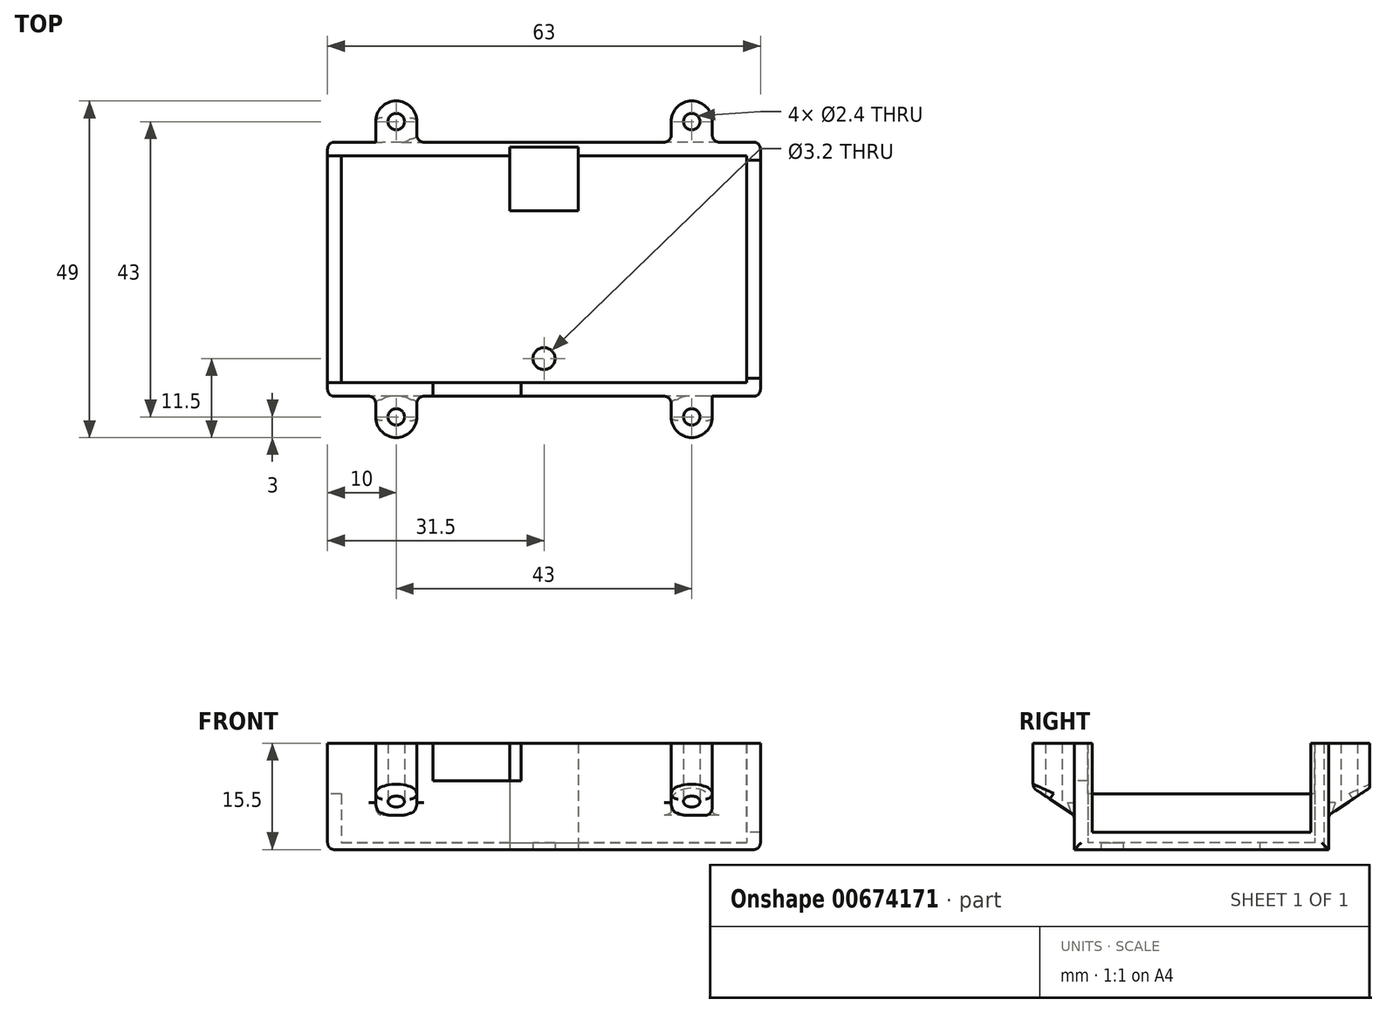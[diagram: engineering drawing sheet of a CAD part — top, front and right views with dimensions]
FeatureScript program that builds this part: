
annotation { "Feature Type Name" : "Feature", "Feature Type Description" : "" }
export const myFeature = defineFeature(function(context is Context, id is Id, definition is map)
    precondition{}
    {
        {
            var Q0;
            Q0=qCreatedBy(makeId("Top.planeOp"),FACE);
            var sketch = newSketch(context, id + "F0", { "sketchPlane" : qUnion([Q0])});
            skCircle(sketch, "E0", {"center": v(-7.34, 20.85) * mm, "radius": 0.75 * mm});
            skCircle(sketch, "E1", {"center": v(1.3, 25.15) * mm, "radius": 0.75 * mm});
            skCircle(sketch, "E2", {"center": v(-5.18, 20.85) * mm, "radius": 0.75 * mm});
            skCircle(sketch, "E3", {"center": v(3.46, 25.15) * mm, "radius": 0.75 * mm});
            skCircle(sketch, "E4", {"center": v(-3.02, 20.85) * mm, "radius": 0.75 * mm});
            skCircle(sketch, "E5", {"center": v(5.62, 25.15) * mm, "radius": 0.75 * mm});
            skCircle(sketch, "E6", {"center": v(-0.86, 20.85) * mm, "radius": 0.75 * mm});
            skCircle(sketch, "E7", {"center": v(1.3, 20.85) * mm, "radius": 0.75 * mm});
            skCircle(sketch, "E8", {"center": v(9.94, 25.15) * mm, "radius": 0.75 * mm});
            skCircle(sketch, "E9", {"center": v(3.46, 20.85) * mm, "radius": 0.75 * mm});
            skCircle(sketch, "E10", {"center": v(12.1, 25.15) * mm, "radius": 0.75 * mm});
            skCircle(sketch, "E11", {"center": v(5.62, 20.85) * mm, "radius": 0.75 * mm});
            skCircle(sketch, "E12", {"center": v(14.26, 25.15) * mm, "radius": 0.75 * mm});
            skCircle(sketch, "E13", {"center": v(7.78, 20.85) * mm, "radius": 0.75 * mm});
            skCircle(sketch, "E14", {"center": v(16.42, 25.15) * mm, "radius": 0.75 * mm});
            skCircle(sketch, "E15", {"center": v(9.94, 20.85) * mm, "radius": 0.75 * mm});
            skCircle(sketch, "E16", {"center": v(16.42, 20.85) * mm, "radius": 0.75 * mm});
            skCircle(sketch, "E17", {"center": v(12.1, 20.85) * mm, "radius": 0.75 * mm});
            skCircle(sketch, "E18", {"center": v(14.26, 20.85) * mm, "radius": 0.75 * mm});
            skCircle(sketch, "E19", {"center": v(7.78, 25.15) * mm, "radius": 0.75 * mm});
            skCircle(sketch, "E20", {"center": v(-7.34, 25.15) * mm, "radius": 0.75 * mm});
            skCircle(sketch, "E21", {"center": v(-5.18, 25.15) * mm, "radius": 0.75 * mm});
            skCircle(sketch, "E22", {"center": v(-3.02, 25.15) * mm, "radius": 0.75 * mm});
            skCircle(sketch, "E23", {"center": v(-0.86, 25.15) * mm, "radius": 0.75 * mm});
            skCircle(sketch, "E24", {"center": v(-18.86, 23) * mm, "radius": 1.6 * mm});
            skCircle(sketch, "E25", {"center": v(27.94, 23) * mm, "radius": 1.6 * mm});
            skLineSegment(sketch, "E26", {"start": v(4.04, 23) * mm, "end": v(5.04, 23) * mm});
            skLineSegment(sketch, "E27", {"start": v(4.54, 22.5) * mm, "end": v(4.54, 23.5) * mm});
            skLineSegment(sketch, "E28", {"start": v(-10.46, 27) * mm, "end": v(19.54, 27) * mm});
            skLineSegment(sketch, "E29", {"start": v(19.54, 27) * mm, "end": v(22.79, 19) * mm});
            skLineSegment(sketch, "E30", {"start": v(22.79, 19) * mm, "end": v(-13.71, 19) * mm});
            skLineSegment(sketch, "E31", {"start": v(-13.71, 19) * mm, "end": v(-10.46, 27) * mm});
            skLineSegment(sketch, "E32", {"start": v(-22.71, 33.4) * mm, "end": v(31.79, 33.4) * mm});
            skLineSegment(sketch, "E33", {"start": v(31.79, 33.4) * mm, "end": v(31.79, 17.1) * mm});
            skLineSegment(sketch, "E34", {"start": v(31.79, 17.1) * mm, "end": v(-22.71, 17.1) * mm});
            skLineSegment(sketch, "E35", {"start": v(-22.71, 17.1) * mm, "end": v(-22.71, 33.4) * mm});
            skCircle(sketch, "E36", {"center": v(29.08, 8.27) * mm, "radius": 0.75 * mm});
            skCircle(sketch, "E37", {"center": v(26.54, 8.27) * mm, "radius": 0.75 * mm});
            skCircle(sketch, "E38", {"center": v(24, 8.27) * mm, "radius": 0.75 * mm});
            skCircle(sketch, "E39", {"center": v(24, 5.73) * mm, "radius": 0.75 * mm});
            skCircle(sketch, "E40", {"center": v(29.08, 5.73) * mm, "radius": 0.75 * mm});
            skCircle(sketch, "E41", {"center": v(26.54, 5.73) * mm, "radius": 0.75 * mm});
            skLineSegment(sketch, "E42", {"start": v(27.04, 7) * mm, "end": v(26.04, 7) * mm});
            skLineSegment(sketch, "E43", {"start": v(26.54, 7.5) * mm, "end": v(26.54, 6.5) * mm});
            skLineSegment(sketch, "E44", {"start": v(31.54, 9.2) * mm, "end": v(31.54, 3.6) * mm});
            skLineSegment(sketch, "E45", {"start": v(31.54, 3.6) * mm, "end": v(21.54, 3.6) * mm});
            skLineSegment(sketch, "E46", {"start": v(21.54, 3.6) * mm, "end": v(21.54, 9.2) * mm});
            skLineSegment(sketch, "E47", {"start": v(21.54, 9.2) * mm, "end": v(31.54, 9.2) * mm});
            skCircle(sketch, "E48", {"center": v(2, -25.73) * mm, "radius": 0.75 * mm});
            skCircle(sketch, "E49", {"center": v(4.54, -25.73) * mm, "radius": 0.75 * mm});
            skCircle(sketch, "E50", {"center": v(7.08, -25.73) * mm, "radius": 0.75 * mm});
            skCircle(sketch, "E51", {"center": v(7.08, -28.27) * mm, "radius": 0.75 * mm});
            skCircle(sketch, "E52", {"center": v(2, -28.27) * mm, "radius": 0.75 * mm});
            skCircle(sketch, "E53", {"center": v(4.54, -28.27) * mm, "radius": 0.75 * mm});
            skLineSegment(sketch, "E54", {"start": v(4.04, -27) * mm, "end": v(5.04, -27) * mm});
            skLineSegment(sketch, "E55", {"start": v(4.54, -26.5) * mm, "end": v(4.54, -27.5) * mm});
            skLineSegment(sketch, "E56", {"start": v(-0.46, -24.8) * mm, "end": v(-0.46, -31.7) * mm});
            skLineSegment(sketch, "E57", {"start": v(-0.46, -31.7) * mm, "end": v(9.54, -31.7) * mm});
            skLineSegment(sketch, "E58", {"start": v(9.54, -31.7) * mm, "end": v(9.54, -24.8) * mm});
            skLineSegment(sketch, "E59", {"start": v(9.54, -24.8) * mm, "end": v(-0.46, -24.8) * mm});
            skLineSegment(sketch, "E60", {"start": v(22.8, 13.74) * mm, "end": v(22.8, 15.26) * mm});
            skLineSegment(sketch, "E61", {"start": v(22.8, 15.26) * mm, "end": v(21.28, 15.26) * mm});
            skLineSegment(sketch, "E62", {"start": v(21.28, 15.26) * mm, "end": v(21.28, 13.74) * mm});
            skLineSegment(sketch, "E63", {"start": v(21.28, 13.74) * mm, "end": v(22.8, 13.74) * mm});
            skCircle(sketch, "E64", {"center": v(24.54, 14.5) * mm, "radius": 0.76 * mm});
            skCircle(sketch, "E65", {"center": v(27.04, 14.5) * mm, "radius": 0.76 * mm});
            skCircle(sketch, "E66", {"center": v(29.54, 14.5) * mm, "radius": 0.76 * mm});
            skLineSegment(sketch, "E67", {"start": v(31.99, 11.12) * mm, "end": v(19.59, 11.12) * mm});
            skLineSegment(sketch, "E68", {"start": v(19.59, 11.12) * mm, "end": v(19.59, 16.02) * mm});
            skLineSegment(sketch, "E69", {"start": v(19.59, 16.02) * mm, "end": v(31.99, 16.02) * mm});
            skLineSegment(sketch, "E70", {"start": v(31.99, 16.02) * mm, "end": v(31.99, 11.12) * mm});
            skLineSegment(sketch, "E71", {"start": v(30.99, 16.02) * mm, "end": v(31.99, 15.02) * mm});
            skLineSegment(sketch, "E72", {"start": v(20.59, 16.02) * mm, "end": v(19.59, 15.02) * mm});
            skLineSegment(sketch, "E73", {"start": v(-2.22, -0.26) * mm, "end": v(-2.22, 1.26) * mm});
            skLineSegment(sketch, "E74", {"start": v(-2.22, 1.26) * mm, "end": v(-0.7, 1.26) * mm});
            skLineSegment(sketch, "E75", {"start": v(-0.7, 1.26) * mm, "end": v(-0.7, -0.26) * mm});
            skLineSegment(sketch, "E76", {"start": v(-0.7, -0.26) * mm, "end": v(-2.22, -0.26) * mm});
            skCircle(sketch, "E77", {"center": v(-3.96, 0.5) * mm, "radius": 0.76 * mm});
            skCircle(sketch, "E78", {"center": v(-6.46, 0.5) * mm, "radius": 0.76 * mm});
            skCircle(sketch, "E79", {"center": v(-8.96, 0.5) * mm, "radius": 0.76 * mm});
            skLineSegment(sketch, "E80", {"start": v(-11.41, -2.88) * mm, "end": v(0.99, -2.88) * mm});
            skLineSegment(sketch, "E81", {"start": v(0.99, -2.88) * mm, "end": v(0.99, 2.02) * mm});
            skLineSegment(sketch, "E82", {"start": v(0.99, 2.02) * mm, "end": v(-11.41, 2.02) * mm});
            skLineSegment(sketch, "E83", {"start": v(-11.41, 2.02) * mm, "end": v(-11.41, -2.88) * mm});
            skLineSegment(sketch, "E84", {"start": v(-10.41, 2.02) * mm, "end": v(-11.41, 1.02) * mm});
            skLineSegment(sketch, "E85", {"start": v(-0.01, 2.02) * mm, "end": v(0.99, 1.02) * mm});
            skLineSegment(sketch, "E86", {"start": v(16.29, 27.5) * mm, "end": v(16.29, 29.5) * mm});
            skLineSegment(sketch, "E87", {"start": v(16.29, 29.5) * mm, "end": v(21.79, 29.5) * mm});
            skLineSegment(sketch, "E88", {"start": v(21.79, 29.5) * mm, "end": v(21.79, 27.5) * mm});
            skLineSegment(sketch, "E89", {"start": v(21.79, 27.5) * mm, "end": v(16.29, 27.5) * mm});
            skLineSegment(sketch, "E90", {"start": v(25.29, 27.5) * mm, "end": v(25.29, 29.5) * mm});
            skLineSegment(sketch, "E91", {"start": v(25.29, 29.5) * mm, "end": v(30.79, 29.5) * mm});
            skLineSegment(sketch, "E92", {"start": v(30.79, 29.5) * mm, "end": v(30.79, 27.5) * mm});
            skLineSegment(sketch, "E93", {"start": v(30.79, 27.5) * mm, "end": v(25.29, 27.5) * mm});
            skLineSegment(sketch, "E94", {"start": v(18.54, 31) * mm, "end": v(28.54, 31) * mm});
            skArc(sketch, "E95", {"start": v(17.29, 29.75) * mm, "mid": v(17.66, 30.63) * mm, "end": v(18.54, 31) * mm});
            skArc(sketch, "E96", {"start": v(29.79, 29.75) * mm, "mid": v(29.42, 30.63) * mm, "end": v(28.54, 31) * mm});
            skLineSegment(sketch, "E97", {"start": v(28.54, 26) * mm, "end": v(18.54, 26) * mm});
            skArc(sketch, "E98", {"start": v(17.29, 27.25) * mm, "mid": v(17.66, 26.37) * mm, "end": v(18.54, 26) * mm});
            skArc(sketch, "E99", {"start": v(29.79, 27.25) * mm, "mid": v(29.42, 26.37) * mm, "end": v(28.54, 26) * mm});
            skLineSegment(sketch, "E100", {"start": v(23.04, 28.5) * mm, "end": v(24.04, 28.5) * mm});
            skLineSegment(sketch, "E101", {"start": v(23.54, 29) * mm, "end": v(23.54, 28) * mm});
            skLineSegment(sketch, "E102", {"start": v(-5.46, -18.25) * mm, "end": v(-7.46, -18.25) * mm});
            skLineSegment(sketch, "E103", {"start": v(-7.46, -18.25) * mm, "end": v(-7.46, -12.75) * mm});
            skLineSegment(sketch, "E104", {"start": v(-7.46, -12.75) * mm, "end": v(-5.46, -12.75) * mm});
            skLineSegment(sketch, "E105", {"start": v(-5.46, -12.75) * mm, "end": v(-5.46, -18.25) * mm});
            skLineSegment(sketch, "E106", {"start": v(-5.46, -9.25) * mm, "end": v(-7.46, -9.25) * mm});
            skLineSegment(sketch, "E107", {"start": v(-7.46, -9.25) * mm, "end": v(-7.46, -3.75) * mm});
            skLineSegment(sketch, "E108", {"start": v(-7.46, -3.75) * mm, "end": v(-5.46, -3.75) * mm});
            skLineSegment(sketch, "E109", {"start": v(-5.46, -3.75) * mm, "end": v(-5.46, -9.25) * mm});
            skLineSegment(sketch, "E110", {"start": v(-8.96, -16) * mm, "end": v(-8.96, -6) * mm});
            skArc(sketch, "E111", {"start": v(-7.71, -17.25) * mm, "mid": v(-8.6, -16.88) * mm, "end": v(-8.96, -16) * mm});
            skArc(sketch, "E112", {"start": v(-7.71, -4.75) * mm, "mid": v(-8.6, -5.12) * mm, "end": v(-8.96, -6) * mm});
            skLineSegment(sketch, "E113", {"start": v(-3.96, -6) * mm, "end": v(-3.96, -16) * mm});
            skArc(sketch, "E114", {"start": v(-5.21, -17.25) * mm, "mid": v(-4.33, -16.88) * mm, "end": v(-3.96, -16) * mm});
            skArc(sketch, "E115", {"start": v(-5.21, -4.75) * mm, "mid": v(-4.33, -5.12) * mm, "end": v(-3.96, -6) * mm});
            skLineSegment(sketch, "E116", {"start": v(-6.46, -11.5) * mm, "end": v(-6.46, -10.5) * mm});
            skLineSegment(sketch, "E117", {"start": v(-6.96, -11) * mm, "end": v(-5.96, -11) * mm});
            skLineSegment(sketch, "E118", {"start": v(14.89, 1.65) * mm, "end": v(17.19, 1.65) * mm});
            skLineSegment(sketch, "E119", {"start": v(17.19, 1.65) * mm, "end": v(17.19, -0.65) * mm});
            skLineSegment(sketch, "E120", {"start": v(17.19, -0.65) * mm, "end": v(14.89, -0.65) * mm});
            skLineSegment(sketch, "E121", {"start": v(14.89, -0.65) * mm, "end": v(14.89, 1.65) * mm});
            skLineSegment(sketch, "E122", {"start": v(14.89, -2.35) * mm, "end": v(17.19, -2.35) * mm});
            skLineSegment(sketch, "E123", {"start": v(17.19, -2.35) * mm, "end": v(17.19, -4.65) * mm});
            skLineSegment(sketch, "E124", {"start": v(17.19, -4.65) * mm, "end": v(14.89, -4.65) * mm});
            skLineSegment(sketch, "E125", {"start": v(14.89, -4.65) * mm, "end": v(14.89, -2.35) * mm});
            skLineSegment(sketch, "E126", {"start": v(16.04, -1.5) * mm, "end": v(15.41, -0.87) * mm});
            skLineSegment(sketch, "E127", {"start": v(15.41, -0.88) * mm, "end": v(16.66, -0.88) * mm});
            skLineSegment(sketch, "E128", {"start": v(16.66, -0.88) * mm, "end": v(16.04, -1.5) * mm});
            skLineSegment(sketch, "E129", {"start": v(17.04, -1.75) * mm, "end": v(16.79, -1.5) * mm});
            skLineSegment(sketch, "E130", {"start": v(16.79, -1.5) * mm, "end": v(15.29, -1.5) * mm});
            skLineSegment(sketch, "E131", {"start": v(15.29, -1.5) * mm, "end": v(15.04, -1.25) * mm});
            skLineSegment(sketch, "E132", {"start": v(18.04, 1.88) * mm, "end": v(18.04, -4.88) * mm});
            skLineSegment(sketch, "E133", {"start": v(18.04, -4.88) * mm, "end": v(14.04, -4.88) * mm});
            skLineSegment(sketch, "E134", {"start": v(14.04, -4.88) * mm, "end": v(14.04, 1.88) * mm});
            skLineSegment(sketch, "E135", {"start": v(14.04, 1.88) * mm, "end": v(18.04, 1.88) * mm});
            skLineSegment(sketch, "E136", {"start": v(16.04, -1.5) * mm, "end": v(16.66, -2.12) * mm});
            skLineSegment(sketch, "E137", {"start": v(16.66, -2.12) * mm, "end": v(15.41, -2.12) * mm});
            skLineSegment(sketch, "E138", {"start": v(15.41, -2.12) * mm, "end": v(16.04, -1.5) * mm});
            skLineSegment(sketch, "E139", {"start": v(19.39, 1.65) * mm, "end": v(21.69, 1.65) * mm});
            skLineSegment(sketch, "E140", {"start": v(21.69, 1.65) * mm, "end": v(21.69, -0.65) * mm});
            skLineSegment(sketch, "E141", {"start": v(21.69, -0.65) * mm, "end": v(19.39, -0.65) * mm});
            skLineSegment(sketch, "E142", {"start": v(19.39, -0.65) * mm, "end": v(19.39, 1.65) * mm});
            skLineSegment(sketch, "E143", {"start": v(19.39, -2.35) * mm, "end": v(21.69, -2.35) * mm});
            skLineSegment(sketch, "E144", {"start": v(21.69, -2.35) * mm, "end": v(21.69, -4.65) * mm});
            skLineSegment(sketch, "E145", {"start": v(21.69, -4.65) * mm, "end": v(19.39, -4.65) * mm});
            skLineSegment(sketch, "E146", {"start": v(19.39, -4.65) * mm, "end": v(19.39, -2.35) * mm});
            skLineSegment(sketch, "E147", {"start": v(20.54, -1.5) * mm, "end": v(19.91, -0.88) * mm});
            skLineSegment(sketch, "E148", {"start": v(19.91, -0.88) * mm, "end": v(21.16, -0.88) * mm});
            skLineSegment(sketch, "E149", {"start": v(21.16, -0.88) * mm, "end": v(20.54, -1.5) * mm});
            skLineSegment(sketch, "E150", {"start": v(21.54, -1.75) * mm, "end": v(21.29, -1.5) * mm});
            skLineSegment(sketch, "E151", {"start": v(21.29, -1.5) * mm, "end": v(19.79, -1.5) * mm});
            skLineSegment(sketch, "E152", {"start": v(19.79, -1.5) * mm, "end": v(19.54, -1.25) * mm});
            skLineSegment(sketch, "E153", {"start": v(22.54, 1.88) * mm, "end": v(22.54, -4.88) * mm});
            skLineSegment(sketch, "E154", {"start": v(22.54, -4.88) * mm, "end": v(18.54, -4.88) * mm});
            skLineSegment(sketch, "E155", {"start": v(18.54, -4.88) * mm, "end": v(18.54, 1.88) * mm});
            skLineSegment(sketch, "E156", {"start": v(18.54, 1.88) * mm, "end": v(22.54, 1.88) * mm});
            skLineSegment(sketch, "E157", {"start": v(20.54, -1.5) * mm, "end": v(21.16, -2.12) * mm});
            skLineSegment(sketch, "E158", {"start": v(21.16, -2.12) * mm, "end": v(19.91, -2.12) * mm});
            skLineSegment(sketch, "E159", {"start": v(19.91, -2.12) * mm, "end": v(20.54, -1.5) * mm});
            skLineSegment(sketch, "E160", {"start": v(-18.96, 17.1) * mm, "end": v(-18.96, 18.9) * mm});
            skLineSegment(sketch, "E161", {"start": v(-18.96, 18.9) * mm, "end": v(-17.96, 18.9) * mm});
            skLineSegment(sketch, "E162", {"start": v(-17.96, 18.9) * mm, "end": v(-17.96, 17.1) * mm});
            skLineSegment(sketch, "E163", {"start": v(-17.96, 17.1) * mm, "end": v(-18.96, 17.1) * mm});
            skLineSegment(sketch, "E164", {"start": v(-15.96, 17.1) * mm, "end": v(-15.96, 18.9) * mm});
            skLineSegment(sketch, "E165", {"start": v(-15.96, 18.9) * mm, "end": v(-14.96, 18.9) * mm});
            skLineSegment(sketch, "E166", {"start": v(-14.96, 18.9) * mm, "end": v(-14.96, 17.1) * mm});
            skLineSegment(sketch, "E167", {"start": v(-14.96, 17.1) * mm, "end": v(-15.96, 17.1) * mm});
            skLineSegment(sketch, "E168", {"start": v(-17.34, 19.12) * mm, "end": v(-19.21, 19.12) * mm});
            skLineSegment(sketch, "E169", {"start": v(-19.21, 19.12) * mm, "end": v(-19.21, 16.88) * mm});
            skLineSegment(sketch, "E170", {"start": v(-19.21, 16.88) * mm, "end": v(-17.34, 16.88) * mm});
            skArc(sketch, "E171", {"start": v(-16.76, 18) * mm, "mid": v(-16.96, 18.2) * mm, "end": v(-17.16, 18) * mm});
            skArc(sketch, "E172", {"start": v(-17.16, 18) * mm, "mid": v(-16.96, 17.8) * mm, "end": v(-16.76, 18) * mm});
            skLineSegment(sketch, "E173", {"start": v(-16.59, 16.88) * mm, "end": v(-14.71, 16.88) * mm});
            skLineSegment(sketch, "E174", {"start": v(-14.71, 16.88) * mm, "end": v(-14.71, 19.12) * mm});
            skLineSegment(sketch, "E175", {"start": v(-14.71, 19.12) * mm, "end": v(-16.59, 19.12) * mm});
            skArc(sketch, "E176", {"start": v(-16.59, 19.12) * mm, "mid": v(-16.96, 18.75) * mm, "end": v(-17.34, 19.12) * mm});
            skArc(sketch, "E177", {"start": v(-17.34, 16.88) * mm, "mid": v(-16.96, 17.25) * mm, "end": v(-16.59, 16.88) * mm});
            skLineSegment(sketch, "E178", {"start": v(-9.81, -9.5) * mm, "end": v(-11.61, -9.5) * mm});
            skLineSegment(sketch, "E179", {"start": v(-11.61, -9.5) * mm, "end": v(-11.61, -8.5) * mm});
            skLineSegment(sketch, "E180", {"start": v(-11.61, -8.5) * mm, "end": v(-9.81, -8.5) * mm});
            skLineSegment(sketch, "E181", {"start": v(-9.81, -8.5) * mm, "end": v(-9.81, -9.5) * mm});
            skLineSegment(sketch, "E182", {"start": v(-9.81, -6.5) * mm, "end": v(-11.61, -6.5) * mm});
            skLineSegment(sketch, "E183", {"start": v(-11.61, -6.5) * mm, "end": v(-11.61, -5.5) * mm});
            skLineSegment(sketch, "E184", {"start": v(-11.61, -5.5) * mm, "end": v(-9.81, -5.5) * mm});
            skLineSegment(sketch, "E185", {"start": v(-9.81, -5.5) * mm, "end": v(-9.81, -6.5) * mm});
            skLineSegment(sketch, "E186", {"start": v(-11.84, -7.88) * mm, "end": v(-11.84, -9.75) * mm});
            skLineSegment(sketch, "E187", {"start": v(-11.84, -9.75) * mm, "end": v(-9.59, -9.75) * mm});
            skLineSegment(sketch, "E188", {"start": v(-9.59, -9.75) * mm, "end": v(-9.59, -7.88) * mm});
            skArc(sketch, "E189", {"start": v(-10.51, -7.5) * mm, "mid": v(-10.71, -7.3) * mm, "end": v(-10.91, -7.5) * mm});
            skArc(sketch, "E190", {"start": v(-10.91, -7.5) * mm, "mid": v(-10.71, -7.7) * mm, "end": v(-10.51, -7.5) * mm});
            skLineSegment(sketch, "E191", {"start": v(-9.59, -7.12) * mm, "end": v(-9.59, -5.25) * mm});
            skLineSegment(sketch, "E192", {"start": v(-9.59, -5.25) * mm, "end": v(-11.84, -5.25) * mm});
            skLineSegment(sketch, "E193", {"start": v(-11.84, -5.25) * mm, "end": v(-11.84, -7.12) * mm});
            skArc(sketch, "E194", {"start": v(-11.84, -7.12) * mm, "mid": v(-11.46, -7.5) * mm, "end": v(-11.84, -7.88) * mm});
            skArc(sketch, "E195", {"start": v(-9.59, -7.88) * mm, "mid": v(-9.96, -7.5) * mm, "end": v(-9.59, -7.12) * mm});
            skLineSegment(sketch, "E196", {"start": v(8.64, 6.85) * mm, "end": v(8.64, 4.15) * mm});
            skLineSegment(sketch, "E197", {"start": v(8.64, 4.15) * mm, "end": v(7.44, 4.15) * mm});
            skLineSegment(sketch, "E198", {"start": v(7.44, 4.15) * mm, "end": v(7.44, 6.85) * mm});
            skLineSegment(sketch, "E199", {"start": v(7.44, 6.85) * mm, "end": v(8.64, 6.85) * mm});
            skLineSegment(sketch, "E200", {"start": v(5.64, 6.85) * mm, "end": v(5.64, 4.15) * mm});
            skLineSegment(sketch, "E201", {"start": v(5.64, 4.15) * mm, "end": v(4.44, 4.15) * mm});
            skLineSegment(sketch, "E202", {"start": v(4.44, 4.15) * mm, "end": v(4.44, 6.85) * mm});
            skLineSegment(sketch, "E203", {"start": v(4.44, 6.85) * mm, "end": v(5.64, 6.85) * mm});
            skArc(sketch, "E204", {"start": v(8.54, 7.1) * mm, "mid": v(8.79, 7) * mm, "end": v(8.89, 6.75) * mm});
            skLineSegment(sketch, "E205", {"start": v(8.89, 4.25) * mm, "end": v(8.89, 6.75) * mm});
            skArc(sketch, "E206", {"start": v(8.89, 4.25) * mm, "mid": v(8.79, 4) * mm, "end": v(8.54, 3.9) * mm});
            skLineSegment(sketch, "E207", {"start": v(4.54, 7.1) * mm, "end": v(8.54, 7.1) * mm});
            skLineSegment(sketch, "E208", {"start": v(8.54, 3.9) * mm, "end": v(4.54, 3.9) * mm});
            skArc(sketch, "E209", {"start": v(6.74, 5.5) * mm, "mid": v(6.54, 5.7) * mm, "end": v(6.34, 5.5) * mm});
            skArc(sketch, "E210", {"start": v(6.34, 5.5) * mm, "mid": v(6.54, 5.3) * mm, "end": v(6.74, 5.5) * mm});
            skArc(sketch, "E211", {"start": v(4.19, 6.75) * mm, "mid": v(4.29, 7) * mm, "end": v(4.54, 7.1) * mm});
            skArc(sketch, "E212", {"start": v(4.54, 3.9) * mm, "mid": v(4.29, 4) * mm, "end": v(4.19, 4.25) * mm});
            skLineSegment(sketch, "E213", {"start": v(4.19, 6.75) * mm, "end": v(4.19, 4.25) * mm});
            skLineSegment(sketch, "E214", {"start": v(4.44, -21.35) * mm, "end": v(4.44, -18.65) * mm});
            skLineSegment(sketch, "E215", {"start": v(4.44, -18.65) * mm, "end": v(5.64, -18.65) * mm});
            skLineSegment(sketch, "E216", {"start": v(5.64, -18.65) * mm, "end": v(5.64, -21.35) * mm});
            skLineSegment(sketch, "E217", {"start": v(5.64, -21.35) * mm, "end": v(4.44, -21.35) * mm});
            skLineSegment(sketch, "E218", {"start": v(7.44, -21.35) * mm, "end": v(7.44, -18.65) * mm});
            skLineSegment(sketch, "E219", {"start": v(7.44, -18.65) * mm, "end": v(8.64, -18.65) * mm});
            skLineSegment(sketch, "E220", {"start": v(8.64, -18.65) * mm, "end": v(8.64, -21.35) * mm});
            skLineSegment(sketch, "E221", {"start": v(8.64, -21.35) * mm, "end": v(7.44, -21.35) * mm});
            skArc(sketch, "E222", {"start": v(4.54, -21.6) * mm, "mid": v(4.29, -21.5) * mm, "end": v(4.19, -21.25) * mm});
            skLineSegment(sketch, "E223", {"start": v(4.19, -18.75) * mm, "end": v(4.19, -21.25) * mm});
            skArc(sketch, "E224", {"start": v(4.19, -18.75) * mm, "mid": v(4.29, -18.5) * mm, "end": v(4.54, -18.4) * mm});
            skLineSegment(sketch, "E225", {"start": v(8.54, -21.6) * mm, "end": v(4.54, -21.6) * mm});
            skLineSegment(sketch, "E226", {"start": v(4.54, -18.4) * mm, "end": v(8.54, -18.4) * mm});
            skArc(sketch, "E227", {"start": v(6.74, -20) * mm, "mid": v(6.54, -19.8) * mm, "end": v(6.34, -20) * mm});
            skArc(sketch, "E228", {"start": v(6.34, -20) * mm, "mid": v(6.54, -20.2) * mm, "end": v(6.74, -20) * mm});
            skArc(sketch, "E229", {"start": v(8.89, -21.25) * mm, "mid": v(8.79, -21.5) * mm, "end": v(8.54, -21.6) * mm});
            skArc(sketch, "E230", {"start": v(8.54, -18.4) * mm, "mid": v(8.79, -18.5) * mm, "end": v(8.89, -18.75) * mm});
            skLineSegment(sketch, "E231", {"start": v(8.89, -21.25) * mm, "end": v(8.89, -18.75) * mm});
            skLineSegment(sketch, "E232", {"start": v(-10.11, 4.85) * mm, "end": v(-10.11, 7.15) * mm});
            skLineSegment(sketch, "E233", {"start": v(-10.11, 7.15) * mm, "end": v(-7.81, 7.15) * mm});
            skLineSegment(sketch, "E234", {"start": v(-7.81, 7.15) * mm, "end": v(-7.81, 4.85) * mm});
            skLineSegment(sketch, "E235", {"start": v(-7.81, 4.85) * mm, "end": v(-10.11, 4.85) * mm});
            skLineSegment(sketch, "E236", {"start": v(-6.11, 4.85) * mm, "end": v(-6.11, 7.15) * mm});
            skLineSegment(sketch, "E237", {"start": v(-6.11, 7.15) * mm, "end": v(-3.81, 7.15) * mm});
            skLineSegment(sketch, "E238", {"start": v(-3.81, 7.15) * mm, "end": v(-3.81, 4.85) * mm});
            skLineSegment(sketch, "E239", {"start": v(-3.81, 4.85) * mm, "end": v(-6.11, 4.85) * mm});
            skLineSegment(sketch, "E240", {"start": v(-7.46, 6) * mm, "end": v(-6.46, 6) * mm});
            skLineSegment(sketch, "E241", {"start": v(-6.96, 6.5) * mm, "end": v(-6.96, 5.5) * mm});
            skLineSegment(sketch, "E242", {"start": v(-10.71, 8) * mm, "end": v(-3.46, 8) * mm});
            skLineSegment(sketch, "E243", {"start": v(-3.46, 8) * mm, "end": v(-3.46, 4) * mm});
            skLineSegment(sketch, "E244", {"start": v(-3.46, 4) * mm, "end": v(-10.71, 4) * mm});
            skLineSegment(sketch, "E245", {"start": v(-10.71, 4) * mm, "end": v(-10.71, 8) * mm});
            skLineSegment(sketch, "E246", {"start": v(-10.71, 7.75) * mm, "end": v(-10.71, 4.25) * mm});
            skLineSegment(sketch, "E247", {"start": v(-10.71, 4.25) * mm, "end": v(-10.71, 4) * mm});
            skLineSegment(sketch, "E248", {"start": v(-10.71, 4) * mm, "end": v(-10.21, 4) * mm});
            skLineSegment(sketch, "E249", {"start": v(-10.21, 4) * mm, "end": v(-10.21, 4.25) * mm});
            skLineSegment(sketch, "E250", {"start": v(-10.21, 4.25) * mm, "end": v(-10.21, 4.75) * mm});
            skLineSegment(sketch, "E251", {"start": v(-10.21, 4.75) * mm, "end": v(-10.21, 7.25) * mm});
            skLineSegment(sketch, "E252", {"start": v(-10.21, 7.25) * mm, "end": v(-10.21, 7.75) * mm});
            skLineSegment(sketch, "E253", {"start": v(-10.21, 7.75) * mm, "end": v(-10.21, 8) * mm});
            skLineSegment(sketch, "E254", {"start": v(-10.21, 8) * mm, "end": v(-10.46, 8) * mm});
            skLineSegment(sketch, "E255", {"start": v(-10.46, 8) * mm, "end": v(-10.71, 8) * mm});
            skLineSegment(sketch, "E256", {"start": v(-10.71, 8) * mm, "end": v(-10.71, 7.75) * mm});
            skLineSegment(sketch, "E257", {"start": v(-15.11, 1.65) * mm, "end": v(-12.81, 1.65) * mm});
            skLineSegment(sketch, "E258", {"start": v(-12.81, 1.65) * mm, "end": v(-12.81, -0.65) * mm});
            skLineSegment(sketch, "E259", {"start": v(-12.81, -0.65) * mm, "end": v(-15.11, -0.65) * mm});
            skLineSegment(sketch, "E260", {"start": v(-15.11, -0.65) * mm, "end": v(-15.11, 1.65) * mm});
            skLineSegment(sketch, "E261", {"start": v(-15.11, -2.35) * mm, "end": v(-12.81, -2.35) * mm});
            skLineSegment(sketch, "E262", {"start": v(-12.81, -2.35) * mm, "end": v(-12.81, -4.65) * mm});
            skLineSegment(sketch, "E263", {"start": v(-12.81, -4.65) * mm, "end": v(-15.11, -4.65) * mm});
            skLineSegment(sketch, "E264", {"start": v(-15.11, -4.65) * mm, "end": v(-15.11, -2.35) * mm});
            skLineSegment(sketch, "E265", {"start": v(-13.96, -1) * mm, "end": v(-13.96, -2) * mm});
            skLineSegment(sketch, "E266", {"start": v(-13.46, -1.5) * mm, "end": v(-14.46, -1.5) * mm});
            skLineSegment(sketch, "E267", {"start": v(-11.96, 2.25) * mm, "end": v(-11.96, -5) * mm});
            skLineSegment(sketch, "E268", {"start": v(-11.96, -5) * mm, "end": v(-15.96, -5) * mm});
            skLineSegment(sketch, "E269", {"start": v(-15.96, -5) * mm, "end": v(-15.96, 2.25) * mm});
            skLineSegment(sketch, "E270", {"start": v(-15.96, 2.25) * mm, "end": v(-11.96, 2.25) * mm});
            skLineSegment(sketch, "E271", {"start": v(-12.21, 2.25) * mm, "end": v(-15.71, 2.25) * mm});
            skLineSegment(sketch, "E272", {"start": v(-15.71, 2.25) * mm, "end": v(-15.96, 2.25) * mm});
            skLineSegment(sketch, "E273", {"start": v(-15.96, 2.25) * mm, "end": v(-15.96, 1.75) * mm});
            skLineSegment(sketch, "E274", {"start": v(-15.96, 1.75) * mm, "end": v(-15.71, 1.75) * mm});
            skLineSegment(sketch, "E275", {"start": v(-15.71, 1.75) * mm, "end": v(-15.21, 1.75) * mm});
            skLineSegment(sketch, "E276", {"start": v(-15.21, 1.75) * mm, "end": v(-12.71, 1.75) * mm});
            skLineSegment(sketch, "E277", {"start": v(-12.71, 1.75) * mm, "end": v(-12.21, 1.75) * mm});
            skLineSegment(sketch, "E278", {"start": v(-12.21, 1.75) * mm, "end": v(-11.96, 1.75) * mm});
            skLineSegment(sketch, "E279", {"start": v(-11.96, 1.75) * mm, "end": v(-11.96, 2) * mm});
            skLineSegment(sketch, "E280", {"start": v(-11.96, 2) * mm, "end": v(-11.96, 2.25) * mm});
            skLineSegment(sketch, "E281", {"start": v(-11.96, 2.25) * mm, "end": v(-12.21, 2.25) * mm});
            skLineSegment(sketch, "E282", {"start": v(3.79, 28) * mm, "end": v(3.79, 27) * mm});
            skLineSegment(sketch, "E283", {"start": v(3.79, 27) * mm, "end": v(2.79, 27) * mm});
            skLineSegment(sketch, "E284", {"start": v(2.79, 27) * mm, "end": v(2.79, 28) * mm});
            skLineSegment(sketch, "E285", {"start": v(2.79, 28) * mm, "end": v(3.79, 28) * mm});
            skLineSegment(sketch, "E286", {"start": v(2.29, 28) * mm, "end": v(2.29, 27) * mm});
            skLineSegment(sketch, "E287", {"start": v(2.29, 27) * mm, "end": v(1.29, 27) * mm});
            skLineSegment(sketch, "E288", {"start": v(1.29, 27) * mm, "end": v(1.29, 28) * mm});
            skLineSegment(sketch, "E289", {"start": v(1.29, 28) * mm, "end": v(2.29, 28) * mm});
            skArc(sketch, "E290", {"start": v(4.04, 27.9) * mm, "mid": v(3.95, 28.11) * mm, "end": v(3.74, 28.2) * mm});
            skLineSegment(sketch, "E291", {"start": v(4.04, 27.1) * mm, "end": v(4.04, 27.9) * mm});
            skArc(sketch, "E292", {"start": v(4.04, 27.1) * mm, "mid": v(3.95, 26.89) * mm, "end": v(3.74, 26.8) * mm});
            skLineSegment(sketch, "E293", {"start": v(1.34, 28.2) * mm, "end": v(3.74, 28.2) * mm});
            skLineSegment(sketch, "E294", {"start": v(3.74, 26.8) * mm, "end": v(1.34, 26.8) * mm});
            skArc(sketch, "E295", {"start": v(2.64, 27.5) * mm, "mid": v(2.54, 27.6) * mm, "end": v(2.44, 27.5) * mm});
            skArc(sketch, "E296", {"start": v(2.44, 27.5) * mm, "mid": v(2.54, 27.4) * mm, "end": v(2.64, 27.5) * mm});
            skArc(sketch, "E297", {"start": v(1.34, 28.2) * mm, "mid": v(1.13, 28.11) * mm, "end": v(1.04, 27.9) * mm});
            skArc(sketch, "E298", {"start": v(1.04, 27.1) * mm, "mid": v(1.13, 26.89) * mm, "end": v(1.34, 26.8) * mm});
            skLineSegment(sketch, "E299", {"start": v(1.04, 27.9) * mm, "end": v(1.04, 27.1) * mm});
            skLineSegment(sketch, "E300", {"start": v(4.79, 16.5) * mm, "end": v(4.79, 17.5) * mm});
            skLineSegment(sketch, "E301", {"start": v(4.79, 17.5) * mm, "end": v(5.79, 17.5) * mm});
            skLineSegment(sketch, "E302", {"start": v(5.79, 17.5) * mm, "end": v(5.79, 16.5) * mm});
            skLineSegment(sketch, "E303", {"start": v(5.79, 16.5) * mm, "end": v(4.79, 16.5) * mm});
            skLineSegment(sketch, "E304", {"start": v(6.29, 16.5) * mm, "end": v(6.29, 17.5) * mm});
            skLineSegment(sketch, "E305", {"start": v(6.29, 17.5) * mm, "end": v(7.29, 17.5) * mm});
            skLineSegment(sketch, "E306", {"start": v(7.29, 17.5) * mm, "end": v(7.29, 16.5) * mm});
            skLineSegment(sketch, "E307", {"start": v(7.29, 16.5) * mm, "end": v(6.29, 16.5) * mm});
            skArc(sketch, "E308", {"start": v(4.54, 16.6) * mm, "mid": v(4.63, 16.39) * mm, "end": v(4.84, 16.3) * mm});
            skLineSegment(sketch, "E309", {"start": v(4.54, 17.4) * mm, "end": v(4.54, 16.6) * mm});
            skArc(sketch, "E310", {"start": v(4.54, 17.4) * mm, "mid": v(4.63, 17.61) * mm, "end": v(4.84, 17.7) * mm});
            skLineSegment(sketch, "E311", {"start": v(7.24, 16.3) * mm, "end": v(4.84, 16.3) * mm});
            skLineSegment(sketch, "E312", {"start": v(4.84, 17.7) * mm, "end": v(7.24, 17.7) * mm});
            skArc(sketch, "E313", {"start": v(6.14, 17) * mm, "mid": v(6.04, 17.1) * mm, "end": v(5.94, 17) * mm});
            skArc(sketch, "E314", {"start": v(5.94, 17) * mm, "mid": v(6.04, 16.9) * mm, "end": v(6.14, 17) * mm});
            skArc(sketch, "E315", {"start": v(7.24, 16.3) * mm, "mid": v(7.45, 16.39) * mm, "end": v(7.54, 16.6) * mm});
            skArc(sketch, "E316", {"start": v(7.54, 17.4) * mm, "mid": v(7.45, 17.61) * mm, "end": v(7.24, 17.7) * mm});
            skLineSegment(sketch, "E317", {"start": v(7.54, 16.6) * mm, "end": v(7.54, 17.4) * mm});
            skLineSegment(sketch, "E318", {"start": v(21.04, 17.75) * mm, "end": v(21.04, 18.75) * mm});
            skLineSegment(sketch, "E319", {"start": v(21.04, 18.75) * mm, "end": v(22.04, 18.75) * mm});
            skLineSegment(sketch, "E320", {"start": v(22.04, 18.75) * mm, "end": v(22.04, 17.75) * mm});
            skLineSegment(sketch, "E321", {"start": v(22.04, 17.75) * mm, "end": v(21.04, 17.75) * mm});
            skLineSegment(sketch, "E322", {"start": v(22.54, 17.75) * mm, "end": v(22.54, 18.75) * mm});
            skLineSegment(sketch, "E323", {"start": v(22.54, 18.75) * mm, "end": v(23.54, 18.75) * mm});
            skLineSegment(sketch, "E324", {"start": v(23.54, 18.75) * mm, "end": v(23.54, 17.75) * mm});
            skLineSegment(sketch, "E325", {"start": v(23.54, 17.75) * mm, "end": v(22.54, 17.75) * mm});
            skArc(sketch, "E326", {"start": v(20.79, 17.85) * mm, "mid": v(20.88, 17.64) * mm, "end": v(21.09, 17.55) * mm});
            skLineSegment(sketch, "E327", {"start": v(20.79, 18.65) * mm, "end": v(20.79, 17.85) * mm});
            skArc(sketch, "E328", {"start": v(20.79, 18.65) * mm, "mid": v(20.88, 18.86) * mm, "end": v(21.09, 18.95) * mm});
            skLineSegment(sketch, "E329", {"start": v(23.49, 17.55) * mm, "end": v(21.09, 17.55) * mm});
            skLineSegment(sketch, "E330", {"start": v(21.09, 18.95) * mm, "end": v(23.49, 18.95) * mm});
            skArc(sketch, "E331", {"start": v(22.39, 18.25) * mm, "mid": v(22.29, 18.35) * mm, "end": v(22.19, 18.25) * mm});
            skArc(sketch, "E332", {"start": v(22.19, 18.25) * mm, "mid": v(22.29, 18.15) * mm, "end": v(22.39, 18.25) * mm});
            skArc(sketch, "E333", {"start": v(23.49, 17.55) * mm, "mid": v(23.7, 17.64) * mm, "end": v(23.79, 17.85) * mm});
            skArc(sketch, "E334", {"start": v(23.79, 18.65) * mm, "mid": v(23.7, 18.86) * mm, "end": v(23.49, 18.95) * mm});
            skLineSegment(sketch, "E335", {"start": v(23.79, 17.85) * mm, "end": v(23.79, 18.65) * mm});
            skLineSegment(sketch, "E336", {"start": v(18.29, 25.25) * mm, "end": v(19.29, 25.25) * mm});
            skLineSegment(sketch, "E337", {"start": v(19.29, 25.25) * mm, "end": v(19.29, 24.25) * mm});
            skLineSegment(sketch, "E338", {"start": v(19.29, 24.25) * mm, "end": v(18.29, 24.25) * mm});
            skLineSegment(sketch, "E339", {"start": v(18.29, 24.25) * mm, "end": v(18.29, 25.25) * mm});
            skLineSegment(sketch, "E340", {"start": v(18.29, 23.75) * mm, "end": v(19.29, 23.75) * mm});
            skLineSegment(sketch, "E341", {"start": v(19.29, 23.75) * mm, "end": v(19.29, 22.75) * mm});
            skLineSegment(sketch, "E342", {"start": v(19.29, 22.75) * mm, "end": v(18.29, 22.75) * mm});
            skLineSegment(sketch, "E343", {"start": v(18.29, 22.75) * mm, "end": v(18.29, 23.75) * mm});
            skArc(sketch, "E344", {"start": v(18.39, 25.5) * mm, "mid": v(18.18, 25.41) * mm, "end": v(18.09, 25.2) * mm});
            skLineSegment(sketch, "E345", {"start": v(19.19, 25.5) * mm, "end": v(18.39, 25.5) * mm});
            skArc(sketch, "E346", {"start": v(19.19, 25.5) * mm, "mid": v(19.4, 25.41) * mm, "end": v(19.49, 25.2) * mm});
            skLineSegment(sketch, "E347", {"start": v(18.09, 22.8) * mm, "end": v(18.09, 25.2) * mm});
            skLineSegment(sketch, "E348", {"start": v(19.49, 25.2) * mm, "end": v(19.49, 22.8) * mm});
            skArc(sketch, "E349", {"start": v(18.89, 24) * mm, "mid": v(18.79, 24.1) * mm, "end": v(18.69, 24) * mm});
            skArc(sketch, "E350", {"start": v(18.69, 24) * mm, "mid": v(18.79, 23.9) * mm, "end": v(18.89, 24) * mm});
            skArc(sketch, "E351", {"start": v(18.09, 22.8) * mm, "mid": v(18.18, 22.59) * mm, "end": v(18.39, 22.5) * mm});
            skArc(sketch, "E352", {"start": v(19.19, 22.5) * mm, "mid": v(19.4, 22.59) * mm, "end": v(19.49, 22.8) * mm});
            skLineSegment(sketch, "E353", {"start": v(18.39, 22.5) * mm, "end": v(19.19, 22.5) * mm});
            skLineSegment(sketch, "E354", {"start": v(11.04, 4.25) * mm, "end": v(10.04, 4.25) * mm});
            skLineSegment(sketch, "E355", {"start": v(10.04, 4.25) * mm, "end": v(10.04, 5.25) * mm});
            skLineSegment(sketch, "E356", {"start": v(10.04, 5.25) * mm, "end": v(11.04, 5.25) * mm});
            skLineSegment(sketch, "E357", {"start": v(11.04, 5.25) * mm, "end": v(11.04, 4.25) * mm});
            skLineSegment(sketch, "E358", {"start": v(11.04, 5.75) * mm, "end": v(10.04, 5.75) * mm});
            skLineSegment(sketch, "E359", {"start": v(10.04, 5.75) * mm, "end": v(10.04, 6.75) * mm});
            skLineSegment(sketch, "E360", {"start": v(10.04, 6.75) * mm, "end": v(11.04, 6.75) * mm});
            skLineSegment(sketch, "E361", {"start": v(11.04, 6.75) * mm, "end": v(11.04, 5.75) * mm});
            skArc(sketch, "E362", {"start": v(10.94, 4) * mm, "mid": v(11.15, 4.09) * mm, "end": v(11.24, 4.3) * mm});
            skLineSegment(sketch, "E363", {"start": v(10.14, 4) * mm, "end": v(10.94, 4) * mm});
            skArc(sketch, "E364", {"start": v(10.14, 4) * mm, "mid": v(9.93, 4.09) * mm, "end": v(9.84, 4.3) * mm});
            skLineSegment(sketch, "E365", {"start": v(11.24, 6.7) * mm, "end": v(11.24, 4.3) * mm});
            skLineSegment(sketch, "E366", {"start": v(9.84, 4.3) * mm, "end": v(9.84, 6.7) * mm});
            skArc(sketch, "E367", {"start": v(10.64, 5.5) * mm, "mid": v(10.54, 5.6) * mm, "end": v(10.44, 5.5) * mm});
            skArc(sketch, "E368", {"start": v(10.44, 5.5) * mm, "mid": v(10.54, 5.4) * mm, "end": v(10.64, 5.5) * mm});
            skArc(sketch, "E369", {"start": v(11.24, 6.7) * mm, "mid": v(11.15, 6.91) * mm, "end": v(10.94, 7) * mm});
            skArc(sketch, "E370", {"start": v(10.14, 7) * mm, "mid": v(9.93, 6.91) * mm, "end": v(9.84, 6.7) * mm});
            skLineSegment(sketch, "E371", {"start": v(10.94, 7) * mm, "end": v(10.14, 7) * mm});
            skLineSegment(sketch, "E372", {"start": v(23.29, 22.75) * mm, "end": v(22.29, 22.75) * mm});
            skLineSegment(sketch, "E373", {"start": v(22.29, 22.75) * mm, "end": v(22.29, 23.75) * mm});
            skLineSegment(sketch, "E374", {"start": v(22.29, 23.75) * mm, "end": v(23.29, 23.75) * mm});
            skLineSegment(sketch, "E375", {"start": v(23.29, 23.75) * mm, "end": v(23.29, 22.75) * mm});
            skLineSegment(sketch, "E376", {"start": v(23.29, 24.25) * mm, "end": v(22.29, 24.25) * mm});
            skLineSegment(sketch, "E377", {"start": v(22.29, 24.25) * mm, "end": v(22.29, 25.25) * mm});
            skLineSegment(sketch, "E378", {"start": v(22.29, 25.25) * mm, "end": v(23.29, 25.25) * mm});
            skLineSegment(sketch, "E379", {"start": v(23.29, 25.25) * mm, "end": v(23.29, 24.25) * mm});
            skArc(sketch, "E380", {"start": v(23.19, 22.5) * mm, "mid": v(23.4, 22.59) * mm, "end": v(23.49, 22.8) * mm});
            skLineSegment(sketch, "E381", {"start": v(22.39, 22.5) * mm, "end": v(23.19, 22.5) * mm});
            skArc(sketch, "E382", {"start": v(22.39, 22.5) * mm, "mid": v(22.18, 22.59) * mm, "end": v(22.09, 22.8) * mm});
            skLineSegment(sketch, "E383", {"start": v(23.49, 25.2) * mm, "end": v(23.49, 22.8) * mm});
            skLineSegment(sketch, "E384", {"start": v(22.09, 22.8) * mm, "end": v(22.09, 25.2) * mm});
            skArc(sketch, "E385", {"start": v(22.89, 24) * mm, "mid": v(22.79, 24.1) * mm, "end": v(22.69, 24) * mm});
            skArc(sketch, "E386", {"start": v(22.69, 24) * mm, "mid": v(22.79, 23.9) * mm, "end": v(22.89, 24) * mm});
            skArc(sketch, "E387", {"start": v(23.49, 25.2) * mm, "mid": v(23.4, 25.41) * mm, "end": v(23.19, 25.5) * mm});
            skArc(sketch, "E388", {"start": v(22.39, 25.5) * mm, "mid": v(22.18, 25.41) * mm, "end": v(22.09, 25.2) * mm});
            skLineSegment(sketch, "E389", {"start": v(23.19, 25.5) * mm, "end": v(22.39, 25.5) * mm});
            skLineSegment(sketch, "E390", {"start": v(-12.46, 29.25) * mm, "end": v(-13.46, 29.25) * mm});
            skLineSegment(sketch, "E391", {"start": v(-13.46, 29.25) * mm, "end": v(-13.46, 30.25) * mm});
            skLineSegment(sketch, "E392", {"start": v(-13.46, 30.25) * mm, "end": v(-12.46, 30.25) * mm});
            skLineSegment(sketch, "E393", {"start": v(-12.46, 30.25) * mm, "end": v(-12.46, 29.25) * mm});
            skLineSegment(sketch, "E394", {"start": v(-12.46, 30.75) * mm, "end": v(-13.46, 30.75) * mm});
            skLineSegment(sketch, "E395", {"start": v(-13.46, 30.75) * mm, "end": v(-13.46, 31.75) * mm});
            skLineSegment(sketch, "E396", {"start": v(-13.46, 31.75) * mm, "end": v(-12.46, 31.75) * mm});
            skLineSegment(sketch, "E397", {"start": v(-12.46, 31.75) * mm, "end": v(-12.46, 30.75) * mm});
            skArc(sketch, "E398", {"start": v(-12.56, 29) * mm, "mid": v(-12.35, 29.09) * mm, "end": v(-12.26, 29.3) * mm});
            skLineSegment(sketch, "E399", {"start": v(-13.36, 29) * mm, "end": v(-12.56, 29) * mm});
            skArc(sketch, "E400", {"start": v(-13.36, 29) * mm, "mid": v(-13.57, 29.09) * mm, "end": v(-13.66, 29.3) * mm});
            skLineSegment(sketch, "E401", {"start": v(-12.26, 31.7) * mm, "end": v(-12.26, 29.3) * mm});
            skLineSegment(sketch, "E402", {"start": v(-13.66, 29.3) * mm, "end": v(-13.66, 31.7) * mm});
            skArc(sketch, "E403", {"start": v(-12.86, 30.5) * mm, "mid": v(-12.96, 30.6) * mm, "end": v(-13.06, 30.5) * mm});
            skArc(sketch, "E404", {"start": v(-13.06, 30.5) * mm, "mid": v(-12.96, 30.4) * mm, "end": v(-12.86, 30.5) * mm});
            skArc(sketch, "E405", {"start": v(-12.26, 31.7) * mm, "mid": v(-12.35, 31.91) * mm, "end": v(-12.56, 32) * mm});
            skArc(sketch, "E406", {"start": v(-13.36, 32) * mm, "mid": v(-13.57, 31.91) * mm, "end": v(-13.66, 31.7) * mm});
            skLineSegment(sketch, "E407", {"start": v(-12.56, 32) * mm, "end": v(-13.36, 32) * mm});
            skLineSegment(sketch, "E408", {"start": v(3.79, 30.5) * mm, "end": v(3.79, 29.5) * mm});
            skLineSegment(sketch, "E409", {"start": v(3.79, 29.5) * mm, "end": v(2.79, 29.5) * mm});
            skLineSegment(sketch, "E410", {"start": v(2.79, 29.5) * mm, "end": v(2.79, 30.5) * mm});
            skLineSegment(sketch, "E411", {"start": v(2.79, 30.5) * mm, "end": v(3.79, 30.5) * mm});
            skLineSegment(sketch, "E412", {"start": v(2.29, 30.5) * mm, "end": v(2.29, 29.5) * mm});
            skLineSegment(sketch, "E413", {"start": v(2.29, 29.5) * mm, "end": v(1.29, 29.5) * mm});
            skLineSegment(sketch, "E414", {"start": v(1.29, 29.5) * mm, "end": v(1.29, 30.5) * mm});
            skLineSegment(sketch, "E415", {"start": v(1.29, 30.5) * mm, "end": v(2.29, 30.5) * mm});
            skArc(sketch, "E416", {"start": v(4.04, 30.4) * mm, "mid": v(3.95, 30.61) * mm, "end": v(3.74, 30.7) * mm});
            skLineSegment(sketch, "E417", {"start": v(4.04, 29.6) * mm, "end": v(4.04, 30.4) * mm});
            skArc(sketch, "E418", {"start": v(4.04, 29.6) * mm, "mid": v(3.95, 29.39) * mm, "end": v(3.74, 29.3) * mm});
            skLineSegment(sketch, "E419", {"start": v(1.34, 30.7) * mm, "end": v(3.74, 30.7) * mm});
            skLineSegment(sketch, "E420", {"start": v(3.74, 29.3) * mm, "end": v(1.34, 29.3) * mm});
            skArc(sketch, "E421", {"start": v(2.64, 30) * mm, "mid": v(2.54, 30.1) * mm, "end": v(2.44, 30) * mm});
            skArc(sketch, "E422", {"start": v(2.44, 30) * mm, "mid": v(2.54, 29.9) * mm, "end": v(2.64, 30) * mm});
            skArc(sketch, "E423", {"start": v(1.34, 30.7) * mm, "mid": v(1.13, 30.61) * mm, "end": v(1.04, 30.4) * mm});
            skArc(sketch, "E424", {"start": v(1.04, 29.6) * mm, "mid": v(1.13, 29.39) * mm, "end": v(1.34, 29.3) * mm});
            skLineSegment(sketch, "E425", {"start": v(1.04, 30.4) * mm, "end": v(1.04, 29.6) * mm});
            skLineSegment(sketch, "E426", {"start": v(21.04, 19.25) * mm, "end": v(21.04, 20.25) * mm});
            skLineSegment(sketch, "E427", {"start": v(21.04, 20.25) * mm, "end": v(22.04, 20.25) * mm});
            skLineSegment(sketch, "E428", {"start": v(22.04, 20.25) * mm, "end": v(22.04, 19.25) * mm});
            skLineSegment(sketch, "E429", {"start": v(22.04, 19.25) * mm, "end": v(21.04, 19.25) * mm});
            skLineSegment(sketch, "E430", {"start": v(22.54, 19.25) * mm, "end": v(22.54, 20.25) * mm});
            skLineSegment(sketch, "E431", {"start": v(22.54, 20.25) * mm, "end": v(23.54, 20.25) * mm});
            skLineSegment(sketch, "E432", {"start": v(23.54, 20.25) * mm, "end": v(23.54, 19.25) * mm});
            skLineSegment(sketch, "E433", {"start": v(23.54, 19.25) * mm, "end": v(22.54, 19.25) * mm});
            skArc(sketch, "E434", {"start": v(20.79, 19.35) * mm, "mid": v(20.88, 19.14) * mm, "end": v(21.09, 19.05) * mm});
            skLineSegment(sketch, "E435", {"start": v(20.79, 20.15) * mm, "end": v(20.79, 19.35) * mm});
            skArc(sketch, "E436", {"start": v(20.79, 20.15) * mm, "mid": v(20.88, 20.36) * mm, "end": v(21.09, 20.45) * mm});
            skLineSegment(sketch, "E437", {"start": v(23.49, 19.05) * mm, "end": v(21.09, 19.05) * mm});
            skLineSegment(sketch, "E438", {"start": v(21.09, 20.45) * mm, "end": v(23.49, 20.45) * mm});
            skArc(sketch, "E439", {"start": v(22.39, 19.75) * mm, "mid": v(22.29, 19.85) * mm, "end": v(22.19, 19.75) * mm});
            skArc(sketch, "E440", {"start": v(22.19, 19.75) * mm, "mid": v(22.29, 19.65) * mm, "end": v(22.39, 19.75) * mm});
            skArc(sketch, "E441", {"start": v(23.49, 19.05) * mm, "mid": v(23.7, 19.14) * mm, "end": v(23.79, 19.35) * mm});
            skArc(sketch, "E442", {"start": v(23.79, 20.15) * mm, "mid": v(23.7, 20.36) * mm, "end": v(23.49, 20.45) * mm});
            skLineSegment(sketch, "E443", {"start": v(23.79, 19.35) * mm, "end": v(23.79, 20.15) * mm});
            skLineSegment(sketch, "E444", {"start": v(20.79, 25.25) * mm, "end": v(21.79, 25.25) * mm});
            skLineSegment(sketch, "E445", {"start": v(21.79, 25.25) * mm, "end": v(21.79, 24.25) * mm});
            skLineSegment(sketch, "E446", {"start": v(21.79, 24.25) * mm, "end": v(20.79, 24.25) * mm});
            skLineSegment(sketch, "E447", {"start": v(20.79, 24.25) * mm, "end": v(20.79, 25.25) * mm});
            skLineSegment(sketch, "E448", {"start": v(20.79, 23.75) * mm, "end": v(21.79, 23.75) * mm});
            skLineSegment(sketch, "E449", {"start": v(21.79, 23.75) * mm, "end": v(21.79, 22.75) * mm});
            skLineSegment(sketch, "E450", {"start": v(21.79, 22.75) * mm, "end": v(20.79, 22.75) * mm});
            skLineSegment(sketch, "E451", {"start": v(20.79, 22.75) * mm, "end": v(20.79, 23.75) * mm});
            skArc(sketch, "E452", {"start": v(20.89, 25.5) * mm, "mid": v(20.68, 25.41) * mm, "end": v(20.59, 25.2) * mm});
            skLineSegment(sketch, "E453", {"start": v(21.69, 25.5) * mm, "end": v(20.89, 25.5) * mm});
            skArc(sketch, "E454", {"start": v(21.69, 25.5) * mm, "mid": v(21.9, 25.41) * mm, "end": v(21.99, 25.2) * mm});
            skLineSegment(sketch, "E455", {"start": v(20.59, 22.8) * mm, "end": v(20.59, 25.2) * mm});
            skLineSegment(sketch, "E456", {"start": v(21.99, 25.2) * mm, "end": v(21.99, 22.8) * mm});
            skArc(sketch, "E457", {"start": v(21.39, 24) * mm, "mid": v(21.29, 24.1) * mm, "end": v(21.19, 24) * mm});
            skArc(sketch, "E458", {"start": v(21.19, 24) * mm, "mid": v(21.29, 23.9) * mm, "end": v(21.39, 24) * mm});
            skArc(sketch, "E459", {"start": v(20.59, 22.8) * mm, "mid": v(20.68, 22.59) * mm, "end": v(20.89, 22.5) * mm});
            skArc(sketch, "E460", {"start": v(21.69, 22.5) * mm, "mid": v(21.9, 22.59) * mm, "end": v(21.99, 22.8) * mm});
            skLineSegment(sketch, "E461", {"start": v(20.89, 22.5) * mm, "end": v(21.69, 22.5) * mm});
            skLineSegment(sketch, "E462", {"start": v(21.04, 16.25) * mm, "end": v(21.04, 17.25) * mm});
            skLineSegment(sketch, "E463", {"start": v(21.04, 17.25) * mm, "end": v(22.04, 17.25) * mm});
            skLineSegment(sketch, "E464", {"start": v(22.04, 17.25) * mm, "end": v(22.04, 16.25) * mm});
            skLineSegment(sketch, "E465", {"start": v(22.04, 16.25) * mm, "end": v(21.04, 16.25) * mm});
            skLineSegment(sketch, "E466", {"start": v(22.54, 16.25) * mm, "end": v(22.54, 17.25) * mm});
            skLineSegment(sketch, "E467", {"start": v(22.54, 17.25) * mm, "end": v(23.54, 17.25) * mm});
            skLineSegment(sketch, "E468", {"start": v(23.54, 17.25) * mm, "end": v(23.54, 16.25) * mm});
            skLineSegment(sketch, "E469", {"start": v(23.54, 16.25) * mm, "end": v(22.54, 16.25) * mm});
            skArc(sketch, "E470", {"start": v(20.79, 16.35) * mm, "mid": v(20.88, 16.14) * mm, "end": v(21.09, 16.05) * mm});
            skLineSegment(sketch, "E471", {"start": v(20.79, 17.15) * mm, "end": v(20.79, 16.35) * mm});
            skArc(sketch, "E472", {"start": v(20.79, 17.15) * mm, "mid": v(20.88, 17.36) * mm, "end": v(21.09, 17.45) * mm});
            skLineSegment(sketch, "E473", {"start": v(23.49, 16.05) * mm, "end": v(21.09, 16.05) * mm});
            skLineSegment(sketch, "E474", {"start": v(21.09, 17.45) * mm, "end": v(23.49, 17.45) * mm});
            skArc(sketch, "E475", {"start": v(22.39, 16.75) * mm, "mid": v(22.29, 16.85) * mm, "end": v(22.19, 16.75) * mm});
            skArc(sketch, "E476", {"start": v(22.19, 16.75) * mm, "mid": v(22.29, 16.65) * mm, "end": v(22.39, 16.75) * mm});
            skArc(sketch, "E477", {"start": v(23.49, 16.05) * mm, "mid": v(23.7, 16.14) * mm, "end": v(23.79, 16.35) * mm});
            skArc(sketch, "E478", {"start": v(23.79, 17.15) * mm, "mid": v(23.7, 17.36) * mm, "end": v(23.49, 17.45) * mm});
            skLineSegment(sketch, "E479", {"start": v(23.79, 16.35) * mm, "end": v(23.79, 17.15) * mm});
            skLineSegment(sketch, "E480", {"start": v(-1.96, -14.25) * mm, "end": v(-2.96, -14.25) * mm});
            skLineSegment(sketch, "E481", {"start": v(-2.96, -14.25) * mm, "end": v(-2.96, -13.25) * mm});
            skLineSegment(sketch, "E482", {"start": v(-2.96, -13.25) * mm, "end": v(-1.96, -13.25) * mm});
            skLineSegment(sketch, "E483", {"start": v(-1.96, -13.25) * mm, "end": v(-1.96, -14.25) * mm});
            skLineSegment(sketch, "E484", {"start": v(-1.96, -12.75) * mm, "end": v(-2.96, -12.75) * mm});
            skLineSegment(sketch, "E485", {"start": v(-2.96, -12.75) * mm, "end": v(-2.96, -11.75) * mm});
            skLineSegment(sketch, "E486", {"start": v(-2.96, -11.75) * mm, "end": v(-1.96, -11.75) * mm});
            skLineSegment(sketch, "E487", {"start": v(-1.96, -11.75) * mm, "end": v(-1.96, -12.75) * mm});
            skArc(sketch, "E488", {"start": v(-2.06, -14.5) * mm, "mid": v(-1.85, -14.41) * mm, "end": v(-1.76, -14.2) * mm});
            skLineSegment(sketch, "E489", {"start": v(-2.86, -14.5) * mm, "end": v(-2.06, -14.5) * mm});
            skArc(sketch, "E490", {"start": v(-2.86, -14.5) * mm, "mid": v(-3.07, -14.41) * mm, "end": v(-3.16, -14.2) * mm});
            skLineSegment(sketch, "E491", {"start": v(-1.76, -11.8) * mm, "end": v(-1.76, -14.2) * mm});
            skLineSegment(sketch, "E492", {"start": v(-3.16, -14.2) * mm, "end": v(-3.16, -11.8) * mm});
            skArc(sketch, "E493", {"start": v(-2.36, -13) * mm, "mid": v(-2.46, -12.9) * mm, "end": v(-2.56, -13) * mm});
            skArc(sketch, "E494", {"start": v(-2.56, -13) * mm, "mid": v(-2.46, -13.1) * mm, "end": v(-2.36, -13) * mm});
            skArc(sketch, "E495", {"start": v(-1.76, -11.8) * mm, "mid": v(-1.85, -11.59) * mm, "end": v(-2.06, -11.5) * mm});
            skArc(sketch, "E496", {"start": v(-2.86, -11.5) * mm, "mid": v(-3.07, -11.59) * mm, "end": v(-3.16, -11.8) * mm});
            skLineSegment(sketch, "E497", {"start": v(-2.06, -11.5) * mm, "end": v(-2.86, -11.5) * mm});
            skLineSegment(sketch, "E498", {"start": v(12.54, -9.25) * mm, "end": v(13.54, -9.25) * mm});
            skLineSegment(sketch, "E499", {"start": v(13.54, -9.25) * mm, "end": v(13.54, -10.25) * mm});
            skLineSegment(sketch, "E500", {"start": v(13.54, -10.25) * mm, "end": v(12.54, -10.25) * mm});
            skLineSegment(sketch, "E501", {"start": v(12.54, -10.25) * mm, "end": v(12.54, -9.25) * mm});
            skLineSegment(sketch, "E502", {"start": v(12.54, -10.75) * mm, "end": v(13.54, -10.75) * mm});
            skLineSegment(sketch, "E503", {"start": v(13.54, -10.75) * mm, "end": v(13.54, -11.75) * mm});
            skLineSegment(sketch, "E504", {"start": v(13.54, -11.75) * mm, "end": v(12.54, -11.75) * mm});
            skLineSegment(sketch, "E505", {"start": v(12.54, -11.75) * mm, "end": v(12.54, -10.75) * mm});
            skArc(sketch, "E506", {"start": v(12.64, -9) * mm, "mid": v(12.43, -9.09) * mm, "end": v(12.34, -9.3) * mm});
            skLineSegment(sketch, "E507", {"start": v(13.44, -9) * mm, "end": v(12.64, -9) * mm});
            skArc(sketch, "E508", {"start": v(13.44, -9) * mm, "mid": v(13.65, -9.09) * mm, "end": v(13.74, -9.3) * mm});
            skLineSegment(sketch, "E509", {"start": v(12.34, -11.7) * mm, "end": v(12.34, -9.3) * mm});
            skLineSegment(sketch, "E510", {"start": v(13.74, -9.3) * mm, "end": v(13.74, -11.7) * mm});
            skArc(sketch, "E511", {"start": v(13.14, -10.5) * mm, "mid": v(13.04, -10.4) * mm, "end": v(12.94, -10.5) * mm});
            skArc(sketch, "E512", {"start": v(12.94, -10.5) * mm, "mid": v(13.04, -10.6) * mm, "end": v(13.14, -10.5) * mm});
            skArc(sketch, "E513", {"start": v(12.34, -11.7) * mm, "mid": v(12.43, -11.91) * mm, "end": v(12.64, -12) * mm});
            skArc(sketch, "E514", {"start": v(13.44, -12) * mm, "mid": v(13.65, -11.91) * mm, "end": v(13.74, -11.7) * mm});
            skLineSegment(sketch, "E515", {"start": v(12.64, -12) * mm, "end": v(13.44, -12) * mm});
            skLineSegment(sketch, "E516", {"start": v(12.54, -16.25) * mm, "end": v(13.54, -16.25) * mm});
            skLineSegment(sketch, "E517", {"start": v(13.54, -16.25) * mm, "end": v(13.54, -17.25) * mm});
            skLineSegment(sketch, "E518", {"start": v(13.54, -17.25) * mm, "end": v(12.54, -17.25) * mm});
            skLineSegment(sketch, "E519", {"start": v(12.54, -17.25) * mm, "end": v(12.54, -16.25) * mm});
            skLineSegment(sketch, "E520", {"start": v(12.54, -17.75) * mm, "end": v(13.54, -17.75) * mm});
            skLineSegment(sketch, "E521", {"start": v(13.54, -17.75) * mm, "end": v(13.54, -18.75) * mm});
            skLineSegment(sketch, "E522", {"start": v(13.54, -18.75) * mm, "end": v(12.54, -18.75) * mm});
            skLineSegment(sketch, "E523", {"start": v(12.54, -18.75) * mm, "end": v(12.54, -17.75) * mm});
            skArc(sketch, "E524", {"start": v(12.64, -16) * mm, "mid": v(12.43, -16.09) * mm, "end": v(12.34, -16.3) * mm});
            skLineSegment(sketch, "E525", {"start": v(13.44, -16) * mm, "end": v(12.64, -16) * mm});
            skArc(sketch, "E526", {"start": v(13.44, -16) * mm, "mid": v(13.65, -16.09) * mm, "end": v(13.74, -16.3) * mm});
            skLineSegment(sketch, "E527", {"start": v(12.34, -18.7) * mm, "end": v(12.34, -16.3) * mm});
            skLineSegment(sketch, "E528", {"start": v(13.74, -16.3) * mm, "end": v(13.74, -18.7) * mm});
            skArc(sketch, "E529", {"start": v(13.14, -17.5) * mm, "mid": v(13.04, -17.4) * mm, "end": v(12.94, -17.5) * mm});
            skArc(sketch, "E530", {"start": v(12.94, -17.5) * mm, "mid": v(13.04, -17.6) * mm, "end": v(13.14, -17.5) * mm});
            skArc(sketch, "E531", {"start": v(12.34, -18.7) * mm, "mid": v(12.43, -18.91) * mm, "end": v(12.64, -19) * mm});
            skArc(sketch, "E532", {"start": v(13.44, -19) * mm, "mid": v(13.65, -18.91) * mm, "end": v(13.74, -18.7) * mm});
            skLineSegment(sketch, "E533", {"start": v(12.64, -19) * mm, "end": v(13.44, -19) * mm});
            skLineSegment(sketch, "E534", {"start": v(12.54, -12.75) * mm, "end": v(13.54, -12.75) * mm});
            skLineSegment(sketch, "E535", {"start": v(13.54, -12.75) * mm, "end": v(13.54, -13.75) * mm});
            skLineSegment(sketch, "E536", {"start": v(13.54, -13.75) * mm, "end": v(12.54, -13.75) * mm});
            skLineSegment(sketch, "E537", {"start": v(12.54, -13.75) * mm, "end": v(12.54, -12.75) * mm});
            skLineSegment(sketch, "E538", {"start": v(12.54, -14.25) * mm, "end": v(13.54, -14.25) * mm});
            skLineSegment(sketch, "E539", {"start": v(13.54, -14.25) * mm, "end": v(13.54, -15.25) * mm});
            skLineSegment(sketch, "E540", {"start": v(13.54, -15.25) * mm, "end": v(12.54, -15.25) * mm});
            skLineSegment(sketch, "E541", {"start": v(12.54, -15.25) * mm, "end": v(12.54, -14.25) * mm});
            skArc(sketch, "E542", {"start": v(12.64, -12.5) * mm, "mid": v(12.43, -12.59) * mm, "end": v(12.34, -12.8) * mm});
            skLineSegment(sketch, "E543", {"start": v(13.44, -12.5) * mm, "end": v(12.64, -12.5) * mm});
            skArc(sketch, "E544", {"start": v(13.44, -12.5) * mm, "mid": v(13.65, -12.59) * mm, "end": v(13.74, -12.8) * mm});
            skLineSegment(sketch, "E545", {"start": v(12.34, -15.2) * mm, "end": v(12.34, -12.8) * mm});
            skLineSegment(sketch, "E546", {"start": v(13.74, -12.8) * mm, "end": v(13.74, -15.2) * mm});
            skArc(sketch, "E547", {"start": v(13.14, -14) * mm, "mid": v(13.04, -13.9) * mm, "end": v(12.94, -14) * mm});
            skArc(sketch, "E548", {"start": v(12.94, -14) * mm, "mid": v(13.04, -14.1) * mm, "end": v(13.14, -14) * mm});
            skArc(sketch, "E549", {"start": v(12.34, -15.2) * mm, "mid": v(12.43, -15.41) * mm, "end": v(12.64, -15.5) * mm});
            skArc(sketch, "E550", {"start": v(13.44, -15.5) * mm, "mid": v(13.65, -15.41) * mm, "end": v(13.74, -15.2) * mm});
            skLineSegment(sketch, "E551", {"start": v(12.64, -15.5) * mm, "end": v(13.44, -15.5) * mm});
            skLineSegment(sketch, "E552", {"start": v(-2.96, -4.75) * mm, "end": v(-1.96, -4.75) * mm});
            skLineSegment(sketch, "E553", {"start": v(-1.96, -4.75) * mm, "end": v(-1.96, -5.75) * mm});
            skLineSegment(sketch, "E554", {"start": v(-1.96, -5.75) * mm, "end": v(-2.96, -5.75) * mm});
            skLineSegment(sketch, "E555", {"start": v(-2.96, -5.75) * mm, "end": v(-2.96, -4.75) * mm});
            skLineSegment(sketch, "E556", {"start": v(-2.96, -6.25) * mm, "end": v(-1.96, -6.25) * mm});
            skLineSegment(sketch, "E557", {"start": v(-1.96, -6.25) * mm, "end": v(-1.96, -7.25) * mm});
            skLineSegment(sketch, "E558", {"start": v(-1.96, -7.25) * mm, "end": v(-2.96, -7.25) * mm});
            skLineSegment(sketch, "E559", {"start": v(-2.96, -7.25) * mm, "end": v(-2.96, -6.25) * mm});
            skArc(sketch, "E560", {"start": v(-2.86, -4.5) * mm, "mid": v(-3.07, -4.59) * mm, "end": v(-3.16, -4.8) * mm});
            skLineSegment(sketch, "E561", {"start": v(-2.06, -4.5) * mm, "end": v(-2.86, -4.5) * mm});
            skArc(sketch, "E562", {"start": v(-2.06, -4.5) * mm, "mid": v(-1.85, -4.59) * mm, "end": v(-1.76, -4.8) * mm});
            skLineSegment(sketch, "E563", {"start": v(-3.16, -7.2) * mm, "end": v(-3.16, -4.8) * mm});
            skLineSegment(sketch, "E564", {"start": v(-1.76, -4.8) * mm, "end": v(-1.76, -7.2) * mm});
            skArc(sketch, "E565", {"start": v(-2.36, -6) * mm, "mid": v(-2.46, -5.9) * mm, "end": v(-2.56, -6) * mm});
            skArc(sketch, "E566", {"start": v(-2.56, -6) * mm, "mid": v(-2.46, -6.1) * mm, "end": v(-2.36, -6) * mm});
            skArc(sketch, "E567", {"start": v(-3.16, -7.2) * mm, "mid": v(-3.07, -7.41) * mm, "end": v(-2.86, -7.5) * mm});
            skArc(sketch, "E568", {"start": v(-2.06, -7.5) * mm, "mid": v(-1.85, -7.41) * mm, "end": v(-1.76, -7.2) * mm});
            skLineSegment(sketch, "E569", {"start": v(-2.86, -7.5) * mm, "end": v(-2.06, -7.5) * mm});
            skLineSegment(sketch, "E570", {"start": v(-12.21, -25) * mm, "end": v(-12.21, -26) * mm});
            skLineSegment(sketch, "E571", {"start": v(-12.21, -26) * mm, "end": v(-13.21, -26) * mm});
            skLineSegment(sketch, "E572", {"start": v(-13.21, -26) * mm, "end": v(-13.21, -25) * mm});
            skLineSegment(sketch, "E573", {"start": v(-13.21, -25) * mm, "end": v(-12.21, -25) * mm});
            skLineSegment(sketch, "E574", {"start": v(-13.71, -25) * mm, "end": v(-13.71, -26) * mm});
            skLineSegment(sketch, "E575", {"start": v(-13.71, -26) * mm, "end": v(-14.71, -26) * mm});
            skLineSegment(sketch, "E576", {"start": v(-14.71, -26) * mm, "end": v(-14.71, -25) * mm});
            skLineSegment(sketch, "E577", {"start": v(-14.71, -25) * mm, "end": v(-13.71, -25) * mm});
            skArc(sketch, "E578", {"start": v(-11.96, -25.1) * mm, "mid": v(-12.05, -24.89) * mm, "end": v(-12.26, -24.8) * mm});
            skLineSegment(sketch, "E579", {"start": v(-11.96, -25.9) * mm, "end": v(-11.96, -25.1) * mm});
            skArc(sketch, "E580", {"start": v(-11.96, -25.9) * mm, "mid": v(-12.05, -26.11) * mm, "end": v(-12.26, -26.2) * mm});
            skLineSegment(sketch, "E581", {"start": v(-14.66, -24.8) * mm, "end": v(-12.26, -24.8) * mm});
            skLineSegment(sketch, "E582", {"start": v(-12.26, -26.2) * mm, "end": v(-14.66, -26.2) * mm});
            skArc(sketch, "E583", {"start": v(-13.36, -25.5) * mm, "mid": v(-13.46, -25.4) * mm, "end": v(-13.56, -25.5) * mm});
            skArc(sketch, "E584", {"start": v(-13.56, -25.5) * mm, "mid": v(-13.46, -25.6) * mm, "end": v(-13.36, -25.5) * mm});
            skArc(sketch, "E585", {"start": v(-14.66, -24.8) * mm, "mid": v(-14.87, -24.89) * mm, "end": v(-14.96, -25.1) * mm});
            skArc(sketch, "E586", {"start": v(-14.96, -25.9) * mm, "mid": v(-14.87, -26.11) * mm, "end": v(-14.66, -26.2) * mm});
            skLineSegment(sketch, "E587", {"start": v(-14.96, -25.1) * mm, "end": v(-14.96, -25.9) * mm});
            skLineSegment(sketch, "E588", {"start": v(-0.46, -7.25) * mm, "end": v(-1.46, -7.25) * mm});
            skLineSegment(sketch, "E589", {"start": v(-1.46, -7.25) * mm, "end": v(-1.46, -6.25) * mm});
            skLineSegment(sketch, "E590", {"start": v(-1.46, -6.25) * mm, "end": v(-0.46, -6.25) * mm});
            skLineSegment(sketch, "E591", {"start": v(-0.46, -6.25) * mm, "end": v(-0.46, -7.25) * mm});
            skLineSegment(sketch, "E592", {"start": v(-0.46, -5.75) * mm, "end": v(-1.46, -5.75) * mm});
            skLineSegment(sketch, "E593", {"start": v(-1.46, -5.75) * mm, "end": v(-1.46, -4.75) * mm});
            skLineSegment(sketch, "E594", {"start": v(-1.46, -4.75) * mm, "end": v(-0.46, -4.75) * mm});
            skLineSegment(sketch, "E595", {"start": v(-0.46, -4.75) * mm, "end": v(-0.46, -5.75) * mm});
            skArc(sketch, "E596", {"start": v(-0.56, -7.5) * mm, "mid": v(-0.35, -7.41) * mm, "end": v(-0.26, -7.2) * mm});
            skLineSegment(sketch, "E597", {"start": v(-1.36, -7.5) * mm, "end": v(-0.56, -7.5) * mm});
            skArc(sketch, "E598", {"start": v(-1.36, -7.5) * mm, "mid": v(-1.57, -7.41) * mm, "end": v(-1.66, -7.2) * mm});
            skLineSegment(sketch, "E599", {"start": v(-0.26, -4.8) * mm, "end": v(-0.26, -7.2) * mm});
            skLineSegment(sketch, "E600", {"start": v(-1.66, -7.2) * mm, "end": v(-1.66, -4.8) * mm});
            skArc(sketch, "E601", {"start": v(-0.86, -6) * mm, "mid": v(-0.96, -5.9) * mm, "end": v(-1.06, -6) * mm});
            skArc(sketch, "E602", {"start": v(-1.06, -6) * mm, "mid": v(-0.96, -6.1) * mm, "end": v(-0.86, -6) * mm});
            skArc(sketch, "E603", {"start": v(-0.26, -4.8) * mm, "mid": v(-0.35, -4.59) * mm, "end": v(-0.56, -4.5) * mm});
            skArc(sketch, "E604", {"start": v(-1.36, -4.5) * mm, "mid": v(-1.57, -4.59) * mm, "end": v(-1.66, -4.8) * mm});
            skLineSegment(sketch, "E605", {"start": v(-0.56, -4.5) * mm, "end": v(-1.36, -4.5) * mm});
            skLineSegment(sketch, "E606", {"start": v(-2.96, -15.25) * mm, "end": v(-1.96, -15.25) * mm});
            skLineSegment(sketch, "E607", {"start": v(-1.96, -15.25) * mm, "end": v(-1.96, -16.25) * mm});
            skLineSegment(sketch, "E608", {"start": v(-1.96, -16.25) * mm, "end": v(-2.96, -16.25) * mm});
            skLineSegment(sketch, "E609", {"start": v(-2.96, -16.25) * mm, "end": v(-2.96, -15.25) * mm});
            skLineSegment(sketch, "E610", {"start": v(-2.96, -16.75) * mm, "end": v(-1.96, -16.75) * mm});
            skLineSegment(sketch, "E611", {"start": v(-1.96, -16.75) * mm, "end": v(-1.96, -17.75) * mm});
            skLineSegment(sketch, "E612", {"start": v(-1.96, -17.75) * mm, "end": v(-2.96, -17.75) * mm});
            skLineSegment(sketch, "E613", {"start": v(-2.96, -17.75) * mm, "end": v(-2.96, -16.75) * mm});
            skArc(sketch, "E614", {"start": v(-2.86, -15) * mm, "mid": v(-3.07, -15.09) * mm, "end": v(-3.16, -15.3) * mm});
            skLineSegment(sketch, "E615", {"start": v(-2.06, -15) * mm, "end": v(-2.86, -15) * mm});
            skArc(sketch, "E616", {"start": v(-2.06, -15) * mm, "mid": v(-1.85, -15.09) * mm, "end": v(-1.76, -15.3) * mm});
            skLineSegment(sketch, "E617", {"start": v(-3.16, -17.7) * mm, "end": v(-3.16, -15.3) * mm});
            skLineSegment(sketch, "E618", {"start": v(-1.76, -15.3) * mm, "end": v(-1.76, -17.7) * mm});
            skArc(sketch, "E619", {"start": v(-2.36, -16.5) * mm, "mid": v(-2.46, -16.4) * mm, "end": v(-2.56, -16.5) * mm});
            skArc(sketch, "E620", {"start": v(-2.56, -16.5) * mm, "mid": v(-2.46, -16.6) * mm, "end": v(-2.36, -16.5) * mm});
            skArc(sketch, "E621", {"start": v(-3.16, -17.7) * mm, "mid": v(-3.07, -17.91) * mm, "end": v(-2.86, -18) * mm});
            skArc(sketch, "E622", {"start": v(-2.06, -18) * mm, "mid": v(-1.85, -17.91) * mm, "end": v(-1.76, -17.7) * mm});
            skLineSegment(sketch, "E623", {"start": v(-2.86, -18) * mm, "end": v(-2.06, -18) * mm});
            skLineSegment(sketch, "E624", {"start": v(-11.21, -20) * mm, "end": v(-11.21, -21) * mm});
            skLineSegment(sketch, "E625", {"start": v(-11.21, -21) * mm, "end": v(-12.21, -21) * mm});
            skLineSegment(sketch, "E626", {"start": v(-12.21, -21) * mm, "end": v(-12.21, -20) * mm});
            skLineSegment(sketch, "E627", {"start": v(-12.21, -20) * mm, "end": v(-11.21, -20) * mm});
            skLineSegment(sketch, "E628", {"start": v(-12.71, -20) * mm, "end": v(-12.71, -21) * mm});
            skLineSegment(sketch, "E629", {"start": v(-12.71, -21) * mm, "end": v(-13.71, -21) * mm});
            skLineSegment(sketch, "E630", {"start": v(-13.71, -21) * mm, "end": v(-13.71, -20) * mm});
            skLineSegment(sketch, "E631", {"start": v(-13.71, -20) * mm, "end": v(-12.71, -20) * mm});
            skArc(sketch, "E632", {"start": v(-10.96, -20.1) * mm, "mid": v(-11.05, -19.89) * mm, "end": v(-11.26, -19.8) * mm});
            skLineSegment(sketch, "E633", {"start": v(-10.96, -20.9) * mm, "end": v(-10.96, -20.1) * mm});
            skArc(sketch, "E634", {"start": v(-10.96, -20.9) * mm, "mid": v(-11.05, -21.11) * mm, "end": v(-11.26, -21.2) * mm});
            skLineSegment(sketch, "E635", {"start": v(-13.66, -19.8) * mm, "end": v(-11.26, -19.8) * mm});
            skLineSegment(sketch, "E636", {"start": v(-11.26, -21.2) * mm, "end": v(-13.66, -21.2) * mm});
            skArc(sketch, "E637", {"start": v(-12.36, -20.5) * mm, "mid": v(-12.46, -20.4) * mm, "end": v(-12.56, -20.5) * mm});
            skArc(sketch, "E638", {"start": v(-12.56, -20.5) * mm, "mid": v(-12.46, -20.6) * mm, "end": v(-12.36, -20.5) * mm});
            skArc(sketch, "E639", {"start": v(-13.66, -19.8) * mm, "mid": v(-13.87, -19.89) * mm, "end": v(-13.96, -20.1) * mm});
            skArc(sketch, "E640", {"start": v(-13.96, -20.9) * mm, "mid": v(-13.87, -21.11) * mm, "end": v(-13.66, -21.2) * mm});
            skLineSegment(sketch, "E641", {"start": v(-13.96, -20.1) * mm, "end": v(-13.96, -20.9) * mm});
            skLineSegment(sketch, "E642", {"start": v(15.29, -7.5) * mm, "end": v(15.29, -6.5) * mm});
            skLineSegment(sketch, "E643", {"start": v(15.29, -6.5) * mm, "end": v(16.29, -6.5) * mm});
            skLineSegment(sketch, "E644", {"start": v(16.29, -6.5) * mm, "end": v(16.29, -7.5) * mm});
            skLineSegment(sketch, "E645", {"start": v(16.29, -7.5) * mm, "end": v(15.29, -7.5) * mm});
            skLineSegment(sketch, "E646", {"start": v(16.79, -7.5) * mm, "end": v(16.79, -6.5) * mm});
            skLineSegment(sketch, "E647", {"start": v(16.79, -6.5) * mm, "end": v(17.79, -6.5) * mm});
            skLineSegment(sketch, "E648", {"start": v(17.79, -6.5) * mm, "end": v(17.79, -7.5) * mm});
            skLineSegment(sketch, "E649", {"start": v(17.79, -7.5) * mm, "end": v(16.79, -7.5) * mm});
            skArc(sketch, "E650", {"start": v(15.04, -7.4) * mm, "mid": v(15.13, -7.61) * mm, "end": v(15.34, -7.7) * mm});
            skLineSegment(sketch, "E651", {"start": v(15.04, -6.6) * mm, "end": v(15.04, -7.4) * mm});
            skArc(sketch, "E652", {"start": v(15.04, -6.6) * mm, "mid": v(15.13, -6.39) * mm, "end": v(15.34, -6.3) * mm});
            skLineSegment(sketch, "E653", {"start": v(17.74, -7.7) * mm, "end": v(15.34, -7.7) * mm});
            skLineSegment(sketch, "E654", {"start": v(15.34, -6.3) * mm, "end": v(17.74, -6.3) * mm});
            skArc(sketch, "E655", {"start": v(16.64, -7) * mm, "mid": v(16.54, -6.9) * mm, "end": v(16.44, -7) * mm});
            skArc(sketch, "E656", {"start": v(16.44, -7) * mm, "mid": v(16.54, -7.1) * mm, "end": v(16.64, -7) * mm});
            skArc(sketch, "E657", {"start": v(17.74, -7.7) * mm, "mid": v(17.95, -7.61) * mm, "end": v(18.04, -7.4) * mm});
            skArc(sketch, "E658", {"start": v(18.04, -6.6) * mm, "mid": v(17.95, -6.39) * mm, "end": v(17.74, -6.3) * mm});
            skLineSegment(sketch, "E659", {"start": v(18.04, -7.4) * mm, "end": v(18.04, -6.6) * mm});
            skLineSegment(sketch, "E660", {"start": v(2.54, -21.25) * mm, "end": v(1.54, -21.25) * mm});
            skLineSegment(sketch, "E661", {"start": v(1.54, -21.25) * mm, "end": v(1.54, -20.25) * mm});
            skLineSegment(sketch, "E662", {"start": v(1.54, -20.25) * mm, "end": v(2.54, -20.25) * mm});
            skLineSegment(sketch, "E663", {"start": v(2.54, -20.25) * mm, "end": v(2.54, -21.25) * mm});
            skLineSegment(sketch, "E664", {"start": v(2.54, -19.75) * mm, "end": v(1.54, -19.75) * mm});
            skLineSegment(sketch, "E665", {"start": v(1.54, -19.75) * mm, "end": v(1.54, -18.75) * mm});
            skLineSegment(sketch, "E666", {"start": v(1.54, -18.75) * mm, "end": v(2.54, -18.75) * mm});
            skLineSegment(sketch, "E667", {"start": v(2.54, -18.75) * mm, "end": v(2.54, -19.75) * mm});
            skArc(sketch, "E668", {"start": v(2.44, -21.5) * mm, "mid": v(2.65, -21.41) * mm, "end": v(2.74, -21.2) * mm});
            skLineSegment(sketch, "E669", {"start": v(1.64, -21.5) * mm, "end": v(2.44, -21.5) * mm});
            skArc(sketch, "E670", {"start": v(1.64, -21.5) * mm, "mid": v(1.43, -21.41) * mm, "end": v(1.34, -21.2) * mm});
            skLineSegment(sketch, "E671", {"start": v(2.74, -18.8) * mm, "end": v(2.74, -21.2) * mm});
            skLineSegment(sketch, "E672", {"start": v(1.34, -21.2) * mm, "end": v(1.34, -18.8) * mm});
            skArc(sketch, "E673", {"start": v(2.14, -20) * mm, "mid": v(2.04, -19.9) * mm, "end": v(1.94, -20) * mm});
            skArc(sketch, "E674", {"start": v(1.94, -20) * mm, "mid": v(2.04, -20.1) * mm, "end": v(2.14, -20) * mm});
            skArc(sketch, "E675", {"start": v(2.74, -18.8) * mm, "mid": v(2.65, -18.59) * mm, "end": v(2.44, -18.5) * mm});
            skArc(sketch, "E676", {"start": v(1.64, -18.5) * mm, "mid": v(1.43, -18.59) * mm, "end": v(1.34, -18.8) * mm});
            skLineSegment(sketch, "E677", {"start": v(2.44, -18.5) * mm, "end": v(1.64, -18.5) * mm});
            skLineSegment(sketch, "E678", {"start": v(-1.46, -18.75) * mm, "end": v(-0.46, -18.75) * mm});
            skLineSegment(sketch, "E679", {"start": v(-0.46, -18.75) * mm, "end": v(-0.46, -19.75) * mm});
            skLineSegment(sketch, "E680", {"start": v(-0.46, -19.75) * mm, "end": v(-1.46, -19.75) * mm});
            skLineSegment(sketch, "E681", {"start": v(-1.46, -19.75) * mm, "end": v(-1.46, -18.75) * mm});
            skLineSegment(sketch, "E682", {"start": v(-1.46, -20.25) * mm, "end": v(-0.46, -20.25) * mm});
            skLineSegment(sketch, "E683", {"start": v(-0.46, -20.25) * mm, "end": v(-0.46, -21.25) * mm});
            skLineSegment(sketch, "E684", {"start": v(-0.46, -21.25) * mm, "end": v(-1.46, -21.25) * mm});
            skLineSegment(sketch, "E685", {"start": v(-1.46, -21.25) * mm, "end": v(-1.46, -20.25) * mm});
            skArc(sketch, "E686", {"start": v(-1.36, -18.5) * mm, "mid": v(-1.57, -18.59) * mm, "end": v(-1.66, -18.8) * mm});
            skLineSegment(sketch, "E687", {"start": v(-0.56, -18.5) * mm, "end": v(-1.36, -18.5) * mm});
            skArc(sketch, "E688", {"start": v(-0.56, -18.5) * mm, "mid": v(-0.35, -18.59) * mm, "end": v(-0.26, -18.8) * mm});
            skLineSegment(sketch, "E689", {"start": v(-1.66, -21.2) * mm, "end": v(-1.66, -18.8) * mm});
            skLineSegment(sketch, "E690", {"start": v(-0.26, -18.8) * mm, "end": v(-0.26, -21.2) * mm});
            skArc(sketch, "E691", {"start": v(-0.86, -20) * mm, "mid": v(-0.96, -19.9) * mm, "end": v(-1.06, -20) * mm});
            skArc(sketch, "E692", {"start": v(-1.06, -20) * mm, "mid": v(-0.96, -20.1) * mm, "end": v(-0.86, -20) * mm});
            skArc(sketch, "E693", {"start": v(-1.66, -21.2) * mm, "mid": v(-1.57, -21.41) * mm, "end": v(-1.36, -21.5) * mm});
            skArc(sketch, "E694", {"start": v(-0.56, -21.5) * mm, "mid": v(-0.35, -21.41) * mm, "end": v(-0.26, -21.2) * mm});
            skLineSegment(sketch, "E695", {"start": v(-1.36, -21.5) * mm, "end": v(-0.56, -21.5) * mm});
            skLineSegment(sketch, "E696", {"start": v(-12.21, -28) * mm, "end": v(-12.21, -29) * mm});
            skLineSegment(sketch, "E697", {"start": v(-12.21, -29) * mm, "end": v(-13.21, -29) * mm});
            skLineSegment(sketch, "E698", {"start": v(-13.21, -29) * mm, "end": v(-13.21, -28) * mm});
            skLineSegment(sketch, "E699", {"start": v(-13.21, -28) * mm, "end": v(-12.21, -28) * mm});
            skLineSegment(sketch, "E700", {"start": v(-13.71, -28) * mm, "end": v(-13.71, -29) * mm});
            skLineSegment(sketch, "E701", {"start": v(-13.71, -29) * mm, "end": v(-14.71, -29) * mm});
            skLineSegment(sketch, "E702", {"start": v(-14.71, -29) * mm, "end": v(-14.71, -28) * mm});
            skLineSegment(sketch, "E703", {"start": v(-14.71, -28) * mm, "end": v(-13.71, -28) * mm});
            skArc(sketch, "E704", {"start": v(-11.96, -28.1) * mm, "mid": v(-12.05, -27.89) * mm, "end": v(-12.26, -27.8) * mm});
            skLineSegment(sketch, "E705", {"start": v(-11.96, -28.9) * mm, "end": v(-11.96, -28.1) * mm});
            skArc(sketch, "E706", {"start": v(-11.96, -28.9) * mm, "mid": v(-12.05, -29.11) * mm, "end": v(-12.26, -29.2) * mm});
            skLineSegment(sketch, "E707", {"start": v(-14.66, -27.8) * mm, "end": v(-12.26, -27.8) * mm});
            skLineSegment(sketch, "E708", {"start": v(-12.26, -29.2) * mm, "end": v(-14.66, -29.2) * mm});
            skArc(sketch, "E709", {"start": v(-13.36, -28.5) * mm, "mid": v(-13.46, -28.4) * mm, "end": v(-13.56, -28.5) * mm});
            skArc(sketch, "E710", {"start": v(-13.56, -28.5) * mm, "mid": v(-13.46, -28.6) * mm, "end": v(-13.36, -28.5) * mm});
            skArc(sketch, "E711", {"start": v(-14.66, -27.8) * mm, "mid": v(-14.87, -27.89) * mm, "end": v(-14.96, -28.1) * mm});
            skArc(sketch, "E712", {"start": v(-14.96, -28.9) * mm, "mid": v(-14.87, -29.11) * mm, "end": v(-14.66, -29.2) * mm});
            skLineSegment(sketch, "E713", {"start": v(-14.96, -28.1) * mm, "end": v(-14.96, -28.9) * mm});
            skLineSegment(sketch, "E714", {"start": v(13.54, -8.25) * mm, "end": v(12.54, -8.25) * mm});
            skLineSegment(sketch, "E715", {"start": v(12.54, -8.25) * mm, "end": v(12.54, -7.25) * mm});
            skLineSegment(sketch, "E716", {"start": v(12.54, -7.25) * mm, "end": v(13.54, -7.25) * mm});
            skLineSegment(sketch, "E717", {"start": v(13.54, -7.25) * mm, "end": v(13.54, -8.25) * mm});
            skLineSegment(sketch, "E718", {"start": v(13.54, -6.75) * mm, "end": v(12.54, -6.75) * mm});
            skLineSegment(sketch, "E719", {"start": v(12.54, -6.75) * mm, "end": v(12.54, -5.75) * mm});
            skLineSegment(sketch, "E720", {"start": v(12.54, -5.75) * mm, "end": v(13.54, -5.75) * mm});
            skLineSegment(sketch, "E721", {"start": v(13.54, -5.75) * mm, "end": v(13.54, -6.75) * mm});
            skArc(sketch, "E722", {"start": v(13.44, -8.5) * mm, "mid": v(13.65, -8.41) * mm, "end": v(13.74, -8.2) * mm});
            skLineSegment(sketch, "E723", {"start": v(12.64, -8.5) * mm, "end": v(13.44, -8.5) * mm});
            skArc(sketch, "E724", {"start": v(12.64, -8.5) * mm, "mid": v(12.43, -8.41) * mm, "end": v(12.34, -8.2) * mm});
            skLineSegment(sketch, "E725", {"start": v(13.74, -5.8) * mm, "end": v(13.74, -8.2) * mm});
            skLineSegment(sketch, "E726", {"start": v(12.34, -8.2) * mm, "end": v(12.34, -5.8) * mm});
            skArc(sketch, "E727", {"start": v(13.14, -7) * mm, "mid": v(13.04, -6.9) * mm, "end": v(12.94, -7) * mm});
            skArc(sketch, "E728", {"start": v(12.94, -7) * mm, "mid": v(13.04, -7.1) * mm, "end": v(13.14, -7) * mm});
            skArc(sketch, "E729", {"start": v(13.74, -5.8) * mm, "mid": v(13.65, -5.59) * mm, "end": v(13.44, -5.5) * mm});
            skArc(sketch, "E730", {"start": v(12.64, -5.5) * mm, "mid": v(12.43, -5.59) * mm, "end": v(12.34, -5.8) * mm});
            skLineSegment(sketch, "E731", {"start": v(13.44, -5.5) * mm, "end": v(12.64, -5.5) * mm});
            skLineSegment(sketch, "E732", {"start": v(-2.96, -18.75) * mm, "end": v(-1.96, -18.75) * mm});
            skLineSegment(sketch, "E733", {"start": v(-1.96, -18.75) * mm, "end": v(-1.96, -19.75) * mm});
            skLineSegment(sketch, "E734", {"start": v(-1.96, -19.75) * mm, "end": v(-2.96, -19.75) * mm});
            skLineSegment(sketch, "E735", {"start": v(-2.96, -19.75) * mm, "end": v(-2.96, -18.75) * mm});
            skLineSegment(sketch, "E736", {"start": v(-2.96, -20.25) * mm, "end": v(-1.96, -20.25) * mm});
            skLineSegment(sketch, "E737", {"start": v(-1.96, -20.25) * mm, "end": v(-1.96, -21.25) * mm});
            skLineSegment(sketch, "E738", {"start": v(-1.96, -21.25) * mm, "end": v(-2.96, -21.25) * mm});
            skLineSegment(sketch, "E739", {"start": v(-2.96, -21.25) * mm, "end": v(-2.96, -20.25) * mm});
            skArc(sketch, "E740", {"start": v(-2.86, -18.5) * mm, "mid": v(-3.07, -18.59) * mm, "end": v(-3.16, -18.8) * mm});
            skLineSegment(sketch, "E741", {"start": v(-2.06, -18.5) * mm, "end": v(-2.86, -18.5) * mm});
            skArc(sketch, "E742", {"start": v(-2.06, -18.5) * mm, "mid": v(-1.85, -18.59) * mm, "end": v(-1.76, -18.8) * mm});
            skLineSegment(sketch, "E743", {"start": v(-3.16, -21.2) * mm, "end": v(-3.16, -18.8) * mm});
            skLineSegment(sketch, "E744", {"start": v(-1.76, -18.8) * mm, "end": v(-1.76, -21.2) * mm});
            skArc(sketch, "E745", {"start": v(-2.36, -20) * mm, "mid": v(-2.46, -19.9) * mm, "end": v(-2.56, -20) * mm});
            skArc(sketch, "E746", {"start": v(-2.56, -20) * mm, "mid": v(-2.46, -20.1) * mm, "end": v(-2.36, -20) * mm});
            skArc(sketch, "E747", {"start": v(-3.16, -21.2) * mm, "mid": v(-3.07, -21.41) * mm, "end": v(-2.86, -21.5) * mm});
            skArc(sketch, "E748", {"start": v(-2.06, -21.5) * mm, "mid": v(-1.85, -21.41) * mm, "end": v(-1.76, -21.2) * mm});
            skLineSegment(sketch, "E749", {"start": v(-2.86, -21.5) * mm, "end": v(-2.06, -21.5) * mm});
            skLineSegment(sketch, "E750", {"start": v(19.29, -7.5) * mm, "end": v(19.29, -6.5) * mm});
            skLineSegment(sketch, "E751", {"start": v(19.29, -6.5) * mm, "end": v(20.29, -6.5) * mm});
            skLineSegment(sketch, "E752", {"start": v(20.29, -6.5) * mm, "end": v(20.29, -7.5) * mm});
            skLineSegment(sketch, "E753", {"start": v(20.29, -7.5) * mm, "end": v(19.29, -7.5) * mm});
            skLineSegment(sketch, "E754", {"start": v(20.79, -7.5) * mm, "end": v(20.79, -6.5) * mm});
            skLineSegment(sketch, "E755", {"start": v(20.79, -6.5) * mm, "end": v(21.79, -6.5) * mm});
            skLineSegment(sketch, "E756", {"start": v(21.79, -6.5) * mm, "end": v(21.79, -7.5) * mm});
            skLineSegment(sketch, "E757", {"start": v(21.79, -7.5) * mm, "end": v(20.79, -7.5) * mm});
            skArc(sketch, "E758", {"start": v(19.04, -7.4) * mm, "mid": v(19.13, -7.61) * mm, "end": v(19.34, -7.7) * mm});
            skLineSegment(sketch, "E759", {"start": v(19.04, -6.6) * mm, "end": v(19.04, -7.4) * mm});
            skArc(sketch, "E760", {"start": v(19.04, -6.6) * mm, "mid": v(19.13, -6.39) * mm, "end": v(19.34, -6.3) * mm});
            skLineSegment(sketch, "E761", {"start": v(21.74, -7.7) * mm, "end": v(19.34, -7.7) * mm});
            skLineSegment(sketch, "E762", {"start": v(19.34, -6.3) * mm, "end": v(21.74, -6.3) * mm});
            skArc(sketch, "E763", {"start": v(20.64, -7) * mm, "mid": v(20.54, -6.9) * mm, "end": v(20.44, -7) * mm});
            skArc(sketch, "E764", {"start": v(20.44, -7) * mm, "mid": v(20.54, -7.1) * mm, "end": v(20.64, -7) * mm});
            skArc(sketch, "E765", {"start": v(21.74, -7.7) * mm, "mid": v(21.95, -7.61) * mm, "end": v(22.04, -7.4) * mm});
            skArc(sketch, "E766", {"start": v(22.04, -6.6) * mm, "mid": v(21.95, -6.39) * mm, "end": v(21.74, -6.3) * mm});
            skLineSegment(sketch, "E767", {"start": v(22.04, -7.4) * mm, "end": v(22.04, -6.6) * mm});
            skLineSegment(sketch, "E768", {"start": v(14.94, 6.3) * mm, "end": v(14.94, 5.7) * mm});
            skArc(sketch, "E769", {"start": v(14.94, 5.7) * mm, "mid": v(15.54, 5.1) * mm, "end": v(16.14, 5.7) * mm});
            skLineSegment(sketch, "E770", {"start": v(16.14, 5.7) * mm, "end": v(16.14, 6.3) * mm});
            skArc(sketch, "E771", {"start": v(16.14, 6.3) * mm, "mid": v(15.54, 6.9) * mm, "end": v(14.94, 6.3) * mm});
            skLineSegment(sketch, "E772", {"start": v(17.48, 6.3) * mm, "end": v(17.48, 5.7) * mm});
            skArc(sketch, "E773", {"start": v(17.48, 5.7) * mm, "mid": v(18.08, 5.1) * mm, "end": v(18.68, 5.7) * mm});
            skLineSegment(sketch, "E774", {"start": v(18.68, 5.7) * mm, "end": v(18.68, 6.3) * mm});
            skArc(sketch, "E775", {"start": v(18.68, 6.3) * mm, "mid": v(18.08, 6.9) * mm, "end": v(17.48, 6.3) * mm});
            skLineSegment(sketch, "E776", {"start": v(12.4, 6.3) * mm, "end": v(12.4, 5.7) * mm});
            skArc(sketch, "E777", {"start": v(12.4, 5.7) * mm, "mid": v(13, 5.1) * mm, "end": v(13.6, 5.7) * mm});
            skLineSegment(sketch, "E778", {"start": v(13.6, 5.7) * mm, "end": v(13.6, 6.3) * mm});
            skArc(sketch, "E779", {"start": v(13.6, 6.3) * mm, "mid": v(13, 6.9) * mm, "end": v(12.4, 6.3) * mm});
            skLineSegment(sketch, "E780", {"start": v(16.54, 8.5) * mm, "end": v(14.54, 8.5) * mm});
            skLineSegment(sketch, "E781", {"start": v(16.54, 3.5) * mm, "end": v(14.54, 3.5) * mm});
            skArc(sketch, "E782", {"start": v(12.79, 7) * mm, "mid": v(13.5, 7.95) * mm, "end": v(14.54, 8.5) * mm});
            skArc(sketch, "E783", {"start": v(12.79, 5) * mm, "mid": v(13.47, 4.02) * mm, "end": v(14.54, 3.5) * mm});
            skArc(sketch, "E784", {"start": v(18.29, 7) * mm, "mid": v(17.61, 7.98) * mm, "end": v(16.54, 8.5) * mm});
            skArc(sketch, "E785", {"start": v(18.29, 5) * mm, "mid": v(17.58, 4.05) * mm, "end": v(16.54, 3.5) * mm});
            skLineSegment(sketch, "E786", {"start": v(15.04, 8.25) * mm, "end": v(15.04, 7.25) * mm});
            skLineSegment(sketch, "E787", {"start": v(15.04, 7.25) * mm, "end": v(14.29, 7.75) * mm});
            skLineSegment(sketch, "E788", {"start": v(14.29, 7.75) * mm, "end": v(15.04, 8.25) * mm});
            skLineSegment(sketch, "E789", {"start": v(14.29, 8.25) * mm, "end": v(14.29, 7.25) * mm});
            skLineSegment(sketch, "E790", {"start": v(14.29, 7.75) * mm, "end": v(14.04, 7.75) * mm});
            skLineSegment(sketch, "E791", {"start": v(14.04, 7.75) * mm, "end": v(13.29, 7) * mm});
            skLineSegment(sketch, "E792", {"start": v(16.04, 8.25) * mm, "end": v(16.04, 7.25) * mm});
            skLineSegment(sketch, "E793", {"start": v(16.04, 7.25) * mm, "end": v(16.79, 7.75) * mm});
            skLineSegment(sketch, "E794", {"start": v(16.79, 7.75) * mm, "end": v(16.04, 8.25) * mm});
            skLineSegment(sketch, "E795", {"start": v(16.79, 8.25) * mm, "end": v(16.79, 7.25) * mm});
            skLineSegment(sketch, "E796", {"start": v(16.79, 7.75) * mm, "end": v(17.04, 7.75) * mm});
            skLineSegment(sketch, "E797", {"start": v(17.04, 7.75) * mm, "end": v(17.79, 7) * mm});
            skLineSegment(sketch, "E798", {"start": v(16.04, 7.75) * mm, "end": v(15.04, 7.75) * mm});
            skLineSegment(sketch, "E799", {"start": v(15.54, 7.75) * mm, "end": v(15.54, 7) * mm});
            skLineSegment(sketch, "E800", {"start": v(5.14, -0.2) * mm, "end": v(5.14, -0.8) * mm});
            skArc(sketch, "E801", {"start": v(5.14, -0.8) * mm, "mid": v(4.54, -1.4) * mm, "end": v(3.94, -0.8) * mm});
            skLineSegment(sketch, "E802", {"start": v(3.94, -0.8) * mm, "end": v(3.94, -0.2) * mm});
            skArc(sketch, "E803", {"start": v(3.94, -0.2) * mm, "mid": v(4.54, 0.4) * mm, "end": v(5.14, -0.2) * mm});
            skLineSegment(sketch, "E804", {"start": v(2.6, -0.2) * mm, "end": v(2.6, -0.8) * mm});
            skArc(sketch, "E805", {"start": v(2.6, -0.8) * mm, "mid": v(2, -1.4) * mm, "end": v(1.4, -0.8) * mm});
            skLineSegment(sketch, "E806", {"start": v(1.4, -0.8) * mm, "end": v(1.4, -0.2) * mm});
            skArc(sketch, "E807", {"start": v(1.4, -0.2) * mm, "mid": v(2, 0.4) * mm, "end": v(2.6, -0.2) * mm});
            skLineSegment(sketch, "E808", {"start": v(7.68, -0.2) * mm, "end": v(7.68, -0.8) * mm});
            skArc(sketch, "E809", {"start": v(7.68, -0.8) * mm, "mid": v(7.08, -1.4) * mm, "end": v(6.48, -0.8) * mm});
            skLineSegment(sketch, "E810", {"start": v(6.48, -0.8) * mm, "end": v(6.48, -0.2) * mm});
            skArc(sketch, "E811", {"start": v(6.48, -0.2) * mm, "mid": v(7.08, 0.4) * mm, "end": v(7.68, -0.2) * mm});
            skLineSegment(sketch, "E812", {"start": v(3.54, 2) * mm, "end": v(5.54, 2) * mm});
            skLineSegment(sketch, "E813", {"start": v(3.54, -3) * mm, "end": v(5.54, -3) * mm});
            skArc(sketch, "E814", {"start": v(7.29, 0.5) * mm, "mid": v(6.58, 1.45) * mm, "end": v(5.54, 2) * mm});
            skArc(sketch, "E815", {"start": v(7.29, -1.5) * mm, "mid": v(6.61, -2.48) * mm, "end": v(5.54, -3) * mm});
            skArc(sketch, "E816", {"start": v(1.79, 0.5) * mm, "mid": v(2.47, 1.48) * mm, "end": v(3.54, 2) * mm});
            skArc(sketch, "E817", {"start": v(1.79, -1.5) * mm, "mid": v(2.5, -2.45) * mm, "end": v(3.54, -3) * mm});
            skLineSegment(sketch, "E818", {"start": v(5.04, 1.75) * mm, "end": v(5.04, 0.75) * mm});
            skLineSegment(sketch, "E819", {"start": v(5.04, 0.75) * mm, "end": v(5.79, 1.25) * mm});
            skLineSegment(sketch, "E820", {"start": v(5.79, 1.25) * mm, "end": v(5.04, 1.75) * mm});
            skLineSegment(sketch, "E821", {"start": v(5.79, 1.75) * mm, "end": v(5.79, 0.75) * mm});
            skLineSegment(sketch, "E822", {"start": v(5.79, 1.25) * mm, "end": v(6.04, 1.25) * mm});
            skLineSegment(sketch, "E823", {"start": v(6.04, 1.25) * mm, "end": v(6.79, 0.5) * mm});
            skLineSegment(sketch, "E824", {"start": v(4.04, 1.75) * mm, "end": v(4.04, 0.75) * mm});
            skLineSegment(sketch, "E825", {"start": v(4.04, 0.75) * mm, "end": v(3.29, 1.25) * mm});
            skLineSegment(sketch, "E826", {"start": v(3.29, 1.25) * mm, "end": v(4.04, 1.75) * mm});
            skLineSegment(sketch, "E827", {"start": v(3.29, 1.75) * mm, "end": v(3.29, 0.75) * mm});
            skLineSegment(sketch, "E828", {"start": v(3.29, 1.25) * mm, "end": v(3.04, 1.25) * mm});
            skLineSegment(sketch, "E829", {"start": v(3.04, 1.25) * mm, "end": v(2.29, 0.5) * mm});
            skLineSegment(sketch, "E830", {"start": v(4.04, 1.25) * mm, "end": v(5.04, 1.25) * mm});
            skLineSegment(sketch, "E831", {"start": v(4.54, 1.25) * mm, "end": v(4.54, 0.5) * mm});
            skLineSegment(sketch, "E832", {"start": v(-17.53, 15.78) * mm, "end": v(-17.53, 14.5) * mm});
            skLineSegment(sketch, "E833", {"start": v(-17.53, 14.5) * mm, "end": v(-18.3, 14.5) * mm});
            skLineSegment(sketch, "E834", {"start": v(-18.3, 14.5) * mm, "end": v(-18.3, 15.78) * mm});
            skLineSegment(sketch, "E835", {"start": v(-18.3, 15.78) * mm, "end": v(-17.53, 15.78) * mm});
            skLineSegment(sketch, "E836", {"start": v(-15.63, 15.78) * mm, "end": v(-15.63, 14.5) * mm});
            skLineSegment(sketch, "E837", {"start": v(-15.63, 14.5) * mm, "end": v(-16.39, 14.5) * mm});
            skLineSegment(sketch, "E838", {"start": v(-16.39, 14.5) * mm, "end": v(-16.39, 15.78) * mm});
            skLineSegment(sketch, "E839", {"start": v(-16.39, 15.78) * mm, "end": v(-15.63, 15.78) * mm});
            skLineSegment(sketch, "E840", {"start": v(-16.58, 13.5) * mm, "end": v(-16.58, 12.22) * mm});
            skLineSegment(sketch, "E841", {"start": v(-16.58, 12.22) * mm, "end": v(-17.34, 12.22) * mm});
            skLineSegment(sketch, "E842", {"start": v(-17.34, 12.22) * mm, "end": v(-17.34, 13.5) * mm});
            skLineSegment(sketch, "E843", {"start": v(-17.34, 13.5) * mm, "end": v(-16.58, 13.5) * mm});
            skArc(sketch, "E844", {"start": v(-16.71, 14) * mm, "mid": v(-16.96, 14.25) * mm, "end": v(-17.21, 14) * mm});
            skArc(sketch, "E845", {"start": v(-17.21, 14) * mm, "mid": v(-16.96, 13.75) * mm, "end": v(-16.71, 14) * mm});
            skLineSegment(sketch, "E846", {"start": v(-15.34, 12) * mm, "end": v(-18.59, 12) * mm});
            skLineSegment(sketch, "E847", {"start": v(-18.59, 12) * mm, "end": v(-18.59, 16) * mm});
            skLineSegment(sketch, "E848", {"start": v(-18.59, 16) * mm, "end": v(-15.59, 16) * mm});
            skLineSegment(sketch, "E849", {"start": v(-15.59, 16) * mm, "end": v(-15.34, 15.75) * mm});
            skLineSegment(sketch, "E850", {"start": v(-15.34, 15.75) * mm, "end": v(-15.34, 12) * mm});
            skLineSegment(sketch, "E851", {"start": v(24.76, 17.68) * mm, "end": v(26.03, 17.68) * mm});
            skLineSegment(sketch, "E852", {"start": v(26.03, 17.68) * mm, "end": v(26.03, 16.92) * mm});
            skLineSegment(sketch, "E853", {"start": v(26.03, 16.92) * mm, "end": v(24.76, 16.92) * mm});
            skLineSegment(sketch, "E854", {"start": v(24.76, 16.92) * mm, "end": v(24.76, 17.68) * mm});
            skLineSegment(sketch, "E855", {"start": v(24.76, 19.58) * mm, "end": v(26.03, 19.58) * mm});
            skLineSegment(sketch, "E856", {"start": v(26.03, 19.58) * mm, "end": v(26.03, 18.82) * mm});
            skLineSegment(sketch, "E857", {"start": v(26.03, 18.82) * mm, "end": v(24.76, 18.82) * mm});
            skLineSegment(sketch, "E858", {"start": v(24.76, 18.82) * mm, "end": v(24.76, 19.58) * mm});
            skLineSegment(sketch, "E859", {"start": v(27.05, 18.63) * mm, "end": v(28.32, 18.63) * mm});
            skLineSegment(sketch, "E860", {"start": v(28.32, 18.63) * mm, "end": v(28.32, 17.87) * mm});
            skLineSegment(sketch, "E861", {"start": v(28.32, 17.87) * mm, "end": v(27.05, 17.87) * mm});
            skLineSegment(sketch, "E862", {"start": v(27.05, 17.87) * mm, "end": v(27.05, 18.63) * mm});
            skArc(sketch, "E863", {"start": v(26.79, 18.25) * mm, "mid": v(26.54, 18.5) * mm, "end": v(26.29, 18.25) * mm});
            skArc(sketch, "E864", {"start": v(26.29, 18.25) * mm, "mid": v(26.54, 18) * mm, "end": v(26.79, 18.25) * mm});
            skLineSegment(sketch, "E865", {"start": v(28.54, 19.88) * mm, "end": v(28.54, 16.62) * mm});
            skLineSegment(sketch, "E866", {"start": v(28.54, 16.62) * mm, "end": v(24.54, 16.62) * mm});
            skLineSegment(sketch, "E867", {"start": v(24.54, 16.62) * mm, "end": v(24.54, 19.62) * mm});
            skLineSegment(sketch, "E868", {"start": v(24.54, 19.62) * mm, "end": v(24.79, 19.88) * mm});
            skLineSegment(sketch, "E869", {"start": v(24.79, 19.88) * mm, "end": v(28.54, 19.88) * mm});
            skLineSegment(sketch, "E870", {"start": v(-12.03, 17.78) * mm, "end": v(-12.03, 16.5) * mm});
            skLineSegment(sketch, "E871", {"start": v(-12.03, 16.5) * mm, "end": v(-12.8, 16.5) * mm});
            skLineSegment(sketch, "E872", {"start": v(-12.8, 16.5) * mm, "end": v(-12.8, 17.78) * mm});
            skLineSegment(sketch, "E873", {"start": v(-12.8, 17.78) * mm, "end": v(-12.03, 17.78) * mm});
            skLineSegment(sketch, "E874", {"start": v(-10.13, 17.78) * mm, "end": v(-10.13, 16.5) * mm});
            skLineSegment(sketch, "E875", {"start": v(-10.13, 16.5) * mm, "end": v(-10.89, 16.5) * mm});
            skLineSegment(sketch, "E876", {"start": v(-10.89, 16.5) * mm, "end": v(-10.89, 17.78) * mm});
            skLineSegment(sketch, "E877", {"start": v(-10.89, 17.78) * mm, "end": v(-10.13, 17.78) * mm});
            skLineSegment(sketch, "E878", {"start": v(-11.08, 15.5) * mm, "end": v(-11.08, 14.22) * mm});
            skLineSegment(sketch, "E879", {"start": v(-11.08, 14.22) * mm, "end": v(-11.84, 14.22) * mm});
            skLineSegment(sketch, "E880", {"start": v(-11.84, 14.22) * mm, "end": v(-11.84, 15.5) * mm});
            skLineSegment(sketch, "E881", {"start": v(-11.84, 15.5) * mm, "end": v(-11.08, 15.5) * mm});
            skArc(sketch, "E882", {"start": v(-11.21, 16) * mm, "mid": v(-11.46, 16.25) * mm, "end": v(-11.71, 16) * mm});
            skArc(sketch, "E883", {"start": v(-11.71, 16) * mm, "mid": v(-11.46, 15.75) * mm, "end": v(-11.21, 16) * mm});
            skLineSegment(sketch, "E884", {"start": v(-9.84, 14) * mm, "end": v(-13.09, 14) * mm});
            skLineSegment(sketch, "E885", {"start": v(-13.09, 14) * mm, "end": v(-13.09, 18) * mm});
            skLineSegment(sketch, "E886", {"start": v(-13.09, 18) * mm, "end": v(-10.09, 18) * mm});
            skLineSegment(sketch, "E887", {"start": v(-10.09, 18) * mm, "end": v(-9.84, 17.75) * mm});
            skLineSegment(sketch, "E888", {"start": v(-9.84, 17.75) * mm, "end": v(-9.84, 14) * mm});
            skLineSegment(sketch, "E889", {"start": v(-8.53, 17.78) * mm, "end": v(-8.53, 16.5) * mm});
            skLineSegment(sketch, "E890", {"start": v(-8.53, 16.5) * mm, "end": v(-9.3, 16.5) * mm});
            skLineSegment(sketch, "E891", {"start": v(-9.3, 16.5) * mm, "end": v(-9.3, 17.78) * mm});
            skLineSegment(sketch, "E892", {"start": v(-9.3, 17.78) * mm, "end": v(-8.53, 17.78) * mm});
            skLineSegment(sketch, "E893", {"start": v(-6.63, 17.78) * mm, "end": v(-6.63, 16.5) * mm});
            skLineSegment(sketch, "E894", {"start": v(-6.63, 16.5) * mm, "end": v(-7.39, 16.5) * mm});
            skLineSegment(sketch, "E895", {"start": v(-7.39, 16.5) * mm, "end": v(-7.39, 17.78) * mm});
            skLineSegment(sketch, "E896", {"start": v(-7.39, 17.78) * mm, "end": v(-6.63, 17.78) * mm});
            skLineSegment(sketch, "E897", {"start": v(-7.58, 15.5) * mm, "end": v(-7.58, 14.22) * mm});
            skLineSegment(sketch, "E898", {"start": v(-7.58, 14.22) * mm, "end": v(-8.34, 14.22) * mm});
            skLineSegment(sketch, "E899", {"start": v(-8.34, 14.22) * mm, "end": v(-8.34, 15.5) * mm});
            skLineSegment(sketch, "E900", {"start": v(-8.34, 15.5) * mm, "end": v(-7.58, 15.5) * mm});
            skArc(sketch, "E901", {"start": v(-7.71, 16) * mm, "mid": v(-7.96, 16.25) * mm, "end": v(-8.21, 16) * mm});
            skArc(sketch, "E902", {"start": v(-8.21, 16) * mm, "mid": v(-7.96, 15.75) * mm, "end": v(-7.71, 16) * mm});
            skLineSegment(sketch, "E903", {"start": v(-6.34, 14) * mm, "end": v(-9.59, 14) * mm});
            skLineSegment(sketch, "E904", {"start": v(-9.59, 14) * mm, "end": v(-9.59, 18) * mm});
            skLineSegment(sketch, "E905", {"start": v(-9.59, 18) * mm, "end": v(-6.59, 18) * mm});
            skLineSegment(sketch, "E906", {"start": v(-6.59, 18) * mm, "end": v(-6.34, 17.75) * mm});
            skLineSegment(sketch, "E907", {"start": v(-6.34, 17.75) * mm, "end": v(-6.34, 14) * mm});
            skLineSegment(sketch, "E908", {"start": v(-8.03, 30.78) * mm, "end": v(-8.03, 29.5) * mm});
            skLineSegment(sketch, "E909", {"start": v(-8.03, 29.5) * mm, "end": v(-8.8, 29.5) * mm});
            skLineSegment(sketch, "E910", {"start": v(-8.8, 29.5) * mm, "end": v(-8.8, 30.78) * mm});
            skLineSegment(sketch, "E911", {"start": v(-8.8, 30.78) * mm, "end": v(-8.03, 30.78) * mm});
            skLineSegment(sketch, "E912", {"start": v(-6.13, 30.78) * mm, "end": v(-6.13, 29.5) * mm});
            skLineSegment(sketch, "E913", {"start": v(-6.13, 29.5) * mm, "end": v(-6.89, 29.5) * mm});
            skLineSegment(sketch, "E914", {"start": v(-6.89, 29.5) * mm, "end": v(-6.89, 30.78) * mm});
            skLineSegment(sketch, "E915", {"start": v(-6.89, 30.78) * mm, "end": v(-6.13, 30.78) * mm});
            skLineSegment(sketch, "E916", {"start": v(-7.08, 28.5) * mm, "end": v(-7.08, 27.22) * mm});
            skLineSegment(sketch, "E917", {"start": v(-7.08, 27.22) * mm, "end": v(-7.84, 27.22) * mm});
            skLineSegment(sketch, "E918", {"start": v(-7.84, 27.22) * mm, "end": v(-7.84, 28.5) * mm});
            skLineSegment(sketch, "E919", {"start": v(-7.84, 28.5) * mm, "end": v(-7.08, 28.5) * mm});
            skArc(sketch, "E920", {"start": v(-7.21, 29) * mm, "mid": v(-7.46, 29.25) * mm, "end": v(-7.71, 29) * mm});
            skArc(sketch, "E921", {"start": v(-7.71, 29) * mm, "mid": v(-7.46, 28.75) * mm, "end": v(-7.21, 29) * mm});
            skLineSegment(sketch, "E922", {"start": v(-5.84, 27) * mm, "end": v(-9.09, 27) * mm});
            skLineSegment(sketch, "E923", {"start": v(-9.09, 27) * mm, "end": v(-9.09, 31) * mm});
            skLineSegment(sketch, "E924", {"start": v(-9.09, 31) * mm, "end": v(-6.09, 31) * mm});
            skLineSegment(sketch, "E925", {"start": v(-6.09, 31) * mm, "end": v(-5.84, 30.75) * mm});
            skLineSegment(sketch, "E926", {"start": v(-5.84, 30.75) * mm, "end": v(-5.84, 27) * mm});
            skLineSegment(sketch, "E927", {"start": v(1.97, 17.78) * mm, "end": v(1.97, 16.5) * mm});
            skLineSegment(sketch, "E928", {"start": v(1.97, 16.5) * mm, "end": v(1.2, 16.5) * mm});
            skLineSegment(sketch, "E929", {"start": v(1.2, 16.5) * mm, "end": v(1.2, 17.78) * mm});
            skLineSegment(sketch, "E930", {"start": v(1.2, 17.78) * mm, "end": v(1.97, 17.78) * mm});
            skLineSegment(sketch, "E931", {"start": v(3.87, 17.78) * mm, "end": v(3.87, 16.5) * mm});
            skLineSegment(sketch, "E932", {"start": v(3.87, 16.5) * mm, "end": v(3.11, 16.5) * mm});
            skLineSegment(sketch, "E933", {"start": v(3.11, 16.5) * mm, "end": v(3.11, 17.78) * mm});
            skLineSegment(sketch, "E934", {"start": v(3.11, 17.78) * mm, "end": v(3.87, 17.78) * mm});
            skLineSegment(sketch, "E935", {"start": v(2.92, 15.5) * mm, "end": v(2.92, 14.22) * mm});
            skLineSegment(sketch, "E936", {"start": v(2.92, 14.22) * mm, "end": v(2.16, 14.22) * mm});
            skLineSegment(sketch, "E937", {"start": v(2.16, 14.22) * mm, "end": v(2.16, 15.5) * mm});
            skLineSegment(sketch, "E938", {"start": v(2.16, 15.5) * mm, "end": v(2.92, 15.5) * mm});
            skArc(sketch, "E939", {"start": v(2.79, 16) * mm, "mid": v(2.54, 16.25) * mm, "end": v(2.29, 16) * mm});
            skArc(sketch, "E940", {"start": v(2.29, 16) * mm, "mid": v(2.54, 15.75) * mm, "end": v(2.79, 16) * mm});
            skLineSegment(sketch, "E941", {"start": v(4.16, 14) * mm, "end": v(0.91, 14) * mm});
            skLineSegment(sketch, "E942", {"start": v(0.91, 14) * mm, "end": v(0.91, 18) * mm});
            skLineSegment(sketch, "E943", {"start": v(0.91, 18) * mm, "end": v(3.91, 18) * mm});
            skLineSegment(sketch, "E944", {"start": v(3.91, 18) * mm, "end": v(4.16, 17.75) * mm});
            skLineSegment(sketch, "E945", {"start": v(4.16, 17.75) * mm, "end": v(4.16, 14) * mm});
            skLineSegment(sketch, "E946", {"start": v(-4.53, 30.78) * mm, "end": v(-4.53, 29.5) * mm});
            skLineSegment(sketch, "E947", {"start": v(-4.53, 29.5) * mm, "end": v(-5.3, 29.5) * mm});
            skLineSegment(sketch, "E948", {"start": v(-5.3, 29.5) * mm, "end": v(-5.3, 30.78) * mm});
            skLineSegment(sketch, "E949", {"start": v(-5.3, 30.78) * mm, "end": v(-4.53, 30.78) * mm});
            skLineSegment(sketch, "E950", {"start": v(-2.63, 30.78) * mm, "end": v(-2.63, 29.5) * mm});
            skLineSegment(sketch, "E951", {"start": v(-2.63, 29.5) * mm, "end": v(-3.39, 29.5) * mm});
            skLineSegment(sketch, "E952", {"start": v(-3.39, 29.5) * mm, "end": v(-3.39, 30.78) * mm});
            skLineSegment(sketch, "E953", {"start": v(-3.39, 30.78) * mm, "end": v(-2.63, 30.78) * mm});
            skLineSegment(sketch, "E954", {"start": v(-3.58, 28.5) * mm, "end": v(-3.58, 27.22) * mm});
            skLineSegment(sketch, "E955", {"start": v(-3.58, 27.22) * mm, "end": v(-4.34, 27.22) * mm});
            skLineSegment(sketch, "E956", {"start": v(-4.34, 27.22) * mm, "end": v(-4.34, 28.5) * mm});
            skLineSegment(sketch, "E957", {"start": v(-4.34, 28.5) * mm, "end": v(-3.58, 28.5) * mm});
            skArc(sketch, "E958", {"start": v(-3.71, 29) * mm, "mid": v(-3.96, 29.25) * mm, "end": v(-4.21, 29) * mm});
            skArc(sketch, "E959", {"start": v(-4.21, 29) * mm, "mid": v(-3.96, 28.75) * mm, "end": v(-3.71, 29) * mm});
            skLineSegment(sketch, "E960", {"start": v(-2.34, 27) * mm, "end": v(-5.59, 27) * mm});
            skLineSegment(sketch, "E961", {"start": v(-5.59, 27) * mm, "end": v(-5.59, 31) * mm});
            skLineSegment(sketch, "E962", {"start": v(-5.59, 31) * mm, "end": v(-2.59, 31) * mm});
            skLineSegment(sketch, "E963", {"start": v(-2.59, 31) * mm, "end": v(-2.34, 30.75) * mm});
            skLineSegment(sketch, "E964", {"start": v(-2.34, 30.75) * mm, "end": v(-2.34, 27) * mm});
            skLineSegment(sketch, "E965", {"start": v(-1.53, 17.78) * mm, "end": v(-1.53, 16.5) * mm});
            skLineSegment(sketch, "E966", {"start": v(-1.53, 16.5) * mm, "end": v(-2.3, 16.5) * mm});
            skLineSegment(sketch, "E967", {"start": v(-2.3, 16.5) * mm, "end": v(-2.3, 17.78) * mm});
            skLineSegment(sketch, "E968", {"start": v(-2.3, 17.78) * mm, "end": v(-1.53, 17.78) * mm});
            skLineSegment(sketch, "E969", {"start": v(0.37, 17.78) * mm, "end": v(0.37, 16.5) * mm});
            skLineSegment(sketch, "E970", {"start": v(0.37, 16.5) * mm, "end": v(-0.39, 16.5) * mm});
            skLineSegment(sketch, "E971", {"start": v(-0.39, 16.5) * mm, "end": v(-0.39, 17.78) * mm});
            skLineSegment(sketch, "E972", {"start": v(-0.39, 17.78) * mm, "end": v(0.37, 17.78) * mm});
            skLineSegment(sketch, "E973", {"start": v(-0.58, 15.5) * mm, "end": v(-0.58, 14.22) * mm});
            skLineSegment(sketch, "E974", {"start": v(-0.58, 14.22) * mm, "end": v(-1.34, 14.22) * mm});
            skLineSegment(sketch, "E975", {"start": v(-1.34, 14.22) * mm, "end": v(-1.34, 15.5) * mm});
            skLineSegment(sketch, "E976", {"start": v(-1.34, 15.5) * mm, "end": v(-0.58, 15.5) * mm});
            skArc(sketch, "E977", {"start": v(-0.71, 16) * mm, "mid": v(-0.96, 16.25) * mm, "end": v(-1.21, 16) * mm});
            skArc(sketch, "E978", {"start": v(-1.21, 16) * mm, "mid": v(-0.96, 15.75) * mm, "end": v(-0.71, 16) * mm});
            skLineSegment(sketch, "E979", {"start": v(0.66, 14) * mm, "end": v(-2.59, 14) * mm});
            skLineSegment(sketch, "E980", {"start": v(-2.59, 14) * mm, "end": v(-2.59, 18) * mm});
            skLineSegment(sketch, "E981", {"start": v(-2.59, 18) * mm, "end": v(0.41, 18) * mm});
            skLineSegment(sketch, "E982", {"start": v(0.41, 18) * mm, "end": v(0.66, 17.75) * mm});
            skLineSegment(sketch, "E983", {"start": v(0.66, 17.75) * mm, "end": v(0.66, 14) * mm});
            skLineSegment(sketch, "E984", {"start": v(-5.03, 17.78) * mm, "end": v(-5.03, 16.5) * mm});
            skLineSegment(sketch, "E985", {"start": v(-5.03, 16.5) * mm, "end": v(-5.8, 16.5) * mm});
            skLineSegment(sketch, "E986", {"start": v(-5.8, 16.5) * mm, "end": v(-5.8, 17.78) * mm});
            skLineSegment(sketch, "E987", {"start": v(-5.8, 17.78) * mm, "end": v(-5.03, 17.78) * mm});
            skLineSegment(sketch, "E988", {"start": v(-3.13, 17.78) * mm, "end": v(-3.13, 16.5) * mm});
            skLineSegment(sketch, "E989", {"start": v(-3.13, 16.5) * mm, "end": v(-3.89, 16.5) * mm});
            skLineSegment(sketch, "E990", {"start": v(-3.89, 16.5) * mm, "end": v(-3.89, 17.78) * mm});
            skLineSegment(sketch, "E991", {"start": v(-3.89, 17.78) * mm, "end": v(-3.13, 17.78) * mm});
            skLineSegment(sketch, "E992", {"start": v(-4.08, 15.5) * mm, "end": v(-4.08, 14.22) * mm});
            skLineSegment(sketch, "E993", {"start": v(-4.08, 14.22) * mm, "end": v(-4.84, 14.22) * mm});
            skLineSegment(sketch, "E994", {"start": v(-4.84, 14.22) * mm, "end": v(-4.84, 15.5) * mm});
            skLineSegment(sketch, "E995", {"start": v(-4.84, 15.5) * mm, "end": v(-4.08, 15.5) * mm});
            skArc(sketch, "E996", {"start": v(-4.21, 16) * mm, "mid": v(-4.46, 16.25) * mm, "end": v(-4.71, 16) * mm});
            skArc(sketch, "E997", {"start": v(-4.71, 16) * mm, "mid": v(-4.46, 15.75) * mm, "end": v(-4.21, 16) * mm});
            skLineSegment(sketch, "E998", {"start": v(-2.84, 14) * mm, "end": v(-6.09, 14) * mm});
            skLineSegment(sketch, "E999", {"start": v(-6.09, 14) * mm, "end": v(-6.09, 18) * mm});
            skLineSegment(sketch, "E1000", {"start": v(-6.09, 18) * mm, "end": v(-3.09, 18) * mm});
            skLineSegment(sketch, "E1001", {"start": v(-3.09, 18) * mm, "end": v(-2.84, 17.75) * mm});
            skLineSegment(sketch, "E1002", {"start": v(-2.84, 17.75) * mm, "end": v(-2.84, 14) * mm});
            skLineSegment(sketch, "E1003", {"start": v(-16.24, -7.57) * mm, "end": v(-14.97, -7.57) * mm});
            skLineSegment(sketch, "E1004", {"start": v(-14.97, -7.57) * mm, "end": v(-14.97, -8.33) * mm});
            skLineSegment(sketch, "E1005", {"start": v(-14.97, -8.33) * mm, "end": v(-16.24, -8.33) * mm});
            skLineSegment(sketch, "E1006", {"start": v(-16.24, -8.33) * mm, "end": v(-16.24, -7.57) * mm});
            skLineSegment(sketch, "E1007", {"start": v(-16.24, -5.67) * mm, "end": v(-14.97, -5.67) * mm});
            skLineSegment(sketch, "E1008", {"start": v(-14.97, -5.67) * mm, "end": v(-14.97, -6.43) * mm});
            skLineSegment(sketch, "E1009", {"start": v(-14.97, -6.43) * mm, "end": v(-16.24, -6.43) * mm});
            skLineSegment(sketch, "E1010", {"start": v(-16.24, -6.43) * mm, "end": v(-16.24, -5.67) * mm});
            skLineSegment(sketch, "E1011", {"start": v(-13.95, -6.62) * mm, "end": v(-12.68, -6.62) * mm});
            skLineSegment(sketch, "E1012", {"start": v(-12.68, -6.62) * mm, "end": v(-12.68, -7.38) * mm});
            skLineSegment(sketch, "E1013", {"start": v(-12.68, -7.38) * mm, "end": v(-13.95, -7.38) * mm});
            skLineSegment(sketch, "E1014", {"start": v(-13.95, -7.38) * mm, "end": v(-13.95, -6.62) * mm});
            skArc(sketch, "E1015", {"start": v(-14.21, -7) * mm, "mid": v(-14.46, -6.75) * mm, "end": v(-14.71, -7) * mm});
            skArc(sketch, "E1016", {"start": v(-14.71, -7) * mm, "mid": v(-14.46, -7.25) * mm, "end": v(-14.21, -7) * mm});
            skLineSegment(sketch, "E1017", {"start": v(-12.46, -5.38) * mm, "end": v(-12.46, -8.62) * mm});
            skLineSegment(sketch, "E1018", {"start": v(-12.46, -8.62) * mm, "end": v(-16.46, -8.62) * mm});
            skLineSegment(sketch, "E1019", {"start": v(-16.46, -8.62) * mm, "end": v(-16.46, -5.62) * mm});
            skLineSegment(sketch, "E1020", {"start": v(-16.46, -5.62) * mm, "end": v(-16.21, -5.38) * mm});
            skLineSegment(sketch, "E1021", {"start": v(-16.21, -5.38) * mm, "end": v(-12.46, -5.38) * mm});
            skLineSegment(sketch, "E1022", {"start": v(-10.8, 26.03) * mm, "end": v(-10.8, 27.56) * mm});
            skArc(sketch, "E1023", {"start": v(-10.8, 27.56) * mm, "mid": v(-10.56, 27.8) * mm, "end": v(-10.3, 27.56) * mm});
            skLineSegment(sketch, "E1024", {"start": v(-10.3, 27.56) * mm, "end": v(-10.3, 26.03) * mm});
            skArc(sketch, "E1025", {"start": v(-10.3, 26.03) * mm, "mid": v(-10.56, 25.78) * mm, "end": v(-10.8, 26.03) * mm});
            skLineSegment(sketch, "E1026", {"start": v(-12.08, 26.03) * mm, "end": v(-12.08, 27.56) * mm});
            skArc(sketch, "E1027", {"start": v(-12.08, 27.56) * mm, "mid": v(-11.83, 27.8) * mm, "end": v(-11.57, 27.56) * mm});
            skLineSegment(sketch, "E1028", {"start": v(-11.57, 27.56) * mm, "end": v(-11.57, 26.03) * mm});
            skArc(sketch, "E1029", {"start": v(-11.57, 26.03) * mm, "mid": v(-11.83, 25.78) * mm, "end": v(-12.08, 26.03) * mm});
            skLineSegment(sketch, "E1030", {"start": v(-13.35, 26.03) * mm, "end": v(-13.35, 27.56) * mm});
            skArc(sketch, "E1031", {"start": v(-13.35, 27.56) * mm, "mid": v(-13.1, 27.8) * mm, "end": v(-12.84, 27.56) * mm});
            skLineSegment(sketch, "E1032", {"start": v(-12.84, 27.56) * mm, "end": v(-12.84, 26.03) * mm});
            skArc(sketch, "E1033", {"start": v(-12.84, 26.03) * mm, "mid": v(-13.1, 25.78) * mm, "end": v(-13.35, 26.03) * mm});
            skLineSegment(sketch, "E1034", {"start": v(-14.62, 26.03) * mm, "end": v(-14.62, 27.56) * mm});
            skArc(sketch, "E1035", {"start": v(-14.62, 27.56) * mm, "mid": v(-14.37, 27.8) * mm, "end": v(-14.11, 27.56) * mm});
            skLineSegment(sketch, "E1036", {"start": v(-14.11, 27.56) * mm, "end": v(-14.11, 26.03) * mm});
            skArc(sketch, "E1037", {"start": v(-14.11, 26.03) * mm, "mid": v(-14.37, 25.78) * mm, "end": v(-14.62, 26.03) * mm});
            skLineSegment(sketch, "E1038", {"start": v(-14.62, 20.44) * mm, "end": v(-14.62, 21.97) * mm});
            skArc(sketch, "E1039", {"start": v(-14.62, 21.97) * mm, "mid": v(-14.37, 22.22) * mm, "end": v(-14.11, 21.97) * mm});
            skLineSegment(sketch, "E1040", {"start": v(-14.11, 21.97) * mm, "end": v(-14.11, 20.44) * mm});
            skArc(sketch, "E1041", {"start": v(-14.11, 20.44) * mm, "mid": v(-14.37, 20.2) * mm, "end": v(-14.62, 20.44) * mm});
            skLineSegment(sketch, "E1042", {"start": v(-13.35, 20.44) * mm, "end": v(-13.35, 21.97) * mm});
            skArc(sketch, "E1043", {"start": v(-13.35, 21.97) * mm, "mid": v(-13.1, 22.22) * mm, "end": v(-12.84, 21.97) * mm});
            skLineSegment(sketch, "E1044", {"start": v(-12.84, 21.97) * mm, "end": v(-12.84, 20.44) * mm});
            skArc(sketch, "E1045", {"start": v(-12.84, 20.44) * mm, "mid": v(-13.1, 20.2) * mm, "end": v(-13.35, 20.44) * mm});
            skLineSegment(sketch, "E1046", {"start": v(-12.08, 20.44) * mm, "end": v(-12.08, 21.97) * mm});
            skArc(sketch, "E1047", {"start": v(-12.08, 21.97) * mm, "mid": v(-11.83, 22.22) * mm, "end": v(-11.57, 21.97) * mm});
            skLineSegment(sketch, "E1048", {"start": v(-11.57, 21.97) * mm, "end": v(-11.57, 20.44) * mm});
            skArc(sketch, "E1049", {"start": v(-11.57, 20.44) * mm, "mid": v(-11.83, 20.2) * mm, "end": v(-12.08, 20.44) * mm});
            skLineSegment(sketch, "E1050", {"start": v(-10.8, 20.44) * mm, "end": v(-10.8, 21.97) * mm});
            skArc(sketch, "E1051", {"start": v(-10.8, 21.97) * mm, "mid": v(-10.56, 22.22) * mm, "end": v(-10.3, 21.97) * mm});
            skLineSegment(sketch, "E1052", {"start": v(-10.3, 21.97) * mm, "end": v(-10.3, 20.44) * mm});
            skArc(sketch, "E1053", {"start": v(-10.3, 20.44) * mm, "mid": v(-10.56, 20.2) * mm, "end": v(-10.8, 20.44) * mm});
            skLineSegment(sketch, "E1054", {"start": v(-14.37, 19.55) * mm, "end": v(-14.37, 20.06) * mm});
            skLineSegment(sketch, "E1055", {"start": v(-9.92, 23.37) * mm, "end": v(-10.56, 24) * mm});
            skLineSegment(sketch, "E1056", {"start": v(-10.56, 24) * mm, "end": v(-9.92, 24.63) * mm});
            skLineSegment(sketch, "E1057", {"start": v(-11.83, 24) * mm, "end": v(-13.1, 24) * mm});
            skLineSegment(sketch, "E1058", {"start": v(-12.46, 23.37) * mm, "end": v(-12.46, 24.63) * mm});
            skArc(sketch, "E1059", {"start": v(-10.3, 28.2) * mm, "mid": v(-10.56, 28.45) * mm, "end": v(-10.8, 28.2) * mm});
            skArc(sketch, "E1060", {"start": v(-10.8, 28.2) * mm, "mid": v(-10.56, 27.94) * mm, "end": v(-10.3, 28.2) * mm});
            skLineSegment(sketch, "E1061", {"start": v(-9.92, 25.4) * mm, "end": v(-9.92, 22.6) * mm});
            skLineSegment(sketch, "E1062", {"start": v(-9.92, 22.6) * mm, "end": v(-15, 22.6) * mm});
            skLineSegment(sketch, "E1063", {"start": v(-15, 22.6) * mm, "end": v(-15, 25.4) * mm});
            skLineSegment(sketch, "E1064", {"start": v(-15, 25.4) * mm, "end": v(-9.92, 25.4) * mm});
            skLineSegment(sketch, "E1065", {"start": v(-14.11, -17.03) * mm, "end": v(-14.11, -18.56) * mm});
            skArc(sketch, "E1066", {"start": v(-14.11, -18.56) * mm, "mid": v(-14.37, -18.8) * mm, "end": v(-14.62, -18.56) * mm});
            skLineSegment(sketch, "E1067", {"start": v(-14.62, -18.56) * mm, "end": v(-14.62, -17.03) * mm});
            skArc(sketch, "E1068", {"start": v(-14.62, -17.03) * mm, "mid": v(-14.37, -16.78) * mm, "end": v(-14.11, -17.03) * mm});
            skLineSegment(sketch, "E1069", {"start": v(-12.84, -17.03) * mm, "end": v(-12.84, -18.56) * mm});
            skArc(sketch, "E1070", {"start": v(-12.84, -18.56) * mm, "mid": v(-13.1, -18.8) * mm, "end": v(-13.35, -18.56) * mm});
            skLineSegment(sketch, "E1071", {"start": v(-13.35, -18.56) * mm, "end": v(-13.35, -17.03) * mm});
            skArc(sketch, "E1072", {"start": v(-13.35, -17.03) * mm, "mid": v(-13.1, -16.78) * mm, "end": v(-12.84, -17.03) * mm});
            skLineSegment(sketch, "E1073", {"start": v(-11.57, -17.03) * mm, "end": v(-11.57, -18.56) * mm});
            skArc(sketch, "E1074", {"start": v(-11.57, -18.56) * mm, "mid": v(-11.83, -18.8) * mm, "end": v(-12.08, -18.56) * mm});
            skLineSegment(sketch, "E1075", {"start": v(-12.08, -18.56) * mm, "end": v(-12.08, -17.03) * mm});
            skArc(sketch, "E1076", {"start": v(-12.08, -17.03) * mm, "mid": v(-11.83, -16.78) * mm, "end": v(-11.57, -17.03) * mm});
            skLineSegment(sketch, "E1077", {"start": v(-10.3, -17.03) * mm, "end": v(-10.3, -18.56) * mm});
            skArc(sketch, "E1078", {"start": v(-10.3, -18.56) * mm, "mid": v(-10.56, -18.8) * mm, "end": v(-10.8, -18.56) * mm});
            skLineSegment(sketch, "E1079", {"start": v(-10.8, -18.56) * mm, "end": v(-10.8, -17.03) * mm});
            skArc(sketch, "E1080", {"start": v(-10.8, -17.03) * mm, "mid": v(-10.56, -16.78) * mm, "end": v(-10.3, -17.03) * mm});
            skLineSegment(sketch, "E1081", {"start": v(-10.3, -11.44) * mm, "end": v(-10.3, -12.97) * mm});
            skArc(sketch, "E1082", {"start": v(-10.3, -12.97) * mm, "mid": v(-10.56, -13.22) * mm, "end": v(-10.8, -12.97) * mm});
            skLineSegment(sketch, "E1083", {"start": v(-10.8, -12.97) * mm, "end": v(-10.8, -11.44) * mm});
            skArc(sketch, "E1084", {"start": v(-10.8, -11.44) * mm, "mid": v(-10.56, -11.19) * mm, "end": v(-10.3, -11.44) * mm});
            skLineSegment(sketch, "E1085", {"start": v(-11.57, -11.44) * mm, "end": v(-11.57, -12.97) * mm});
            skArc(sketch, "E1086", {"start": v(-11.57, -12.97) * mm, "mid": v(-11.83, -13.22) * mm, "end": v(-12.08, -12.97) * mm});
            skLineSegment(sketch, "E1087", {"start": v(-12.08, -12.97) * mm, "end": v(-12.08, -11.44) * mm});
            skArc(sketch, "E1088", {"start": v(-12.08, -11.44) * mm, "mid": v(-11.83, -11.19) * mm, "end": v(-11.57, -11.44) * mm});
            skLineSegment(sketch, "E1089", {"start": v(-12.84, -11.44) * mm, "end": v(-12.84, -12.97) * mm});
            skArc(sketch, "E1090", {"start": v(-12.84, -12.97) * mm, "mid": v(-13.1, -13.22) * mm, "end": v(-13.35, -12.97) * mm});
            skLineSegment(sketch, "E1091", {"start": v(-13.35, -12.97) * mm, "end": v(-13.35, -11.44) * mm});
            skArc(sketch, "E1092", {"start": v(-13.35, -11.44) * mm, "mid": v(-13.1, -11.19) * mm, "end": v(-12.84, -11.44) * mm});
            skLineSegment(sketch, "E1093", {"start": v(-14.11, -11.44) * mm, "end": v(-14.11, -12.97) * mm});
            skArc(sketch, "E1094", {"start": v(-14.11, -12.97) * mm, "mid": v(-14.37, -13.22) * mm, "end": v(-14.62, -12.97) * mm});
            skLineSegment(sketch, "E1095", {"start": v(-14.62, -12.97) * mm, "end": v(-14.62, -11.44) * mm});
            skArc(sketch, "E1096", {"start": v(-14.62, -11.44) * mm, "mid": v(-14.37, -11.19) * mm, "end": v(-14.11, -11.44) * mm});
            skLineSegment(sketch, "E1097", {"start": v(-10.56, -10.55) * mm, "end": v(-10.56, -11.06) * mm});
            skLineSegment(sketch, "E1098", {"start": v(-15, -14.36) * mm, "end": v(-14.37, -15) * mm});
            skLineSegment(sketch, "E1099", {"start": v(-14.37, -15) * mm, "end": v(-15, -15.63) * mm});
            skLineSegment(sketch, "E1100", {"start": v(-13.1, -15) * mm, "end": v(-11.83, -15) * mm});
            skLineSegment(sketch, "E1101", {"start": v(-12.46, -14.36) * mm, "end": v(-12.46, -15.63) * mm});
            skArc(sketch, "E1102", {"start": v(-14.11, -19.2) * mm, "mid": v(-14.37, -18.94) * mm, "end": v(-14.62, -19.2) * mm});
            skArc(sketch, "E1103", {"start": v(-14.62, -19.2) * mm, "mid": v(-14.37, -19.45) * mm, "end": v(-14.11, -19.2) * mm});
            skLineSegment(sketch, "E1104", {"start": v(-15, -16.4) * mm, "end": v(-15, -13.6) * mm});
            skLineSegment(sketch, "E1105", {"start": v(-15, -13.6) * mm, "end": v(-9.92, -13.6) * mm});
            skLineSegment(sketch, "E1106", {"start": v(-9.92, -13.6) * mm, "end": v(-9.92, -16.4) * mm});
            skLineSegment(sketch, "E1107", {"start": v(-9.92, -16.4) * mm, "end": v(-15, -16.4) * mm});
            skLineSegment(sketch, "E1108", {"start": v(16.5, -9.3) * mm, "end": v(14.98, -9.3) * mm});
            skArc(sketch, "E1109", {"start": v(14.98, -9.3) * mm, "mid": v(14.73, -9.05) * mm, "end": v(14.98, -8.8) * mm});
            skLineSegment(sketch, "E1110", {"start": v(14.98, -8.8) * mm, "end": v(16.5, -8.8) * mm});
            skArc(sketch, "E1111", {"start": v(16.5, -8.8) * mm, "mid": v(16.76, -9.05) * mm, "end": v(16.5, -9.3) * mm});
            skLineSegment(sketch, "E1112", {"start": v(16.5, -10.58) * mm, "end": v(14.98, -10.58) * mm});
            skArc(sketch, "E1113", {"start": v(14.98, -10.58) * mm, "mid": v(14.73, -10.32) * mm, "end": v(14.98, -10.07) * mm});
            skLineSegment(sketch, "E1114", {"start": v(14.98, -10.07) * mm, "end": v(16.5, -10.07) * mm});
            skArc(sketch, "E1115", {"start": v(16.5, -10.07) * mm, "mid": v(16.76, -10.32) * mm, "end": v(16.5, -10.58) * mm});
            skLineSegment(sketch, "E1116", {"start": v(16.5, -11.85) * mm, "end": v(14.98, -11.85) * mm});
            skArc(sketch, "E1117", {"start": v(14.98, -11.85) * mm, "mid": v(14.73, -11.6) * mm, "end": v(14.98, -11.34) * mm});
            skLineSegment(sketch, "E1118", {"start": v(14.98, -11.34) * mm, "end": v(16.5, -11.34) * mm});
            skArc(sketch, "E1119", {"start": v(16.5, -11.34) * mm, "mid": v(16.76, -11.6) * mm, "end": v(16.5, -11.85) * mm});
            skLineSegment(sketch, "E1120", {"start": v(16.5, -13.12) * mm, "end": v(14.98, -13.12) * mm});
            skArc(sketch, "E1121", {"start": v(14.98, -13.12) * mm, "mid": v(14.73, -12.86) * mm, "end": v(14.98, -12.61) * mm});
            skLineSegment(sketch, "E1122", {"start": v(14.98, -12.61) * mm, "end": v(16.5, -12.61) * mm});
            skArc(sketch, "E1123", {"start": v(16.5, -12.61) * mm, "mid": v(16.76, -12.86) * mm, "end": v(16.5, -13.12) * mm});
            skLineSegment(sketch, "E1124", {"start": v(16.5, -14.39) * mm, "end": v(14.98, -14.39) * mm});
            skArc(sketch, "E1125", {"start": v(14.98, -14.39) * mm, "mid": v(14.73, -14.14) * mm, "end": v(14.98, -13.88) * mm});
            skLineSegment(sketch, "E1126", {"start": v(14.98, -13.88) * mm, "end": v(16.5, -13.88) * mm});
            skArc(sketch, "E1127", {"start": v(16.5, -13.88) * mm, "mid": v(16.76, -14.14) * mm, "end": v(16.5, -14.39) * mm});
            skLineSegment(sketch, "E1128", {"start": v(16.5, -15.66) * mm, "end": v(14.98, -15.66) * mm});
            skArc(sketch, "E1129", {"start": v(14.98, -15.66) * mm, "mid": v(14.73, -15.4) * mm, "end": v(14.98, -15.15) * mm});
            skLineSegment(sketch, "E1130", {"start": v(14.98, -15.15) * mm, "end": v(16.5, -15.15) * mm});
            skArc(sketch, "E1131", {"start": v(16.5, -15.15) * mm, "mid": v(16.76, -15.4) * mm, "end": v(16.5, -15.66) * mm});
            skLineSegment(sketch, "E1132", {"start": v(16.5, -16.93) * mm, "end": v(14.98, -16.93) * mm});
            skArc(sketch, "E1133", {"start": v(14.98, -16.93) * mm, "mid": v(14.73, -16.68) * mm, "end": v(14.98, -16.42) * mm});
            skLineSegment(sketch, "E1134", {"start": v(14.98, -16.42) * mm, "end": v(16.5, -16.42) * mm});
            skArc(sketch, "E1135", {"start": v(16.5, -16.42) * mm, "mid": v(16.76, -16.68) * mm, "end": v(16.5, -16.93) * mm});
            skLineSegment(sketch, "E1136", {"start": v(16.5, -18.2) * mm, "end": v(14.98, -18.2) * mm});
            skArc(sketch, "E1137", {"start": v(14.98, -18.2) * mm, "mid": v(14.73, -17.95) * mm, "end": v(14.98, -17.7) * mm});
            skLineSegment(sketch, "E1138", {"start": v(14.98, -17.7) * mm, "end": v(16.5, -17.7) * mm});
            skArc(sketch, "E1139", {"start": v(16.5, -17.7) * mm, "mid": v(16.76, -17.95) * mm, "end": v(16.5, -18.2) * mm});
            skLineSegment(sketch, "E1140", {"start": v(22.1, -18.2) * mm, "end": v(20.57, -18.2) * mm});
            skArc(sketch, "E1141", {"start": v(20.57, -18.2) * mm, "mid": v(20.32, -17.95) * mm, "end": v(20.57, -17.7) * mm});
            skLineSegment(sketch, "E1142", {"start": v(20.57, -17.7) * mm, "end": v(22.1, -17.7) * mm});
            skArc(sketch, "E1143", {"start": v(22.1, -17.7) * mm, "mid": v(22.35, -17.95) * mm, "end": v(22.1, -18.2) * mm});
            skLineSegment(sketch, "E1144", {"start": v(22.1, -16.93) * mm, "end": v(20.57, -16.93) * mm});
            skArc(sketch, "E1145", {"start": v(20.57, -16.93) * mm, "mid": v(20.32, -16.68) * mm, "end": v(20.57, -16.42) * mm});
            skLineSegment(sketch, "E1146", {"start": v(20.57, -16.42) * mm, "end": v(22.1, -16.42) * mm});
            skArc(sketch, "E1147", {"start": v(22.1, -16.42) * mm, "mid": v(22.35, -16.68) * mm, "end": v(22.1, -16.93) * mm});
            skLineSegment(sketch, "E1148", {"start": v(22.1, -15.66) * mm, "end": v(20.57, -15.66) * mm});
            skArc(sketch, "E1149", {"start": v(20.57, -15.66) * mm, "mid": v(20.32, -15.4) * mm, "end": v(20.57, -15.15) * mm});
            skLineSegment(sketch, "E1150", {"start": v(20.57, -15.15) * mm, "end": v(22.1, -15.15) * mm});
            skArc(sketch, "E1151", {"start": v(22.1, -15.15) * mm, "mid": v(22.35, -15.4) * mm, "end": v(22.1, -15.66) * mm});
            skLineSegment(sketch, "E1152", {"start": v(22.1, -14.39) * mm, "end": v(20.57, -14.39) * mm});
            skArc(sketch, "E1153", {"start": v(20.57, -14.39) * mm, "mid": v(20.32, -14.14) * mm, "end": v(20.57, -13.88) * mm});
            skLineSegment(sketch, "E1154", {"start": v(20.57, -13.88) * mm, "end": v(22.1, -13.88) * mm});
            skArc(sketch, "E1155", {"start": v(22.1, -13.88) * mm, "mid": v(22.35, -14.14) * mm, "end": v(22.1, -14.39) * mm});
            skLineSegment(sketch, "E1156", {"start": v(22.1, -13.12) * mm, "end": v(20.57, -13.12) * mm});
            skArc(sketch, "E1157", {"start": v(20.57, -13.12) * mm, "mid": v(20.32, -12.86) * mm, "end": v(20.57, -12.61) * mm});
            skLineSegment(sketch, "E1158", {"start": v(20.57, -12.61) * mm, "end": v(22.1, -12.61) * mm});
            skArc(sketch, "E1159", {"start": v(22.1, -12.61) * mm, "mid": v(22.35, -12.86) * mm, "end": v(22.1, -13.12) * mm});
            skLineSegment(sketch, "E1160", {"start": v(22.1, -11.85) * mm, "end": v(20.57, -11.85) * mm});
            skArc(sketch, "E1161", {"start": v(20.57, -11.85) * mm, "mid": v(20.32, -11.6) * mm, "end": v(20.57, -11.34) * mm});
            skLineSegment(sketch, "E1162", {"start": v(20.57, -11.34) * mm, "end": v(22.1, -11.34) * mm});
            skArc(sketch, "E1163", {"start": v(22.1, -11.34) * mm, "mid": v(22.35, -11.6) * mm, "end": v(22.1, -11.85) * mm});
            skLineSegment(sketch, "E1164", {"start": v(22.1, -10.58) * mm, "end": v(20.57, -10.58) * mm});
            skArc(sketch, "E1165", {"start": v(20.57, -10.58) * mm, "mid": v(20.32, -10.32) * mm, "end": v(20.57, -10.07) * mm});
            skLineSegment(sketch, "E1166", {"start": v(20.57, -10.07) * mm, "end": v(22.1, -10.07) * mm});
            skArc(sketch, "E1167", {"start": v(22.1, -10.07) * mm, "mid": v(22.35, -10.32) * mm, "end": v(22.1, -10.58) * mm});
            skLineSegment(sketch, "E1168", {"start": v(22.1, -9.3) * mm, "end": v(20.57, -9.3) * mm});
            skArc(sketch, "E1169", {"start": v(20.57, -9.3) * mm, "mid": v(20.32, -9.05) * mm, "end": v(20.57, -8.8) * mm});
            skLineSegment(sketch, "E1170", {"start": v(20.57, -8.8) * mm, "end": v(22.1, -8.8) * mm});
            skArc(sketch, "E1171", {"start": v(22.1, -8.8) * mm, "mid": v(22.35, -9.05) * mm, "end": v(22.1, -9.3) * mm});
            skLineSegment(sketch, "E1172", {"start": v(14.6, -14.14) * mm, "end": v(14.1, -14.14) * mm});
            skLineSegment(sketch, "E1173", {"start": v(19.17, -8.42) * mm, "end": v(18.54, -9.05) * mm});
            skLineSegment(sketch, "E1174", {"start": v(18.54, -9.05) * mm, "end": v(17.9, -8.42) * mm});
            skLineSegment(sketch, "E1175", {"start": v(18.54, -12.86) * mm, "end": v(18.54, -14.14) * mm});
            skLineSegment(sketch, "E1176", {"start": v(19.17, -13.5) * mm, "end": v(17.9, -13.5) * mm});
            skLineSegment(sketch, "E1177", {"start": v(22.98, -10.32) * mm, "end": v(22.48, -10.32) * mm});
            skArc(sketch, "E1178", {"start": v(14.6, -9.05) * mm, "mid": v(14.35, -8.8) * mm, "end": v(14.1, -9.05) * mm});
            skArc(sketch, "E1179", {"start": v(14.1, -9.05) * mm, "mid": v(14.35, -9.3) * mm, "end": v(14.6, -9.05) * mm});
            skLineSegment(sketch, "E1180", {"start": v(22.48, -16.68) * mm, "end": v(22.98, -16.42) * mm});
            skLineSegment(sketch, "E1181", {"start": v(22.98, -16.42) * mm, "end": v(22.98, -16.93) * mm});
            skLineSegment(sketch, "E1182", {"start": v(22.98, -16.93) * mm, "end": v(22.48, -16.68) * mm});
            skLineSegment(sketch, "E1183", {"start": v(17.14, -8.42) * mm, "end": v(19.94, -8.42) * mm});
            skLineSegment(sketch, "E1184", {"start": v(19.94, -8.42) * mm, "end": v(19.94, -18.58) * mm});
            skLineSegment(sketch, "E1185", {"start": v(19.94, -18.58) * mm, "end": v(17.14, -18.58) * mm});
            skLineSegment(sketch, "E1186", {"start": v(17.14, -18.58) * mm, "end": v(17.14, -8.42) * mm});
            skLineSegment(sketch, "E1187", {"start": v(17.04, 18.4) * mm, "end": v(17.04, 17) * mm});
            skArc(sketch, "E1188", {"start": v(17.04, 17) * mm, "mid": v(16.85, 16.81) * mm, "end": v(16.66, 17) * mm});
            skLineSegment(sketch, "E1189", {"start": v(16.66, 17) * mm, "end": v(16.66, 18.4) * mm});
            skArc(sketch, "E1190", {"start": v(16.66, 18.4) * mm, "mid": v(16.85, 18.59) * mm, "end": v(17.04, 18.4) * mm});
            skLineSegment(sketch, "E1191", {"start": v(16.42, 18.46) * mm, "end": v(16.42, 16.94) * mm});
            skArc(sketch, "E1192", {"start": v(16.42, 16.94) * mm, "mid": v(16.29, 16.81) * mm, "end": v(16.16, 16.94) * mm});
            skLineSegment(sketch, "E1193", {"start": v(16.16, 16.94) * mm, "end": v(16.16, 18.46) * mm});
            skArc(sketch, "E1194", {"start": v(16.16, 18.46) * mm, "mid": v(16.29, 18.59) * mm, "end": v(16.42, 18.46) * mm});
            skLineSegment(sketch, "E1195", {"start": v(15.92, 18.46) * mm, "end": v(15.92, 16.94) * mm});
            skArc(sketch, "E1196", {"start": v(15.92, 16.94) * mm, "mid": v(15.79, 16.81) * mm, "end": v(15.66, 16.94) * mm});
            skLineSegment(sketch, "E1197", {"start": v(15.66, 16.94) * mm, "end": v(15.66, 18.46) * mm});
            skArc(sketch, "E1198", {"start": v(15.66, 18.46) * mm, "mid": v(15.79, 18.59) * mm, "end": v(15.92, 18.46) * mm});
            skLineSegment(sketch, "E1199", {"start": v(15.42, 18.46) * mm, "end": v(15.42, 16.94) * mm});
            skArc(sketch, "E1200", {"start": v(15.42, 16.94) * mm, "mid": v(15.29, 16.81) * mm, "end": v(15.16, 16.94) * mm});
            skLineSegment(sketch, "E1201", {"start": v(15.16, 16.94) * mm, "end": v(15.16, 18.46) * mm});
            skArc(sketch, "E1202", {"start": v(15.16, 18.46) * mm, "mid": v(15.29, 18.59) * mm, "end": v(15.42, 18.46) * mm});
            skLineSegment(sketch, "E1203", {"start": v(14.92, 18.46) * mm, "end": v(14.92, 16.94) * mm});
            skArc(sketch, "E1204", {"start": v(14.92, 16.94) * mm, "mid": v(14.79, 16.81) * mm, "end": v(14.66, 16.94) * mm});
            skLineSegment(sketch, "E1205", {"start": v(14.66, 16.94) * mm, "end": v(14.66, 18.46) * mm});
            skArc(sketch, "E1206", {"start": v(14.66, 18.46) * mm, "mid": v(14.79, 18.59) * mm, "end": v(14.92, 18.46) * mm});
            skLineSegment(sketch, "E1207", {"start": v(14.42, 18.46) * mm, "end": v(14.42, 16.94) * mm});
            skArc(sketch, "E1208", {"start": v(14.42, 16.94) * mm, "mid": v(14.29, 16.81) * mm, "end": v(14.16, 16.94) * mm});
            skLineSegment(sketch, "E1209", {"start": v(14.16, 16.94) * mm, "end": v(14.16, 18.46) * mm});
            skArc(sketch, "E1210", {"start": v(14.16, 18.46) * mm, "mid": v(14.29, 18.59) * mm, "end": v(14.42, 18.46) * mm});
            skLineSegment(sketch, "E1211", {"start": v(13.92, 18.46) * mm, "end": v(13.92, 16.94) * mm});
            skArc(sketch, "E1212", {"start": v(13.92, 16.94) * mm, "mid": v(13.79, 16.81) * mm, "end": v(13.66, 16.94) * mm});
            skLineSegment(sketch, "E1213", {"start": v(13.66, 16.94) * mm, "end": v(13.66, 18.46) * mm});
            skArc(sketch, "E1214", {"start": v(13.66, 18.46) * mm, "mid": v(13.79, 18.59) * mm, "end": v(13.92, 18.46) * mm});
            skLineSegment(sketch, "E1215", {"start": v(13.42, 18.46) * mm, "end": v(13.42, 16.94) * mm});
            skArc(sketch, "E1216", {"start": v(13.42, 16.94) * mm, "mid": v(13.29, 16.81) * mm, "end": v(13.16, 16.94) * mm});
            skLineSegment(sketch, "E1217", {"start": v(13.16, 16.94) * mm, "end": v(13.16, 18.46) * mm});
            skArc(sketch, "E1218", {"start": v(13.16, 18.46) * mm, "mid": v(13.29, 18.59) * mm, "end": v(13.42, 18.46) * mm});
            skLineSegment(sketch, "E1219", {"start": v(12.92, 18.46) * mm, "end": v(12.92, 16.94) * mm});
            skArc(sketch, "E1220", {"start": v(12.92, 16.94) * mm, "mid": v(12.79, 16.81) * mm, "end": v(12.66, 16.94) * mm});
            skLineSegment(sketch, "E1221", {"start": v(12.66, 16.94) * mm, "end": v(12.66, 18.46) * mm});
            skArc(sketch, "E1222", {"start": v(12.66, 18.46) * mm, "mid": v(12.79, 18.59) * mm, "end": v(12.92, 18.46) * mm});
            skLineSegment(sketch, "E1223", {"start": v(10.54, 16.12) * mm, "end": v(9.14, 16.12) * mm});
            skArc(sketch, "E1224", {"start": v(9.14, 16.12) * mm, "mid": v(8.95, 16.31) * mm, "end": v(9.14, 16.5) * mm});
            skLineSegment(sketch, "E1225", {"start": v(9.14, 16.5) * mm, "end": v(10.54, 16.5) * mm});
            skArc(sketch, "E1226", {"start": v(10.54, 16.5) * mm, "mid": v(10.73, 16.31) * mm, "end": v(10.54, 16.12) * mm});
            skLineSegment(sketch, "E1227", {"start": v(10.6, 15.62) * mm, "end": v(9.08, 15.62) * mm});
            skArc(sketch, "E1228", {"start": v(9.08, 15.62) * mm, "mid": v(8.95, 15.75) * mm, "end": v(9.08, 15.88) * mm});
            skLineSegment(sketch, "E1229", {"start": v(9.08, 15.88) * mm, "end": v(10.6, 15.88) * mm});
            skArc(sketch, "E1230", {"start": v(10.6, 15.88) * mm, "mid": v(10.73, 15.75) * mm, "end": v(10.6, 15.62) * mm});
            skLineSegment(sketch, "E1231", {"start": v(10.6, 15.12) * mm, "end": v(9.08, 15.12) * mm});
            skArc(sketch, "E1232", {"start": v(9.08, 15.12) * mm, "mid": v(8.95, 15.25) * mm, "end": v(9.08, 15.38) * mm});
            skLineSegment(sketch, "E1233", {"start": v(9.08, 15.38) * mm, "end": v(10.6, 15.38) * mm});
            skArc(sketch, "E1234", {"start": v(10.6, 15.38) * mm, "mid": v(10.73, 15.25) * mm, "end": v(10.6, 15.12) * mm});
            skLineSegment(sketch, "E1235", {"start": v(10.6, 14.62) * mm, "end": v(9.08, 14.62) * mm});
            skArc(sketch, "E1236", {"start": v(9.08, 14.62) * mm, "mid": v(8.95, 14.75) * mm, "end": v(9.08, 14.88) * mm});
            skLineSegment(sketch, "E1237", {"start": v(9.08, 14.88) * mm, "end": v(10.6, 14.88) * mm});
            skArc(sketch, "E1238", {"start": v(10.6, 14.88) * mm, "mid": v(10.73, 14.75) * mm, "end": v(10.6, 14.62) * mm});
            skLineSegment(sketch, "E1239", {"start": v(10.6, 14.12) * mm, "end": v(9.08, 14.12) * mm});
            skArc(sketch, "E1240", {"start": v(9.08, 14.12) * mm, "mid": v(8.95, 14.25) * mm, "end": v(9.08, 14.38) * mm});
            skLineSegment(sketch, "E1241", {"start": v(9.08, 14.38) * mm, "end": v(10.6, 14.38) * mm});
            skArc(sketch, "E1242", {"start": v(10.6, 14.38) * mm, "mid": v(10.73, 14.25) * mm, "end": v(10.6, 14.12) * mm});
            skLineSegment(sketch, "E1243", {"start": v(10.6, 12.62) * mm, "end": v(9.08, 12.62) * mm});
            skArc(sketch, "E1244", {"start": v(9.08, 12.62) * mm, "mid": v(8.95, 12.75) * mm, "end": v(9.08, 12.88) * mm});
            skLineSegment(sketch, "E1245", {"start": v(9.08, 12.88) * mm, "end": v(10.6, 12.88) * mm});
            skArc(sketch, "E1246", {"start": v(10.6, 12.88) * mm, "mid": v(10.73, 12.75) * mm, "end": v(10.6, 12.62) * mm});
            skLineSegment(sketch, "E1247", {"start": v(10.6, 12.12) * mm, "end": v(9.08, 12.12) * mm});
            skArc(sketch, "E1248", {"start": v(9.08, 12.12) * mm, "mid": v(8.95, 12.25) * mm, "end": v(9.08, 12.38) * mm});
            skLineSegment(sketch, "E1249", {"start": v(9.08, 12.38) * mm, "end": v(10.6, 12.38) * mm});
            skArc(sketch, "E1250", {"start": v(10.6, 12.38) * mm, "mid": v(10.73, 12.25) * mm, "end": v(10.6, 12.12) * mm});
            skLineSegment(sketch, "E1251", {"start": v(10.6, 11.62) * mm, "end": v(9.08, 11.62) * mm});
            skArc(sketch, "E1252", {"start": v(9.08, 11.62) * mm, "mid": v(8.95, 11.75) * mm, "end": v(9.08, 11.88) * mm});
            skLineSegment(sketch, "E1253", {"start": v(9.08, 11.88) * mm, "end": v(10.6, 11.88) * mm});
            skArc(sketch, "E1254", {"start": v(10.6, 11.88) * mm, "mid": v(10.73, 11.75) * mm, "end": v(10.6, 11.62) * mm});
            skLineSegment(sketch, "E1255", {"start": v(10.6, 11.12) * mm, "end": v(9.08, 11.12) * mm});
            skArc(sketch, "E1256", {"start": v(9.08, 11.12) * mm, "mid": v(8.95, 11.25) * mm, "end": v(9.08, 11.38) * mm});
            skLineSegment(sketch, "E1257", {"start": v(9.08, 11.38) * mm, "end": v(10.6, 11.38) * mm});
            skArc(sketch, "E1258", {"start": v(10.6, 11.38) * mm, "mid": v(10.73, 11.25) * mm, "end": v(10.6, 11.12) * mm});
            skLineSegment(sketch, "E1259", {"start": v(10.54, 10.5) * mm, "end": v(9.14, 10.5) * mm});
            skArc(sketch, "E1260", {"start": v(9.14, 10.5) * mm, "mid": v(8.95, 10.69) * mm, "end": v(9.14, 10.88) * mm});
            skLineSegment(sketch, "E1261", {"start": v(9.14, 10.88) * mm, "end": v(10.54, 10.88) * mm});
            skArc(sketch, "E1262", {"start": v(10.54, 10.88) * mm, "mid": v(10.73, 10.69) * mm, "end": v(10.54, 10.5) * mm});
            skLineSegment(sketch, "E1263", {"start": v(11.42, 10) * mm, "end": v(11.42, 8.6) * mm});
            skArc(sketch, "E1264", {"start": v(11.42, 8.6) * mm, "mid": v(11.23, 8.41) * mm, "end": v(11.04, 8.6) * mm});
            skLineSegment(sketch, "E1265", {"start": v(11.04, 8.6) * mm, "end": v(11.04, 10) * mm});
            skArc(sketch, "E1266", {"start": v(11.04, 10) * mm, "mid": v(11.23, 10.19) * mm, "end": v(11.42, 10) * mm});
            skLineSegment(sketch, "E1267", {"start": v(11.92, 10.06) * mm, "end": v(11.92, 8.54) * mm});
            skArc(sketch, "E1268", {"start": v(11.92, 8.54) * mm, "mid": v(11.79, 8.41) * mm, "end": v(11.66, 8.54) * mm});
            skLineSegment(sketch, "E1269", {"start": v(11.66, 8.54) * mm, "end": v(11.66, 10.06) * mm});
            skArc(sketch, "E1270", {"start": v(11.66, 10.06) * mm, "mid": v(11.79, 10.19) * mm, "end": v(11.92, 10.06) * mm});
            skLineSegment(sketch, "E1271", {"start": v(12.42, 10.06) * mm, "end": v(12.42, 8.54) * mm});
            skArc(sketch, "E1272", {"start": v(12.42, 8.54) * mm, "mid": v(12.29, 8.41) * mm, "end": v(12.16, 8.54) * mm});
            skLineSegment(sketch, "E1273", {"start": v(12.16, 8.54) * mm, "end": v(12.16, 10.06) * mm});
            skArc(sketch, "E1274", {"start": v(12.16, 10.06) * mm, "mid": v(12.29, 10.19) * mm, "end": v(12.42, 10.06) * mm});
            skLineSegment(sketch, "E1275", {"start": v(12.92, 10.06) * mm, "end": v(12.92, 8.54) * mm});
            skArc(sketch, "E1276", {"start": v(12.92, 8.54) * mm, "mid": v(12.79, 8.41) * mm, "end": v(12.66, 8.54) * mm});
            skLineSegment(sketch, "E1277", {"start": v(12.66, 8.54) * mm, "end": v(12.66, 10.06) * mm});
            skArc(sketch, "E1278", {"start": v(12.66, 10.06) * mm, "mid": v(12.79, 10.19) * mm, "end": v(12.92, 10.06) * mm});
            skLineSegment(sketch, "E1279", {"start": v(13.42, 10.06) * mm, "end": v(13.42, 8.54) * mm});
            skArc(sketch, "E1280", {"start": v(13.42, 8.54) * mm, "mid": v(13.29, 8.41) * mm, "end": v(13.16, 8.54) * mm});
            skLineSegment(sketch, "E1281", {"start": v(13.16, 8.54) * mm, "end": v(13.16, 10.06) * mm});
            skArc(sketch, "E1282", {"start": v(13.16, 10.06) * mm, "mid": v(13.29, 10.19) * mm, "end": v(13.42, 10.06) * mm});
            skLineSegment(sketch, "E1283", {"start": v(14.92, 10.06) * mm, "end": v(14.92, 8.54) * mm});
            skArc(sketch, "E1284", {"start": v(14.92, 8.54) * mm, "mid": v(14.79, 8.41) * mm, "end": v(14.66, 8.54) * mm});
            skLineSegment(sketch, "E1285", {"start": v(14.66, 8.54) * mm, "end": v(14.66, 10.06) * mm});
            skArc(sketch, "E1286", {"start": v(14.66, 10.06) * mm, "mid": v(14.79, 10.19) * mm, "end": v(14.92, 10.06) * mm});
            skLineSegment(sketch, "E1287", {"start": v(15.42, 10.06) * mm, "end": v(15.42, 8.54) * mm});
            skArc(sketch, "E1288", {"start": v(15.42, 8.54) * mm, "mid": v(15.29, 8.41) * mm, "end": v(15.16, 8.54) * mm});
            skLineSegment(sketch, "E1289", {"start": v(15.16, 8.54) * mm, "end": v(15.16, 10.06) * mm});
            skArc(sketch, "E1290", {"start": v(15.16, 10.06) * mm, "mid": v(15.29, 10.19) * mm, "end": v(15.42, 10.06) * mm});
            skLineSegment(sketch, "E1291", {"start": v(15.92, 10.06) * mm, "end": v(15.92, 8.54) * mm});
            skArc(sketch, "E1292", {"start": v(15.92, 8.54) * mm, "mid": v(15.79, 8.41) * mm, "end": v(15.66, 8.54) * mm});
            skLineSegment(sketch, "E1293", {"start": v(15.66, 8.54) * mm, "end": v(15.66, 10.06) * mm});
            skArc(sketch, "E1294", {"start": v(15.66, 10.06) * mm, "mid": v(15.79, 10.19) * mm, "end": v(15.92, 10.06) * mm});
            skLineSegment(sketch, "E1295", {"start": v(16.42, 10.06) * mm, "end": v(16.42, 8.54) * mm});
            skArc(sketch, "E1296", {"start": v(16.42, 8.54) * mm, "mid": v(16.29, 8.41) * mm, "end": v(16.16, 8.54) * mm});
            skLineSegment(sketch, "E1297", {"start": v(16.16, 8.54) * mm, "end": v(16.16, 10.06) * mm});
            skArc(sketch, "E1298", {"start": v(16.16, 10.06) * mm, "mid": v(16.29, 10.19) * mm, "end": v(16.42, 10.06) * mm});
            skLineSegment(sketch, "E1299", {"start": v(17.04, 10) * mm, "end": v(17.04, 8.6) * mm});
            skArc(sketch, "E1300", {"start": v(17.04, 8.6) * mm, "mid": v(16.85, 8.41) * mm, "end": v(16.66, 8.6) * mm});
            skLineSegment(sketch, "E1301", {"start": v(16.66, 8.6) * mm, "end": v(16.66, 10) * mm});
            skArc(sketch, "E1302", {"start": v(16.66, 10) * mm, "mid": v(16.85, 10.19) * mm, "end": v(17.04, 10) * mm});
            skLineSegment(sketch, "E1303", {"start": v(18.94, 10.5) * mm, "end": v(17.54, 10.5) * mm});
            skArc(sketch, "E1304", {"start": v(17.54, 10.5) * mm, "mid": v(17.35, 10.69) * mm, "end": v(17.54, 10.88) * mm});
            skLineSegment(sketch, "E1305", {"start": v(17.54, 10.88) * mm, "end": v(18.94, 10.88) * mm});
            skArc(sketch, "E1306", {"start": v(18.94, 10.88) * mm, "mid": v(19.13, 10.69) * mm, "end": v(18.94, 10.5) * mm});
            skLineSegment(sketch, "E1307", {"start": v(19, 11.12) * mm, "end": v(17.48, 11.12) * mm});
            skArc(sketch, "E1308", {"start": v(17.48, 11.12) * mm, "mid": v(17.35, 11.25) * mm, "end": v(17.48, 11.38) * mm});
            skLineSegment(sketch, "E1309", {"start": v(17.48, 11.38) * mm, "end": v(19, 11.38) * mm});
            skArc(sketch, "E1310", {"start": v(19, 11.38) * mm, "mid": v(19.13, 11.25) * mm, "end": v(19, 11.12) * mm});
            skLineSegment(sketch, "E1311", {"start": v(19, 11.62) * mm, "end": v(17.48, 11.62) * mm});
            skArc(sketch, "E1312", {"start": v(17.48, 11.62) * mm, "mid": v(17.35, 11.75) * mm, "end": v(17.48, 11.88) * mm});
            skLineSegment(sketch, "E1313", {"start": v(17.48, 11.88) * mm, "end": v(19, 11.88) * mm});
            skArc(sketch, "E1314", {"start": v(19, 11.88) * mm, "mid": v(19.13, 11.75) * mm, "end": v(19, 11.62) * mm});
            skLineSegment(sketch, "E1315", {"start": v(19, 12.12) * mm, "end": v(17.48, 12.12) * mm});
            skArc(sketch, "E1316", {"start": v(17.48, 12.12) * mm, "mid": v(17.35, 12.25) * mm, "end": v(17.48, 12.38) * mm});
            skLineSegment(sketch, "E1317", {"start": v(17.48, 12.38) * mm, "end": v(19, 12.38) * mm});
            skArc(sketch, "E1318", {"start": v(19, 12.38) * mm, "mid": v(19.13, 12.25) * mm, "end": v(19, 12.12) * mm});
            skLineSegment(sketch, "E1319", {"start": v(19, 12.62) * mm, "end": v(17.48, 12.62) * mm});
            skArc(sketch, "E1320", {"start": v(17.48, 12.62) * mm, "mid": v(17.35, 12.75) * mm, "end": v(17.48, 12.88) * mm});
            skLineSegment(sketch, "E1321", {"start": v(17.48, 12.88) * mm, "end": v(19, 12.88) * mm});
            skArc(sketch, "E1322", {"start": v(19, 12.88) * mm, "mid": v(19.13, 12.75) * mm, "end": v(19, 12.62) * mm});
            skLineSegment(sketch, "E1323", {"start": v(19, 14.12) * mm, "end": v(17.48, 14.12) * mm});
            skArc(sketch, "E1324", {"start": v(17.48, 14.12) * mm, "mid": v(17.35, 14.25) * mm, "end": v(17.48, 14.38) * mm});
            skLineSegment(sketch, "E1325", {"start": v(17.48, 14.38) * mm, "end": v(19, 14.38) * mm});
            skArc(sketch, "E1326", {"start": v(19, 14.38) * mm, "mid": v(19.13, 14.25) * mm, "end": v(19, 14.12) * mm});
            skLineSegment(sketch, "E1327", {"start": v(19, 14.62) * mm, "end": v(17.48, 14.62) * mm});
            skArc(sketch, "E1328", {"start": v(17.48, 14.62) * mm, "mid": v(17.35, 14.75) * mm, "end": v(17.48, 14.88) * mm});
            skLineSegment(sketch, "E1329", {"start": v(17.48, 14.88) * mm, "end": v(19, 14.88) * mm});
            skArc(sketch, "E1330", {"start": v(19, 14.88) * mm, "mid": v(19.13, 14.75) * mm, "end": v(19, 14.62) * mm});
            skLineSegment(sketch, "E1331", {"start": v(19, 15.12) * mm, "end": v(17.48, 15.12) * mm});
            skArc(sketch, "E1332", {"start": v(17.48, 15.12) * mm, "mid": v(17.35, 15.25) * mm, "end": v(17.48, 15.38) * mm});
            skLineSegment(sketch, "E1333", {"start": v(17.48, 15.38) * mm, "end": v(19, 15.38) * mm});
            skArc(sketch, "E1334", {"start": v(19, 15.38) * mm, "mid": v(19.13, 15.25) * mm, "end": v(19, 15.12) * mm});
            skLineSegment(sketch, "E1335", {"start": v(19, 15.62) * mm, "end": v(17.48, 15.62) * mm});
            skArc(sketch, "E1336", {"start": v(17.48, 15.62) * mm, "mid": v(17.35, 15.75) * mm, "end": v(17.48, 15.88) * mm});
            skLineSegment(sketch, "E1337", {"start": v(17.48, 15.88) * mm, "end": v(19, 15.88) * mm});
            skArc(sketch, "E1338", {"start": v(19, 15.88) * mm, "mid": v(19.13, 15.75) * mm, "end": v(19, 15.62) * mm});
            skLineSegment(sketch, "E1339", {"start": v(18.94, 16.12) * mm, "end": v(17.54, 16.12) * mm});
            skArc(sketch, "E1340", {"start": v(17.54, 16.12) * mm, "mid": v(17.35, 16.31) * mm, "end": v(17.54, 16.5) * mm});
            skLineSegment(sketch, "E1341", {"start": v(17.54, 16.5) * mm, "end": v(18.94, 16.5) * mm});
            skArc(sketch, "E1342", {"start": v(18.94, 16.5) * mm, "mid": v(19.13, 16.31) * mm, "end": v(18.94, 16.12) * mm});
            skLineSegment(sketch, "E1343", {"start": v(12.42, 18.46) * mm, "end": v(12.42, 16.94) * mm});
            skArc(sketch, "E1344", {"start": v(12.42, 16.94) * mm, "mid": v(12.29, 16.81) * mm, "end": v(12.16, 16.94) * mm});
            skLineSegment(sketch, "E1345", {"start": v(12.16, 16.94) * mm, "end": v(12.16, 18.46) * mm});
            skArc(sketch, "E1346", {"start": v(12.16, 18.46) * mm, "mid": v(12.29, 18.59) * mm, "end": v(12.42, 18.46) * mm});
            skLineSegment(sketch, "E1347", {"start": v(11.92, 18.46) * mm, "end": v(11.92, 16.94) * mm});
            skArc(sketch, "E1348", {"start": v(11.92, 16.94) * mm, "mid": v(11.79, 16.81) * mm, "end": v(11.66, 16.94) * mm});
            skLineSegment(sketch, "E1349", {"start": v(11.66, 16.94) * mm, "end": v(11.66, 18.46) * mm});
            skArc(sketch, "E1350", {"start": v(11.66, 18.46) * mm, "mid": v(11.79, 18.59) * mm, "end": v(11.92, 18.46) * mm});
            skLineSegment(sketch, "E1351", {"start": v(11.42, 18.4) * mm, "end": v(11.42, 17) * mm});
            skArc(sketch, "E1352", {"start": v(11.42, 17) * mm, "mid": v(11.23, 16.81) * mm, "end": v(11.04, 17) * mm});
            skLineSegment(sketch, "E1353", {"start": v(11.04, 17) * mm, "end": v(11.04, 18.4) * mm});
            skArc(sketch, "E1354", {"start": v(11.04, 18.4) * mm, "mid": v(11.23, 18.59) * mm, "end": v(11.42, 18.4) * mm});
            skLineSegment(sketch, "E1355", {"start": v(10.6, 13.12) * mm, "end": v(9.08, 13.12) * mm});
            skArc(sketch, "E1356", {"start": v(9.08, 13.12) * mm, "mid": v(8.95, 13.25) * mm, "end": v(9.08, 13.38) * mm});
            skLineSegment(sketch, "E1357", {"start": v(9.08, 13.38) * mm, "end": v(10.6, 13.38) * mm});
            skArc(sketch, "E1358", {"start": v(10.6, 13.38) * mm, "mid": v(10.73, 13.25) * mm, "end": v(10.6, 13.12) * mm});
            skLineSegment(sketch, "E1359", {"start": v(10.6, 13.62) * mm, "end": v(9.08, 13.62) * mm});
            skArc(sketch, "E1360", {"start": v(9.08, 13.62) * mm, "mid": v(8.95, 13.75) * mm, "end": v(9.08, 13.88) * mm});
            skLineSegment(sketch, "E1361", {"start": v(9.08, 13.88) * mm, "end": v(10.6, 13.88) * mm});
            skArc(sketch, "E1362", {"start": v(10.6, 13.88) * mm, "mid": v(10.73, 13.75) * mm, "end": v(10.6, 13.62) * mm});
            skLineSegment(sketch, "E1363", {"start": v(14.42, 10.06) * mm, "end": v(14.42, 8.54) * mm});
            skArc(sketch, "E1364", {"start": v(14.42, 8.54) * mm, "mid": v(14.29, 8.41) * mm, "end": v(14.16, 8.54) * mm});
            skLineSegment(sketch, "E1365", {"start": v(14.16, 8.54) * mm, "end": v(14.16, 10.06) * mm});
            skArc(sketch, "E1366", {"start": v(14.16, 10.06) * mm, "mid": v(14.29, 10.19) * mm, "end": v(14.42, 10.06) * mm});
            skLineSegment(sketch, "E1367", {"start": v(13.92, 10.06) * mm, "end": v(13.92, 8.54) * mm});
            skArc(sketch, "E1368", {"start": v(13.92, 8.54) * mm, "mid": v(13.79, 8.41) * mm, "end": v(13.66, 8.54) * mm});
            skLineSegment(sketch, "E1369", {"start": v(13.66, 8.54) * mm, "end": v(13.66, 10.06) * mm});
            skArc(sketch, "E1370", {"start": v(13.66, 10.06) * mm, "mid": v(13.79, 10.19) * mm, "end": v(13.92, 10.06) * mm});
            skLineSegment(sketch, "E1371", {"start": v(19, 13.62) * mm, "end": v(17.48, 13.62) * mm});
            skArc(sketch, "E1372", {"start": v(17.48, 13.62) * mm, "mid": v(17.35, 13.75) * mm, "end": v(17.48, 13.88) * mm});
            skLineSegment(sketch, "E1373", {"start": v(17.48, 13.88) * mm, "end": v(19, 13.88) * mm});
            skArc(sketch, "E1374", {"start": v(19, 13.88) * mm, "mid": v(19.13, 13.75) * mm, "end": v(19, 13.62) * mm});
            skLineSegment(sketch, "E1375", {"start": v(19, 13.12) * mm, "end": v(17.48, 13.12) * mm});
            skArc(sketch, "E1376", {"start": v(17.48, 13.12) * mm, "mid": v(17.35, 13.25) * mm, "end": v(17.48, 13.38) * mm});
            skLineSegment(sketch, "E1377", {"start": v(17.48, 13.38) * mm, "end": v(19, 13.38) * mm});
            skArc(sketch, "E1378", {"start": v(19, 13.38) * mm, "mid": v(19.13, 13.25) * mm, "end": v(19, 13.12) * mm});
            skArc(sketch, "E1379", {"start": v(17.04, 19) * mm, "mid": v(16.79, 19.25) * mm, "end": v(16.54, 19) * mm});
            skArc(sketch, "E1380", {"start": v(16.54, 19) * mm, "mid": v(16.79, 18.75) * mm, "end": v(17.04, 19) * mm});
            skLineSegment(sketch, "E1381", {"start": v(14.79, 18.75) * mm, "end": v(14.79, 19.25) * mm});
            skLineSegment(sketch, "E1382", {"start": v(11.29, 8.25) * mm, "end": v(11.29, 7.75) * mm});
            skLineSegment(sketch, "E1383", {"start": v(19.29, 14.75) * mm, "end": v(19.79, 14.75) * mm});
            skLineSegment(sketch, "E1384", {"start": v(8.29, 15.25) * mm, "end": v(8.79, 15.25) * mm});
            skLineSegment(sketch, "E1385", {"start": v(16.29, 8.25) * mm, "end": v(16.29, 7.75) * mm});
            skLineSegment(sketch, "E1386", {"start": v(14.04, 14) * mm, "end": v(14.04, 13) * mm});
            skLineSegment(sketch, "E1387", {"start": v(14.54, 13.5) * mm, "end": v(13.54, 13.5) * mm});
            skLineSegment(sketch, "E1388", {"start": v(16.79, 16) * mm, "end": v(16.54, 16.25) * mm});
            skLineSegment(sketch, "E1389", {"start": v(16.54, 16.25) * mm, "end": v(11.54, 16.25) * mm});
            skLineSegment(sketch, "E1390", {"start": v(11.54, 16.25) * mm, "end": v(11.29, 16) * mm});
            skLineSegment(sketch, "E1391", {"start": v(11.29, 16) * mm, "end": v(11.29, 11) * mm});
            skLineSegment(sketch, "E1392", {"start": v(11.29, 11) * mm, "end": v(11.54, 10.75) * mm});
            skLineSegment(sketch, "E1393", {"start": v(11.54, 10.75) * mm, "end": v(16.54, 10.75) * mm});
            skLineSegment(sketch, "E1394", {"start": v(16.54, 10.75) * mm, "end": v(16.79, 11) * mm});
            skLineSegment(sketch, "E1395", {"start": v(16.79, 11) * mm, "end": v(16.79, 16) * mm});
            skArc(sketch, "E1396", {"start": v(16.4, 15.5) * mm, "mid": v(16.04, 15.85) * mm, "end": v(15.69, 15.5) * mm});
            skArc(sketch, "E1397", {"start": v(15.69, 15.5) * mm, "mid": v(16.04, 15.15) * mm, "end": v(16.4, 15.5) * mm});
            skLineSegment(sketch, "E1398", {"start": v(8.79, 12.75) * mm, "end": v(8.29, 13) * mm});
            skLineSegment(sketch, "E1399", {"start": v(8.29, 13) * mm, "end": v(8.29, 12.5) * mm});
            skLineSegment(sketch, "E1400", {"start": v(8.29, 12.5) * mm, "end": v(8.79, 12.75) * mm});
            skLineSegment(sketch, "E1401", {"start": v(13.79, 8.25) * mm, "end": v(14.04, 7.75) * mm});
            skLineSegment(sketch, "E1402", {"start": v(14.04, 7.75) * mm, "end": v(13.54, 7.75) * mm});
            skLineSegment(sketch, "E1403", {"start": v(13.54, 7.75) * mm, "end": v(13.79, 8.25) * mm});
            skLineSegment(sketch, "E1404", {"start": v(12.29, 18.75) * mm, "end": v(12.54, 19.25) * mm});
            skLineSegment(sketch, "E1405", {"start": v(12.54, 19.25) * mm, "end": v(12.04, 19.25) * mm});
            skLineSegment(sketch, "E1406", {"start": v(12.04, 19.25) * mm, "end": v(12.29, 18.75) * mm});
            skLineSegment(sketch, "E1407", {"start": v(19.29, 12.25) * mm, "end": v(19.79, 12) * mm});
            skLineSegment(sketch, "E1408", {"start": v(19.79, 12) * mm, "end": v(19.79, 12.5) * mm});
            skLineSegment(sketch, "E1409", {"start": v(19.79, 12.5) * mm, "end": v(19.29, 12.25) * mm});
            skLineSegment(sketch, "E1410", {"start": v(0.14, -8.5) * mm, "end": v(1.54, -8.5) * mm});
            skArc(sketch, "E1411", {"start": v(1.54, -8.5) * mm, "mid": v(1.73, -8.69) * mm, "end": v(1.54, -8.88) * mm});
            skLineSegment(sketch, "E1412", {"start": v(1.54, -8.88) * mm, "end": v(0.14, -8.88) * mm});
            skArc(sketch, "E1413", {"start": v(0.14, -8.88) * mm, "mid": v(-0.05, -8.69) * mm, "end": v(0.14, -8.5) * mm});
            skLineSegment(sketch, "E1414", {"start": v(0.08, -9.12) * mm, "end": v(1.6, -9.12) * mm});
            skArc(sketch, "E1415", {"start": v(1.6, -9.12) * mm, "mid": v(1.73, -9.25) * mm, "end": v(1.6, -9.38) * mm});
            skLineSegment(sketch, "E1416", {"start": v(1.6, -9.38) * mm, "end": v(0.08, -9.38) * mm});
            skArc(sketch, "E1417", {"start": v(0.08, -9.38) * mm, "mid": v(-0.05, -9.25) * mm, "end": v(0.08, -9.12) * mm});
            skLineSegment(sketch, "E1418", {"start": v(0.08, -9.62) * mm, "end": v(1.6, -9.62) * mm});
            skArc(sketch, "E1419", {"start": v(1.6, -9.62) * mm, "mid": v(1.73, -9.75) * mm, "end": v(1.6, -9.88) * mm});
            skLineSegment(sketch, "E1420", {"start": v(1.6, -9.88) * mm, "end": v(0.08, -9.88) * mm});
            skArc(sketch, "E1421", {"start": v(0.08, -9.88) * mm, "mid": v(-0.05, -9.75) * mm, "end": v(0.08, -9.62) * mm});
            skLineSegment(sketch, "E1422", {"start": v(0.08, -10.12) * mm, "end": v(1.6, -10.12) * mm});
            skArc(sketch, "E1423", {"start": v(1.6, -10.12) * mm, "mid": v(1.73, -10.25) * mm, "end": v(1.6, -10.38) * mm});
            skLineSegment(sketch, "E1424", {"start": v(1.6, -10.38) * mm, "end": v(0.08, -10.38) * mm});
            skArc(sketch, "E1425", {"start": v(0.08, -10.38) * mm, "mid": v(-0.05, -10.25) * mm, "end": v(0.08, -10.12) * mm});
            skLineSegment(sketch, "E1426", {"start": v(0.08, -10.62) * mm, "end": v(1.6, -10.62) * mm});
            skArc(sketch, "E1427", {"start": v(1.6, -10.62) * mm, "mid": v(1.73, -10.75) * mm, "end": v(1.6, -10.88) * mm});
            skLineSegment(sketch, "E1428", {"start": v(1.6, -10.88) * mm, "end": v(0.08, -10.88) * mm});
            skArc(sketch, "E1429", {"start": v(0.08, -10.88) * mm, "mid": v(-0.05, -10.75) * mm, "end": v(0.08, -10.62) * mm});
            skLineSegment(sketch, "E1430", {"start": v(0.08, -11.12) * mm, "end": v(1.6, -11.12) * mm});
            skArc(sketch, "E1431", {"start": v(1.6, -11.12) * mm, "mid": v(1.73, -11.25) * mm, "end": v(1.6, -11.38) * mm});
            skLineSegment(sketch, "E1432", {"start": v(1.6, -11.38) * mm, "end": v(0.08, -11.38) * mm});
            skArc(sketch, "E1433", {"start": v(0.08, -11.38) * mm, "mid": v(-0.05, -11.25) * mm, "end": v(0.08, -11.12) * mm});
            skLineSegment(sketch, "E1434", {"start": v(0.08, -11.62) * mm, "end": v(1.6, -11.62) * mm});
            skArc(sketch, "E1435", {"start": v(1.6, -11.62) * mm, "mid": v(1.73, -11.75) * mm, "end": v(1.6, -11.88) * mm});
            skLineSegment(sketch, "E1436", {"start": v(1.6, -11.88) * mm, "end": v(0.08, -11.88) * mm});
            skArc(sketch, "E1437", {"start": v(0.08, -11.88) * mm, "mid": v(-0.05, -11.75) * mm, "end": v(0.08, -11.62) * mm});
            skLineSegment(sketch, "E1438", {"start": v(0.08, -12.12) * mm, "end": v(1.6, -12.12) * mm});
            skArc(sketch, "E1439", {"start": v(1.6, -12.12) * mm, "mid": v(1.73, -12.25) * mm, "end": v(1.6, -12.38) * mm});
            skLineSegment(sketch, "E1440", {"start": v(1.6, -12.38) * mm, "end": v(0.08, -12.38) * mm});
            skArc(sketch, "E1441", {"start": v(0.08, -12.38) * mm, "mid": v(-0.05, -12.25) * mm, "end": v(0.08, -12.12) * mm});
            skLineSegment(sketch, "E1442", {"start": v(0.08, -12.62) * mm, "end": v(1.6, -12.62) * mm});
            skArc(sketch, "E1443", {"start": v(1.6, -12.62) * mm, "mid": v(1.73, -12.75) * mm, "end": v(1.6, -12.88) * mm});
            skLineSegment(sketch, "E1444", {"start": v(1.6, -12.88) * mm, "end": v(0.08, -12.88) * mm});
            skArc(sketch, "E1445", {"start": v(0.08, -12.88) * mm, "mid": v(-0.05, -12.75) * mm, "end": v(0.08, -12.62) * mm});
            skLineSegment(sketch, "E1446", {"start": v(2.42, -15) * mm, "end": v(2.42, -16.4) * mm});
            skArc(sketch, "E1447", {"start": v(2.42, -16.4) * mm, "mid": v(2.23, -16.59) * mm, "end": v(2.04, -16.4) * mm});
            skLineSegment(sketch, "E1448", {"start": v(2.04, -16.4) * mm, "end": v(2.04, -15) * mm});
            skArc(sketch, "E1449", {"start": v(2.04, -15) * mm, "mid": v(2.23, -14.81) * mm, "end": v(2.42, -15) * mm});
            skLineSegment(sketch, "E1450", {"start": v(2.92, -14.94) * mm, "end": v(2.92, -16.46) * mm});
            skArc(sketch, "E1451", {"start": v(2.92, -16.46) * mm, "mid": v(2.79, -16.59) * mm, "end": v(2.66, -16.46) * mm});
            skLineSegment(sketch, "E1452", {"start": v(2.66, -16.46) * mm, "end": v(2.66, -14.94) * mm});
            skArc(sketch, "E1453", {"start": v(2.66, -14.94) * mm, "mid": v(2.79, -14.81) * mm, "end": v(2.92, -14.94) * mm});
            skLineSegment(sketch, "E1454", {"start": v(3.42, -14.94) * mm, "end": v(3.42, -16.46) * mm});
            skArc(sketch, "E1455", {"start": v(3.42, -16.46) * mm, "mid": v(3.29, -16.59) * mm, "end": v(3.16, -16.46) * mm});
            skLineSegment(sketch, "E1456", {"start": v(3.16, -16.46) * mm, "end": v(3.16, -14.94) * mm});
            skArc(sketch, "E1457", {"start": v(3.16, -14.94) * mm, "mid": v(3.29, -14.81) * mm, "end": v(3.42, -14.94) * mm});
            skLineSegment(sketch, "E1458", {"start": v(3.92, -14.94) * mm, "end": v(3.92, -16.46) * mm});
            skArc(sketch, "E1459", {"start": v(3.92, -16.46) * mm, "mid": v(3.79, -16.59) * mm, "end": v(3.66, -16.46) * mm});
            skLineSegment(sketch, "E1460", {"start": v(3.66, -16.46) * mm, "end": v(3.66, -14.94) * mm});
            skArc(sketch, "E1461", {"start": v(3.66, -14.94) * mm, "mid": v(3.79, -14.81) * mm, "end": v(3.92, -14.94) * mm});
            skLineSegment(sketch, "E1462", {"start": v(4.42, -14.94) * mm, "end": v(4.42, -16.46) * mm});
            skArc(sketch, "E1463", {"start": v(4.42, -16.46) * mm, "mid": v(4.29, -16.59) * mm, "end": v(4.16, -16.46) * mm});
            skLineSegment(sketch, "E1464", {"start": v(4.16, -16.46) * mm, "end": v(4.16, -14.94) * mm});
            skArc(sketch, "E1465", {"start": v(4.16, -14.94) * mm, "mid": v(4.29, -14.81) * mm, "end": v(4.42, -14.94) * mm});
            skLineSegment(sketch, "E1466", {"start": v(5.92, -14.94) * mm, "end": v(5.92, -16.46) * mm});
            skArc(sketch, "E1467", {"start": v(5.92, -16.46) * mm, "mid": v(5.79, -16.59) * mm, "end": v(5.66, -16.46) * mm});
            skLineSegment(sketch, "E1468", {"start": v(5.66, -16.46) * mm, "end": v(5.66, -14.94) * mm});
            skArc(sketch, "E1469", {"start": v(5.66, -14.94) * mm, "mid": v(5.79, -14.81) * mm, "end": v(5.92, -14.94) * mm});
            skLineSegment(sketch, "E1470", {"start": v(6.42, -14.94) * mm, "end": v(6.42, -16.46) * mm});
            skArc(sketch, "E1471", {"start": v(6.42, -16.46) * mm, "mid": v(6.29, -16.59) * mm, "end": v(6.16, -16.46) * mm});
            skLineSegment(sketch, "E1472", {"start": v(6.16, -16.46) * mm, "end": v(6.16, -14.94) * mm});
            skArc(sketch, "E1473", {"start": v(6.16, -14.94) * mm, "mid": v(6.29, -14.81) * mm, "end": v(6.42, -14.94) * mm});
            skLineSegment(sketch, "E1474", {"start": v(6.92, -14.94) * mm, "end": v(6.92, -16.46) * mm});
            skArc(sketch, "E1475", {"start": v(6.92, -16.46) * mm, "mid": v(6.79, -16.59) * mm, "end": v(6.66, -16.46) * mm});
            skLineSegment(sketch, "E1476", {"start": v(6.66, -16.46) * mm, "end": v(6.66, -14.94) * mm});
            skArc(sketch, "E1477", {"start": v(6.66, -14.94) * mm, "mid": v(6.79, -14.81) * mm, "end": v(6.92, -14.94) * mm});
            skLineSegment(sketch, "E1478", {"start": v(7.42, -14.94) * mm, "end": v(7.42, -16.46) * mm});
            skArc(sketch, "E1479", {"start": v(7.42, -16.46) * mm, "mid": v(7.29, -16.59) * mm, "end": v(7.16, -16.46) * mm});
            skLineSegment(sketch, "E1480", {"start": v(7.16, -16.46) * mm, "end": v(7.16, -14.94) * mm});
            skArc(sketch, "E1481", {"start": v(7.16, -14.94) * mm, "mid": v(7.29, -14.81) * mm, "end": v(7.42, -14.94) * mm});
            skLineSegment(sketch, "E1482", {"start": v(8.04, -15) * mm, "end": v(8.04, -16.4) * mm});
            skArc(sketch, "E1483", {"start": v(8.04, -16.4) * mm, "mid": v(7.85, -16.59) * mm, "end": v(7.66, -16.4) * mm});
            skLineSegment(sketch, "E1484", {"start": v(7.66, -16.4) * mm, "end": v(7.66, -15) * mm});
            skArc(sketch, "E1485", {"start": v(7.66, -15) * mm, "mid": v(7.85, -14.81) * mm, "end": v(8.04, -15) * mm});
            skLineSegment(sketch, "E1486", {"start": v(8.54, -14.12) * mm, "end": v(9.94, -14.12) * mm});
            skArc(sketch, "E1487", {"start": v(9.94, -14.12) * mm, "mid": v(10.13, -14.31) * mm, "end": v(9.94, -14.5) * mm});
            skLineSegment(sketch, "E1488", {"start": v(9.94, -14.5) * mm, "end": v(8.54, -14.5) * mm});
            skArc(sketch, "E1489", {"start": v(8.54, -14.5) * mm, "mid": v(8.35, -14.31) * mm, "end": v(8.54, -14.12) * mm});
            skLineSegment(sketch, "E1490", {"start": v(8.48, -13.62) * mm, "end": v(10, -13.62) * mm});
            skArc(sketch, "E1491", {"start": v(10, -13.62) * mm, "mid": v(10.13, -13.75) * mm, "end": v(10, -13.88) * mm});
            skLineSegment(sketch, "E1492", {"start": v(10, -13.88) * mm, "end": v(8.48, -13.88) * mm});
            skArc(sketch, "E1493", {"start": v(8.48, -13.88) * mm, "mid": v(8.35, -13.75) * mm, "end": v(8.48, -13.62) * mm});
            skLineSegment(sketch, "E1494", {"start": v(8.48, -13.12) * mm, "end": v(10, -13.12) * mm});
            skArc(sketch, "E1495", {"start": v(10, -13.12) * mm, "mid": v(10.13, -13.25) * mm, "end": v(10, -13.38) * mm});
            skLineSegment(sketch, "E1496", {"start": v(10, -13.38) * mm, "end": v(8.48, -13.38) * mm});
            skArc(sketch, "E1497", {"start": v(8.48, -13.38) * mm, "mid": v(8.35, -13.25) * mm, "end": v(8.48, -13.12) * mm});
            skLineSegment(sketch, "E1498", {"start": v(8.48, -12.62) * mm, "end": v(10, -12.62) * mm});
            skArc(sketch, "E1499", {"start": v(10, -12.62) * mm, "mid": v(10.13, -12.75) * mm, "end": v(10, -12.88) * mm});
            skLineSegment(sketch, "E1500", {"start": v(10, -12.88) * mm, "end": v(8.48, -12.88) * mm});
            skArc(sketch, "E1501", {"start": v(8.48, -12.88) * mm, "mid": v(8.35, -12.75) * mm, "end": v(8.48, -12.62) * mm});
            skLineSegment(sketch, "E1502", {"start": v(8.48, -12.12) * mm, "end": v(10, -12.12) * mm});
            skArc(sketch, "E1503", {"start": v(10, -12.12) * mm, "mid": v(10.13, -12.25) * mm, "end": v(10, -12.38) * mm});
            skLineSegment(sketch, "E1504", {"start": v(10, -12.38) * mm, "end": v(8.48, -12.38) * mm});
            skArc(sketch, "E1505", {"start": v(8.48, -12.38) * mm, "mid": v(8.35, -12.25) * mm, "end": v(8.48, -12.12) * mm});
            skLineSegment(sketch, "E1506", {"start": v(8.48, -10.62) * mm, "end": v(10, -10.62) * mm});
            skArc(sketch, "E1507", {"start": v(10, -10.62) * mm, "mid": v(10.13, -10.75) * mm, "end": v(10, -10.88) * mm});
            skLineSegment(sketch, "E1508", {"start": v(10, -10.88) * mm, "end": v(8.48, -10.88) * mm});
            skArc(sketch, "E1509", {"start": v(8.48, -10.88) * mm, "mid": v(8.35, -10.75) * mm, "end": v(8.48, -10.62) * mm});
            skLineSegment(sketch, "E1510", {"start": v(8.48, -10.12) * mm, "end": v(10, -10.12) * mm});
            skArc(sketch, "E1511", {"start": v(10, -10.12) * mm, "mid": v(10.13, -10.25) * mm, "end": v(10, -10.38) * mm});
            skLineSegment(sketch, "E1512", {"start": v(10, -10.38) * mm, "end": v(8.48, -10.38) * mm});
            skArc(sketch, "E1513", {"start": v(8.48, -10.38) * mm, "mid": v(8.35, -10.25) * mm, "end": v(8.48, -10.12) * mm});
            skLineSegment(sketch, "E1514", {"start": v(8.48, -9.62) * mm, "end": v(10, -9.62) * mm});
            skArc(sketch, "E1515", {"start": v(10, -9.62) * mm, "mid": v(10.13, -9.75) * mm, "end": v(10, -9.88) * mm});
            skLineSegment(sketch, "E1516", {"start": v(10, -9.88) * mm, "end": v(8.48, -9.88) * mm});
            skArc(sketch, "E1517", {"start": v(8.48, -9.88) * mm, "mid": v(8.35, -9.75) * mm, "end": v(8.48, -9.62) * mm});
            skLineSegment(sketch, "E1518", {"start": v(8.48, -9.12) * mm, "end": v(10, -9.12) * mm});
            skArc(sketch, "E1519", {"start": v(10, -9.12) * mm, "mid": v(10.13, -9.25) * mm, "end": v(10, -9.38) * mm});
            skLineSegment(sketch, "E1520", {"start": v(10, -9.38) * mm, "end": v(8.48, -9.38) * mm});
            skArc(sketch, "E1521", {"start": v(8.48, -9.38) * mm, "mid": v(8.35, -9.25) * mm, "end": v(8.48, -9.12) * mm});
            skLineSegment(sketch, "E1522", {"start": v(8.54, -8.5) * mm, "end": v(9.94, -8.5) * mm});
            skArc(sketch, "E1523", {"start": v(9.94, -8.5) * mm, "mid": v(10.13, -8.69) * mm, "end": v(9.94, -8.88) * mm});
            skLineSegment(sketch, "E1524", {"start": v(9.94, -8.88) * mm, "end": v(8.54, -8.88) * mm});
            skArc(sketch, "E1525", {"start": v(8.54, -8.88) * mm, "mid": v(8.35, -8.69) * mm, "end": v(8.54, -8.5) * mm});
            skLineSegment(sketch, "E1526", {"start": v(8.04, -6.6) * mm, "end": v(8.04, -8) * mm});
            skArc(sketch, "E1527", {"start": v(8.04, -8) * mm, "mid": v(7.85, -8.19) * mm, "end": v(7.66, -8) * mm});
            skLineSegment(sketch, "E1528", {"start": v(7.66, -8) * mm, "end": v(7.66, -6.6) * mm});
            skArc(sketch, "E1529", {"start": v(7.66, -6.6) * mm, "mid": v(7.85, -6.41) * mm, "end": v(8.04, -6.6) * mm});
            skLineSegment(sketch, "E1530", {"start": v(7.42, -6.54) * mm, "end": v(7.42, -8.06) * mm});
            skArc(sketch, "E1531", {"start": v(7.42, -8.06) * mm, "mid": v(7.29, -8.19) * mm, "end": v(7.16, -8.06) * mm});
            skLineSegment(sketch, "E1532", {"start": v(7.16, -8.06) * mm, "end": v(7.16, -6.54) * mm});
            skArc(sketch, "E1533", {"start": v(7.16, -6.54) * mm, "mid": v(7.29, -6.41) * mm, "end": v(7.42, -6.54) * mm});
            skLineSegment(sketch, "E1534", {"start": v(6.92, -6.54) * mm, "end": v(6.92, -8.06) * mm});
            skArc(sketch, "E1535", {"start": v(6.92, -8.06) * mm, "mid": v(6.79, -8.19) * mm, "end": v(6.66, -8.06) * mm});
            skLineSegment(sketch, "E1536", {"start": v(6.66, -8.06) * mm, "end": v(6.66, -6.54) * mm});
            skArc(sketch, "E1537", {"start": v(6.66, -6.54) * mm, "mid": v(6.79, -6.41) * mm, "end": v(6.92, -6.54) * mm});
            skLineSegment(sketch, "E1538", {"start": v(6.42, -6.54) * mm, "end": v(6.42, -8.06) * mm});
            skArc(sketch, "E1539", {"start": v(6.42, -8.06) * mm, "mid": v(6.29, -8.19) * mm, "end": v(6.16, -8.06) * mm});
            skLineSegment(sketch, "E1540", {"start": v(6.16, -8.06) * mm, "end": v(6.16, -6.54) * mm});
            skArc(sketch, "E1541", {"start": v(6.16, -6.54) * mm, "mid": v(6.29, -6.41) * mm, "end": v(6.42, -6.54) * mm});
            skLineSegment(sketch, "E1542", {"start": v(5.92, -6.54) * mm, "end": v(5.92, -8.06) * mm});
            skArc(sketch, "E1543", {"start": v(5.92, -8.06) * mm, "mid": v(5.79, -8.19) * mm, "end": v(5.66, -8.06) * mm});
            skLineSegment(sketch, "E1544", {"start": v(5.66, -8.06) * mm, "end": v(5.66, -6.54) * mm});
            skArc(sketch, "E1545", {"start": v(5.66, -6.54) * mm, "mid": v(5.79, -6.41) * mm, "end": v(5.92, -6.54) * mm});
            skLineSegment(sketch, "E1546", {"start": v(4.42, -6.54) * mm, "end": v(4.42, -8.06) * mm});
            skArc(sketch, "E1547", {"start": v(4.42, -8.06) * mm, "mid": v(4.29, -8.19) * mm, "end": v(4.16, -8.06) * mm});
            skLineSegment(sketch, "E1548", {"start": v(4.16, -8.06) * mm, "end": v(4.16, -6.54) * mm});
            skArc(sketch, "E1549", {"start": v(4.16, -6.54) * mm, "mid": v(4.29, -6.41) * mm, "end": v(4.42, -6.54) * mm});
            skLineSegment(sketch, "E1550", {"start": v(3.92, -6.54) * mm, "end": v(3.92, -8.06) * mm});
            skArc(sketch, "E1551", {"start": v(3.92, -8.06) * mm, "mid": v(3.79, -8.19) * mm, "end": v(3.66, -8.06) * mm});
            skLineSegment(sketch, "E1552", {"start": v(3.66, -8.06) * mm, "end": v(3.66, -6.54) * mm});
            skArc(sketch, "E1553", {"start": v(3.66, -6.54) * mm, "mid": v(3.79, -6.41) * mm, "end": v(3.92, -6.54) * mm});
            skLineSegment(sketch, "E1554", {"start": v(3.42, -6.54) * mm, "end": v(3.42, -8.06) * mm});
            skArc(sketch, "E1555", {"start": v(3.42, -8.06) * mm, "mid": v(3.29, -8.19) * mm, "end": v(3.16, -8.06) * mm});
            skLineSegment(sketch, "E1556", {"start": v(3.16, -8.06) * mm, "end": v(3.16, -6.54) * mm});
            skArc(sketch, "E1557", {"start": v(3.16, -6.54) * mm, "mid": v(3.29, -6.41) * mm, "end": v(3.42, -6.54) * mm});
            skLineSegment(sketch, "E1558", {"start": v(2.92, -6.54) * mm, "end": v(2.92, -8.06) * mm});
            skArc(sketch, "E1559", {"start": v(2.92, -8.06) * mm, "mid": v(2.79, -8.19) * mm, "end": v(2.66, -8.06) * mm});
            skLineSegment(sketch, "E1560", {"start": v(2.66, -8.06) * mm, "end": v(2.66, -6.54) * mm});
            skArc(sketch, "E1561", {"start": v(2.66, -6.54) * mm, "mid": v(2.79, -6.41) * mm, "end": v(2.92, -6.54) * mm});
            skLineSegment(sketch, "E1562", {"start": v(2.42, -6.6) * mm, "end": v(2.42, -8) * mm});
            skArc(sketch, "E1563", {"start": v(2.42, -8) * mm, "mid": v(2.23, -8.19) * mm, "end": v(2.04, -8) * mm});
            skLineSegment(sketch, "E1564", {"start": v(2.04, -8) * mm, "end": v(2.04, -6.6) * mm});
            skArc(sketch, "E1565", {"start": v(2.04, -6.6) * mm, "mid": v(2.23, -6.41) * mm, "end": v(2.42, -6.6) * mm});
            skLineSegment(sketch, "E1566", {"start": v(0.08, -13.12) * mm, "end": v(1.6, -13.12) * mm});
            skArc(sketch, "E1567", {"start": v(1.6, -13.12) * mm, "mid": v(1.73, -13.25) * mm, "end": v(1.6, -13.38) * mm});
            skLineSegment(sketch, "E1568", {"start": v(1.6, -13.38) * mm, "end": v(0.08, -13.38) * mm});
            skArc(sketch, "E1569", {"start": v(0.08, -13.38) * mm, "mid": v(-0.05, -13.25) * mm, "end": v(0.08, -13.12) * mm});
            skLineSegment(sketch, "E1570", {"start": v(0.08, -13.62) * mm, "end": v(1.6, -13.62) * mm});
            skArc(sketch, "E1571", {"start": v(1.6, -13.62) * mm, "mid": v(1.73, -13.75) * mm, "end": v(1.6, -13.88) * mm});
            skLineSegment(sketch, "E1572", {"start": v(1.6, -13.88) * mm, "end": v(0.08, -13.88) * mm});
            skArc(sketch, "E1573", {"start": v(0.08, -13.88) * mm, "mid": v(-0.05, -13.75) * mm, "end": v(0.08, -13.62) * mm});
            skLineSegment(sketch, "E1574", {"start": v(0.14, -14.12) * mm, "end": v(1.54, -14.12) * mm});
            skArc(sketch, "E1575", {"start": v(1.54, -14.12) * mm, "mid": v(1.73, -14.31) * mm, "end": v(1.54, -14.5) * mm});
            skLineSegment(sketch, "E1576", {"start": v(1.54, -14.5) * mm, "end": v(0.14, -14.5) * mm});
            skArc(sketch, "E1577", {"start": v(0.14, -14.5) * mm, "mid": v(-0.05, -14.31) * mm, "end": v(0.14, -14.12) * mm});
            skLineSegment(sketch, "E1578", {"start": v(5.42, -14.94) * mm, "end": v(5.42, -16.46) * mm});
            skArc(sketch, "E1579", {"start": v(5.42, -16.46) * mm, "mid": v(5.29, -16.59) * mm, "end": v(5.16, -16.46) * mm});
            skLineSegment(sketch, "E1580", {"start": v(5.16, -16.46) * mm, "end": v(5.16, -14.94) * mm});
            skArc(sketch, "E1581", {"start": v(5.16, -14.94) * mm, "mid": v(5.29, -14.81) * mm, "end": v(5.42, -14.94) * mm});
            skLineSegment(sketch, "E1582", {"start": v(4.92, -14.94) * mm, "end": v(4.92, -16.46) * mm});
            skArc(sketch, "E1583", {"start": v(4.92, -16.46) * mm, "mid": v(4.79, -16.59) * mm, "end": v(4.66, -16.46) * mm});
            skLineSegment(sketch, "E1584", {"start": v(4.66, -16.46) * mm, "end": v(4.66, -14.94) * mm});
            skArc(sketch, "E1585", {"start": v(4.66, -14.94) * mm, "mid": v(4.79, -14.81) * mm, "end": v(4.92, -14.94) * mm});
            skLineSegment(sketch, "E1586", {"start": v(8.48, -11.12) * mm, "end": v(10, -11.12) * mm});
            skArc(sketch, "E1587", {"start": v(10, -11.12) * mm, "mid": v(10.13, -11.25) * mm, "end": v(10, -11.38) * mm});
            skLineSegment(sketch, "E1588", {"start": v(10, -11.38) * mm, "end": v(8.48, -11.38) * mm});
            skArc(sketch, "E1589", {"start": v(8.48, -11.38) * mm, "mid": v(8.35, -11.25) * mm, "end": v(8.48, -11.12) * mm});
            skLineSegment(sketch, "E1590", {"start": v(8.48, -11.62) * mm, "end": v(10, -11.62) * mm});
            skArc(sketch, "E1591", {"start": v(10, -11.62) * mm, "mid": v(10.13, -11.75) * mm, "end": v(10, -11.88) * mm});
            skLineSegment(sketch, "E1592", {"start": v(10, -11.88) * mm, "end": v(8.48, -11.88) * mm});
            skArc(sketch, "E1593", {"start": v(8.48, -11.88) * mm, "mid": v(8.35, -11.75) * mm, "end": v(8.48, -11.62) * mm});
            skLineSegment(sketch, "E1594", {"start": v(4.92, -6.54) * mm, "end": v(4.92, -8.06) * mm});
            skArc(sketch, "E1595", {"start": v(4.92, -8.06) * mm, "mid": v(4.79, -8.19) * mm, "end": v(4.66, -8.06) * mm});
            skLineSegment(sketch, "E1596", {"start": v(4.66, -8.06) * mm, "end": v(4.66, -6.54) * mm});
            skArc(sketch, "E1597", {"start": v(4.66, -6.54) * mm, "mid": v(4.79, -6.41) * mm, "end": v(4.92, -6.54) * mm});
            skLineSegment(sketch, "E1598", {"start": v(5.42, -6.54) * mm, "end": v(5.42, -8.06) * mm});
            skArc(sketch, "E1599", {"start": v(5.42, -8.06) * mm, "mid": v(5.29, -8.19) * mm, "end": v(5.16, -8.06) * mm});
            skLineSegment(sketch, "E1600", {"start": v(5.16, -8.06) * mm, "end": v(5.16, -6.54) * mm});
            skArc(sketch, "E1601", {"start": v(5.16, -6.54) * mm, "mid": v(5.29, -6.41) * mm, "end": v(5.42, -6.54) * mm});
            skArc(sketch, "E1602", {"start": v(-0.21, -8.75) * mm, "mid": v(-0.46, -8.5) * mm, "end": v(-0.71, -8.75) * mm});
            skArc(sketch, "E1603", {"start": v(-0.71, -8.75) * mm, "mid": v(-0.46, -9) * mm, "end": v(-0.21, -8.75) * mm});
            skLineSegment(sketch, "E1604", {"start": v(-0.21, -10.75) * mm, "end": v(-0.71, -10.75) * mm});
            skLineSegment(sketch, "E1605", {"start": v(10.29, -14.25) * mm, "end": v(10.79, -14.25) * mm});
            skLineSegment(sketch, "E1606", {"start": v(3.79, -6.25) * mm, "end": v(3.79, -5.75) * mm});
            skLineSegment(sketch, "E1607", {"start": v(3.29, -17.25) * mm, "end": v(3.29, -16.75) * mm});
            skLineSegment(sketch, "E1608", {"start": v(10.29, -9.25) * mm, "end": v(10.79, -9.25) * mm});
            skLineSegment(sketch, "E1609", {"start": v(4.54, -11.5) * mm, "end": v(5.54, -11.5) * mm});
            skLineSegment(sketch, "E1610", {"start": v(5.04, -11) * mm, "end": v(5.04, -12) * mm});
            skLineSegment(sketch, "E1611", {"start": v(2.54, -8.75) * mm, "end": v(2.29, -9) * mm});
            skLineSegment(sketch, "E1612", {"start": v(2.29, -9) * mm, "end": v(2.29, -14) * mm});
            skLineSegment(sketch, "E1613", {"start": v(2.29, -14) * mm, "end": v(2.54, -14.25) * mm});
            skLineSegment(sketch, "E1614", {"start": v(2.54, -14.25) * mm, "end": v(7.54, -14.25) * mm});
            skLineSegment(sketch, "E1615", {"start": v(7.54, -14.25) * mm, "end": v(7.79, -14) * mm});
            skLineSegment(sketch, "E1616", {"start": v(7.79, -14) * mm, "end": v(7.79, -9) * mm});
            skLineSegment(sketch, "E1617", {"start": v(7.79, -9) * mm, "end": v(7.54, -8.75) * mm});
            skLineSegment(sketch, "E1618", {"start": v(7.54, -8.75) * mm, "end": v(2.54, -8.75) * mm});
            skArc(sketch, "E1619", {"start": v(3.4, -9.5) * mm, "mid": v(3.04, -9.15) * mm, "end": v(2.69, -9.5) * mm});
            skArc(sketch, "E1620", {"start": v(2.69, -9.5) * mm, "mid": v(3.04, -9.85) * mm, "end": v(3.4, -9.5) * mm});
            skLineSegment(sketch, "E1621", {"start": v(5.79, -16.75) * mm, "end": v(5.54, -17.25) * mm});
            skLineSegment(sketch, "E1622", {"start": v(5.54, -17.25) * mm, "end": v(6.04, -17.25) * mm});
            skLineSegment(sketch, "E1623", {"start": v(6.04, -17.25) * mm, "end": v(5.79, -16.75) * mm});
            skLineSegment(sketch, "E1624", {"start": v(10.29, -11.75) * mm, "end": v(10.79, -11.5) * mm});
            skLineSegment(sketch, "E1625", {"start": v(10.79, -11.5) * mm, "end": v(10.79, -12) * mm});
            skLineSegment(sketch, "E1626", {"start": v(10.79, -12) * mm, "end": v(10.29, -11.75) * mm});
            skLineSegment(sketch, "E1627", {"start": v(-0.21, -13.25) * mm, "end": v(-0.71, -13) * mm});
            skLineSegment(sketch, "E1628", {"start": v(-0.71, -13) * mm, "end": v(-0.71, -13.5) * mm});
            skLineSegment(sketch, "E1629", {"start": v(-0.71, -13.5) * mm, "end": v(-0.21, -13.25) * mm});
            skLineSegment(sketch, "E1630", {"start": v(6.29, -6.25) * mm, "end": v(6.54, -5.75) * mm});
            skLineSegment(sketch, "E1631", {"start": v(6.54, -5.75) * mm, "end": v(6.04, -5.75) * mm});
            skLineSegment(sketch, "E1632", {"start": v(6.04, -5.75) * mm, "end": v(6.29, -6.25) * mm});
            skCircle(sketch, "E1633", {"center": v(26.51, -1) * mm, "radius": 1.97 * mm});
            skCircle(sketch, "E1634", {"center": v(26.51, -26) * mm, "radius": 1.97 * mm});
            skCircle(sketch, "E1635", {"center": v(25.1, -8.01) * mm, "radius": 0.76 * mm});
            skCircle(sketch, "E1636", {"center": v(25.1, -10.76) * mm, "radius": 0.76 * mm});
            skCircle(sketch, "E1637", {"center": v(25.1, -13.5) * mm, "radius": 0.76 * mm});
            skCircle(sketch, "E1638", {"center": v(25.1, -16.24) * mm, "radius": 0.76 * mm});
            skLineSegment(sketch, "E1639", {"start": v(24.33, -18.22) * mm, "end": v(25.85, -18.22) * mm});
            skLineSegment(sketch, "E1640", {"start": v(25.85, -18.22) * mm, "end": v(25.85, -19.75) * mm});
            skLineSegment(sketch, "E1641", {"start": v(25.85, -19.75) * mm, "end": v(24.33, -19.75) * mm});
            skLineSegment(sketch, "E1642", {"start": v(24.33, -19.75) * mm, "end": v(24.33, -18.22) * mm});
            skCircle(sketch, "E1643", {"center": v(27.94, -9.39) * mm, "radius": 0.76 * mm});
            skCircle(sketch, "E1644", {"center": v(27.94, -12.13) * mm, "radius": 0.76 * mm});
            skCircle(sketch, "E1645", {"center": v(27.94, -14.87) * mm, "radius": 0.76 * mm});
            skCircle(sketch, "E1646", {"center": v(27.94, -17.61) * mm, "radius": 0.76 * mm});
            skLineSegment(sketch, "E1647", {"start": v(23.34, 2) * mm, "end": v(36.04, 2) * mm});
            skLineSegment(sketch, "E1648", {"start": v(36.04, 2) * mm, "end": v(36.04, -29) * mm});
            skLineSegment(sketch, "E1649", {"start": v(36.04, -29) * mm, "end": v(23.34, -29) * mm});
            skLineSegment(sketch, "E1650", {"start": v(23.34, -29) * mm, "end": v(23.34, 2) * mm});
            skLineSegment(sketch, "E1651", {"start": v(36.04, -4.6) * mm, "end": v(42.14, -4.6) * mm});
            skLineSegment(sketch, "E1652", {"start": v(42.14, -4.6) * mm, "end": v(42.14, -22.4) * mm});
            skLineSegment(sketch, "E1653", {"start": v(42.14, -22.4) * mm, "end": v(36.04, -22.4) * mm});
            skLineSegment(sketch, "E1654", {"start": v(36.04, -22.4) * mm, "end": v(36.04, -4.6) * mm});
            skCircle(sketch, "E1655", {"center": v(2.54, 10) * mm, "radius": 1.5 * mm});
            skCircle(sketch, "E1656", {"center": v(6.04, 10) * mm, "radius": 1.5 * mm});
            skCircle(sketch, "E1657", {"center": v(-0.96, 10) * mm, "radius": 1.5 * mm});
            skCircle(sketch, "E1658", {"center": v(-4.46, 10) * mm, "radius": 1.5 * mm});
            skLineSegment(sketch, "E1659", {"start": v(8.54, 11.75) * mm, "end": v(8.54, 3.6) * mm});
            skLineSegment(sketch, "E1660", {"start": v(8.54, 3.6) * mm, "end": v(-6.96, 3.6) * mm});
            skLineSegment(sketch, "E1661", {"start": v(-6.96, 3.6) * mm, "end": v(-6.96, 11.75) * mm});
            skLineSegment(sketch, "E1662", {"start": v(-6.96, 11.75) * mm, "end": v(8.54, 11.75) * mm});
            skCircle(sketch, "E1663", {"center": v(-13.46, 10) * mm, "radius": 1.5 * mm});
            skCircle(sketch, "E1664", {"center": v(-9.96, 10) * mm, "radius": 1.5 * mm});
            skCircle(sketch, "E1665", {"center": v(-16.96, 10) * mm, "radius": 1.5 * mm});
            skCircle(sketch, "E1666", {"center": v(-20.46, 10) * mm, "radius": 1.5 * mm});
            skLineSegment(sketch, "E1667", {"start": v(-7.46, 11.75) * mm, "end": v(-7.46, 3.6) * mm});
            skLineSegment(sketch, "E1668", {"start": v(-7.46, 3.6) * mm, "end": v(-22.96, 3.6) * mm});
            skLineSegment(sketch, "E1669", {"start": v(-22.96, 3.6) * mm, "end": v(-22.96, 11.75) * mm});
            skLineSegment(sketch, "E1670", {"start": v(-22.96, 11.75) * mm, "end": v(-7.46, 11.75) * mm});
            skCircle(sketch, "E1671", {"center": v(-18.96, -20) * mm, "radius": 1.5 * mm});
            skCircle(sketch, "E1672", {"center": v(-18.96, -16.5) * mm, "radius": 1.5 * mm});
            skCircle(sketch, "E1673", {"center": v(-18.96, -23.5) * mm, "radius": 1.5 * mm});
            skCircle(sketch, "E1674", {"center": v(-18.96, -27) * mm, "radius": 1.5 * mm});
            skLineSegment(sketch, "E1675", {"start": v(-17.21, -14) * mm, "end": v(-26.86, -14) * mm});
            skLineSegment(sketch, "E1676", {"start": v(-26.86, -14) * mm, "end": v(-26.86, -29.5) * mm});
            skLineSegment(sketch, "E1677", {"start": v(-26.86, -29.5) * mm, "end": v(-17.21, -29.5) * mm});
            skLineSegment(sketch, "E1678", {"start": v(-17.21, -29.5) * mm, "end": v(-17.21, -14) * mm});
            skCircle(sketch, "E1679", {"center": v(-18.96, -3.5) * mm, "radius": 1.5 * mm});
            skCircle(sketch, "E1680", {"center": v(-18.96, 0) * mm, "radius": 1.5 * mm});
            skCircle(sketch, "E1681", {"center": v(-18.96, -7) * mm, "radius": 1.5 * mm});
            skCircle(sketch, "E1682", {"center": v(-18.96, -10.5) * mm, "radius": 1.5 * mm});
            skLineSegment(sketch, "E1683", {"start": v(-17.21, 2.5) * mm, "end": v(-26.86, 2.5) * mm});
            skLineSegment(sketch, "E1684", {"start": v(-26.86, 2.5) * mm, "end": v(-26.86, -13) * mm});
            skLineSegment(sketch, "E1685", {"start": v(-26.86, -13) * mm, "end": v(-17.21, -13) * mm});
            skLineSegment(sketch, "E1686", {"start": v(-17.21, -13) * mm, "end": v(-17.21, 2.5) * mm});
            skLineSegment(sketch, "E1687", {"start": v(13.41, 31) * mm, "end": v(15.01, 31) * mm});
            skLineSegment(sketch, "E1688", {"start": v(15.01, 31) * mm, "end": v(15.01, 28) * mm});
            skLineSegment(sketch, "E1689", {"start": v(15.01, 28) * mm, "end": v(13.41, 28) * mm});
            skLineSegment(sketch, "E1690", {"start": v(13.41, 28) * mm, "end": v(13.41, 31) * mm});
            skLineSegment(sketch, "E1691", {"start": v(7.06, 27.79) * mm, "end": v(8.66, 27.79) * mm});
            skLineSegment(sketch, "E1692", {"start": v(8.66, 27.79) * mm, "end": v(8.66, 26.59) * mm});
            skLineSegment(sketch, "E1693", {"start": v(8.66, 26.59) * mm, "end": v(7.06, 26.59) * mm});
            skLineSegment(sketch, "E1694", {"start": v(7.06, 26.59) * mm, "end": v(7.06, 27.79) * mm});
            skLineSegment(sketch, "E1695", {"start": v(7.06, 30.1) * mm, "end": v(8.66, 30.1) * mm});
            skLineSegment(sketch, "E1696", {"start": v(8.66, 30.1) * mm, "end": v(8.66, 28.9) * mm});
            skLineSegment(sketch, "E1697", {"start": v(8.66, 28.9) * mm, "end": v(7.06, 28.9) * mm});
            skLineSegment(sketch, "E1698", {"start": v(7.06, 28.9) * mm, "end": v(7.06, 30.1) * mm});
            skLineSegment(sketch, "E1699", {"start": v(7.06, 32.41) * mm, "end": v(8.66, 32.41) * mm});
            skLineSegment(sketch, "E1700", {"start": v(8.66, 32.41) * mm, "end": v(8.66, 31.21) * mm});
            skLineSegment(sketch, "E1701", {"start": v(8.66, 31.21) * mm, "end": v(7.06, 31.21) * mm});
            skLineSegment(sketch, "E1702", {"start": v(7.06, 31.21) * mm, "end": v(7.06, 32.41) * mm});
            skLineSegment(sketch, "E1703", {"start": v(9.39, 26.33) * mm, "end": v(9.39, 32.67) * mm});
            skLineSegment(sketch, "E1704", {"start": v(12.7, 26.33) * mm, "end": v(9.39, 26.33) * mm});
            skLineSegment(sketch, "E1705", {"start": v(12.7, 32.67) * mm, "end": v(12.7, 26.33) * mm});
            skLineSegment(sketch, "E1706", {"start": v(9.39, 32.67) * mm, "end": v(12.7, 32.67) * mm});
            skLineSegment(sketch, "E1707", {"start": v(-3.09, -24.5) * mm, "end": v(-1.49, -24.5) * mm});
            skLineSegment(sketch, "E1708", {"start": v(-1.49, -24.5) * mm, "end": v(-1.49, -27.5) * mm});
            skLineSegment(sketch, "E1709", {"start": v(-1.49, -27.5) * mm, "end": v(-3.09, -27.5) * mm});
            skLineSegment(sketch, "E1710", {"start": v(-3.09, -27.5) * mm, "end": v(-3.09, -24.5) * mm});
            skLineSegment(sketch, "E1711", {"start": v(-9.44, -27.71) * mm, "end": v(-7.84, -27.71) * mm});
            skLineSegment(sketch, "E1712", {"start": v(-7.84, -27.71) * mm, "end": v(-7.84, -28.91) * mm});
            skLineSegment(sketch, "E1713", {"start": v(-7.84, -28.91) * mm, "end": v(-9.44, -28.91) * mm});
            skLineSegment(sketch, "E1714", {"start": v(-9.44, -28.91) * mm, "end": v(-9.44, -27.71) * mm});
            skLineSegment(sketch, "E1715", {"start": v(-9.44, -25.4) * mm, "end": v(-7.84, -25.4) * mm});
            skLineSegment(sketch, "E1716", {"start": v(-7.84, -25.4) * mm, "end": v(-7.84, -26.6) * mm});
            skLineSegment(sketch, "E1717", {"start": v(-7.84, -26.6) * mm, "end": v(-9.44, -26.6) * mm});
            skLineSegment(sketch, "E1718", {"start": v(-9.44, -26.6) * mm, "end": v(-9.44, -25.4) * mm});
            skLineSegment(sketch, "E1719", {"start": v(-9.44, -23.09) * mm, "end": v(-7.84, -23.09) * mm});
            skLineSegment(sketch, "E1720", {"start": v(-7.84, -23.09) * mm, "end": v(-7.84, -24.29) * mm});
            skLineSegment(sketch, "E1721", {"start": v(-7.84, -24.29) * mm, "end": v(-9.44, -24.29) * mm});
            skLineSegment(sketch, "E1722", {"start": v(-9.44, -24.29) * mm, "end": v(-9.44, -23.09) * mm});
            skLineSegment(sketch, "E1723", {"start": v(-7.11, -29.18) * mm, "end": v(-7.11, -22.82) * mm});
            skLineSegment(sketch, "E1724", {"start": v(-3.8, -29.18) * mm, "end": v(-7.11, -29.18) * mm});
            skLineSegment(sketch, "E1725", {"start": v(-3.8, -22.82) * mm, "end": v(-3.8, -29.18) * mm});
            skLineSegment(sketch, "E1726", {"start": v(-7.11, -22.82) * mm, "end": v(-3.8, -22.82) * mm});
            skLineSegment(sketch, "E1727", {"start": v(19.04, 8.75) * mm, "end": v(20.04, 8.75) * mm});
            skLineSegment(sketch, "E1728", {"start": v(20.04, 8.75) * mm, "end": v(20.04, 7.75) * mm});
            skLineSegment(sketch, "E1729", {"start": v(20.04, 7.75) * mm, "end": v(19.04, 7.75) * mm});
            skLineSegment(sketch, "E1730", {"start": v(19.04, 7.75) * mm, "end": v(19.04, 8.75) * mm});
            skLineSegment(sketch, "E1731", {"start": v(19.04, 7.25) * mm, "end": v(20.04, 7.25) * mm});
            skLineSegment(sketch, "E1732", {"start": v(20.04, 7.25) * mm, "end": v(20.04, 6.25) * mm});
            skLineSegment(sketch, "E1733", {"start": v(20.04, 6.25) * mm, "end": v(19.04, 6.25) * mm});
            skLineSegment(sketch, "E1734", {"start": v(19.04, 6.25) * mm, "end": v(19.04, 7.25) * mm});
            skLineSegment(sketch, "E1735", {"start": v(20.24, 7.7) * mm, "end": v(20.24, 9) * mm});
            skLineSegment(sketch, "E1736", {"start": v(20.24, 9) * mm, "end": v(18.84, 9) * mm});
            skLineSegment(sketch, "E1737", {"start": v(18.84, 9) * mm, "end": v(18.84, 7.7) * mm});
            skArc(sketch, "E1738", {"start": v(18.84, 7.7) * mm, "mid": v(19.04, 7.5) * mm, "end": v(18.84, 7.3) * mm});
            skArc(sketch, "E1739", {"start": v(19.64, 7.5) * mm, "mid": v(19.54, 7.6) * mm, "end": v(19.44, 7.5) * mm});
            skArc(sketch, "E1740", {"start": v(19.44, 7.5) * mm, "mid": v(19.54, 7.4) * mm, "end": v(19.64, 7.5) * mm});
            skArc(sketch, "E1741", {"start": v(20.24, 7.7) * mm, "mid": v(20.04, 7.5) * mm, "end": v(20.24, 7.3) * mm});
            skLineSegment(sketch, "E1742", {"start": v(18.84, 7.3) * mm, "end": v(18.84, 6) * mm});
            skLineSegment(sketch, "E1743", {"start": v(18.84, 6) * mm, "end": v(20.24, 6) * mm});
            skLineSegment(sketch, "E1744", {"start": v(20.24, 6) * mm, "end": v(20.24, 7.3) * mm});
            skLineSegment(sketch, "E1745", {"start": v(20.54, 8.75) * mm, "end": v(21.54, 8.75) * mm});
            skLineSegment(sketch, "E1746", {"start": v(21.54, 8.75) * mm, "end": v(21.54, 7.75) * mm});
            skLineSegment(sketch, "E1747", {"start": v(21.54, 7.75) * mm, "end": v(20.54, 7.75) * mm});
            skLineSegment(sketch, "E1748", {"start": v(20.54, 7.75) * mm, "end": v(20.54, 8.75) * mm});
            skLineSegment(sketch, "E1749", {"start": v(20.54, 7.25) * mm, "end": v(21.54, 7.25) * mm});
            skLineSegment(sketch, "E1750", {"start": v(21.54, 7.25) * mm, "end": v(21.54, 6.25) * mm});
            skLineSegment(sketch, "E1751", {"start": v(21.54, 6.25) * mm, "end": v(20.54, 6.25) * mm});
            skLineSegment(sketch, "E1752", {"start": v(20.54, 6.25) * mm, "end": v(20.54, 7.25) * mm});
            skLineSegment(sketch, "E1753", {"start": v(21.74, 7.7) * mm, "end": v(21.74, 9) * mm});
            skLineSegment(sketch, "E1754", {"start": v(21.74, 9) * mm, "end": v(20.34, 9) * mm});
            skLineSegment(sketch, "E1755", {"start": v(20.34, 9) * mm, "end": v(20.34, 7.7) * mm});
            skArc(sketch, "E1756", {"start": v(20.34, 7.7) * mm, "mid": v(20.54, 7.5) * mm, "end": v(20.34, 7.3) * mm});
            skArc(sketch, "E1757", {"start": v(21.14, 7.5) * mm, "mid": v(21.04, 7.6) * mm, "end": v(20.94, 7.5) * mm});
            skArc(sketch, "E1758", {"start": v(20.94, 7.5) * mm, "mid": v(21.04, 7.4) * mm, "end": v(21.14, 7.5) * mm});
            skArc(sketch, "E1759", {"start": v(21.74, 7.7) * mm, "mid": v(21.54, 7.5) * mm, "end": v(21.74, 7.3) * mm});
            skLineSegment(sketch, "E1760", {"start": v(20.34, 7.3) * mm, "end": v(20.34, 6) * mm});
            skLineSegment(sketch, "E1761", {"start": v(20.34, 6) * mm, "end": v(21.74, 6) * mm});
            skLineSegment(sketch, "E1762", {"start": v(21.74, 6) * mm, "end": v(21.74, 7.3) * mm});
            skLineSegment(sketch, "E1763", {"start": v(18.79, 21) * mm, "end": v(18.79, 22) * mm});
            skLineSegment(sketch, "E1764", {"start": v(18.79, 22) * mm, "end": v(19.79, 22) * mm});
            skLineSegment(sketch, "E1765", {"start": v(19.79, 22) * mm, "end": v(19.79, 21) * mm});
            skLineSegment(sketch, "E1766", {"start": v(19.79, 21) * mm, "end": v(18.79, 21) * mm});
            skLineSegment(sketch, "E1767", {"start": v(20.29, 21) * mm, "end": v(20.29, 22) * mm});
            skLineSegment(sketch, "E1768", {"start": v(20.29, 22) * mm, "end": v(21.29, 22) * mm});
            skLineSegment(sketch, "E1769", {"start": v(21.29, 22) * mm, "end": v(21.29, 21) * mm});
            skLineSegment(sketch, "E1770", {"start": v(21.29, 21) * mm, "end": v(20.29, 21) * mm});
            skLineSegment(sketch, "E1771", {"start": v(19.84, 22.2) * mm, "end": v(18.54, 22.2) * mm});
            skLineSegment(sketch, "E1772", {"start": v(18.54, 22.2) * mm, "end": v(18.54, 20.8) * mm});
            skLineSegment(sketch, "E1773", {"start": v(18.54, 20.8) * mm, "end": v(19.84, 20.8) * mm});
            skArc(sketch, "E1774", {"start": v(19.84, 20.8) * mm, "mid": v(20.04, 21) * mm, "end": v(20.24, 20.8) * mm});
            skArc(sketch, "E1775", {"start": v(20.14, 21.5) * mm, "mid": v(20.04, 21.6) * mm, "end": v(19.94, 21.5) * mm});
            skArc(sketch, "E1776", {"start": v(19.94, 21.5) * mm, "mid": v(20.04, 21.4) * mm, "end": v(20.14, 21.5) * mm});
            skArc(sketch, "E1777", {"start": v(19.84, 22.2) * mm, "mid": v(20.04, 22) * mm, "end": v(20.24, 22.2) * mm});
            skLineSegment(sketch, "E1778", {"start": v(20.24, 20.8) * mm, "end": v(21.54, 20.8) * mm});
            skLineSegment(sketch, "E1779", {"start": v(21.54, 20.8) * mm, "end": v(21.54, 22.2) * mm});
            skLineSegment(sketch, "E1780", {"start": v(21.54, 22.2) * mm, "end": v(20.24, 22.2) * mm});
            skLineSegment(sketch, "E1781", {"start": v(-10.96, 31.75) * mm, "end": v(-9.96, 31.75) * mm});
            skLineSegment(sketch, "E1782", {"start": v(-9.96, 31.75) * mm, "end": v(-9.96, 30.75) * mm});
            skLineSegment(sketch, "E1783", {"start": v(-9.96, 30.75) * mm, "end": v(-10.96, 30.75) * mm});
            skLineSegment(sketch, "E1784", {"start": v(-10.96, 30.75) * mm, "end": v(-10.96, 31.75) * mm});
            skLineSegment(sketch, "E1785", {"start": v(-10.96, 30.25) * mm, "end": v(-9.96, 30.25) * mm});
            skLineSegment(sketch, "E1786", {"start": v(-9.96, 30.25) * mm, "end": v(-9.96, 29.25) * mm});
            skLineSegment(sketch, "E1787", {"start": v(-9.96, 29.25) * mm, "end": v(-10.96, 29.25) * mm});
            skLineSegment(sketch, "E1788", {"start": v(-10.96, 29.25) * mm, "end": v(-10.96, 30.25) * mm});
            skLineSegment(sketch, "E1789", {"start": v(-9.76, 30.7) * mm, "end": v(-9.76, 32) * mm});
            skLineSegment(sketch, "E1790", {"start": v(-9.76, 32) * mm, "end": v(-11.16, 32) * mm});
            skLineSegment(sketch, "E1791", {"start": v(-11.16, 32) * mm, "end": v(-11.16, 30.7) * mm});
            skArc(sketch, "E1792", {"start": v(-11.16, 30.7) * mm, "mid": v(-10.96, 30.5) * mm, "end": v(-11.16, 30.3) * mm});
            skArc(sketch, "E1793", {"start": v(-10.36, 30.5) * mm, "mid": v(-10.46, 30.6) * mm, "end": v(-10.56, 30.5) * mm});
            skArc(sketch, "E1794", {"start": v(-10.56, 30.5) * mm, "mid": v(-10.46, 30.4) * mm, "end": v(-10.36, 30.5) * mm});
            skArc(sketch, "E1795", {"start": v(-9.76, 30.7) * mm, "mid": v(-9.96, 30.5) * mm, "end": v(-9.76, 30.3) * mm});
            skLineSegment(sketch, "E1796", {"start": v(-11.16, 30.3) * mm, "end": v(-11.16, 29) * mm});
            skLineSegment(sketch, "E1797", {"start": v(-11.16, 29) * mm, "end": v(-9.76, 29) * mm});
            skLineSegment(sketch, "E1798", {"start": v(-9.76, 29) * mm, "end": v(-9.76, 30.3) * mm});
            skLineSegment(sketch, "E1799", {"start": v(28.79, 12) * mm, "end": v(29.79, 12) * mm});
            skLineSegment(sketch, "E1800", {"start": v(29.79, 12) * mm, "end": v(29.79, 11) * mm});
            skLineSegment(sketch, "E1801", {"start": v(29.79, 11) * mm, "end": v(28.79, 11) * mm});
            skLineSegment(sketch, "E1802", {"start": v(28.79, 11) * mm, "end": v(28.79, 12) * mm});
            skLineSegment(sketch, "E1803", {"start": v(28.79, 10.5) * mm, "end": v(29.79, 10.5) * mm});
            skLineSegment(sketch, "E1804", {"start": v(29.79, 10.5) * mm, "end": v(29.79, 9.5) * mm});
            skLineSegment(sketch, "E1805", {"start": v(29.79, 9.5) * mm, "end": v(28.79, 9.5) * mm});
            skLineSegment(sketch, "E1806", {"start": v(28.79, 9.5) * mm, "end": v(28.79, 10.5) * mm});
            skLineSegment(sketch, "E1807", {"start": v(29.99, 10.95) * mm, "end": v(29.99, 12.25) * mm});
            skLineSegment(sketch, "E1808", {"start": v(29.99, 12.25) * mm, "end": v(28.59, 12.25) * mm});
            skLineSegment(sketch, "E1809", {"start": v(28.59, 12.25) * mm, "end": v(28.59, 10.95) * mm});
            skArc(sketch, "E1810", {"start": v(28.59, 10.95) * mm, "mid": v(28.79, 10.75) * mm, "end": v(28.59, 10.55) * mm});
            skArc(sketch, "E1811", {"start": v(29.39, 10.75) * mm, "mid": v(29.29, 10.85) * mm, "end": v(29.19, 10.75) * mm});
            skArc(sketch, "E1812", {"start": v(29.19, 10.75) * mm, "mid": v(29.29, 10.65) * mm, "end": v(29.39, 10.75) * mm});
            skArc(sketch, "E1813", {"start": v(29.99, 10.95) * mm, "mid": v(29.79, 10.75) * mm, "end": v(29.99, 10.55) * mm});
            skLineSegment(sketch, "E1814", {"start": v(28.59, 10.55) * mm, "end": v(28.59, 9.25) * mm});
            skLineSegment(sketch, "E1815", {"start": v(28.59, 9.25) * mm, "end": v(29.99, 9.25) * mm});
            skLineSegment(sketch, "E1816", {"start": v(29.99, 9.25) * mm, "end": v(29.99, 10.55) * mm});
            skLineSegment(sketch, "E1817", {"start": v(23.54, 12) * mm, "end": v(24.54, 12) * mm});
            skLineSegment(sketch, "E1818", {"start": v(24.54, 12) * mm, "end": v(24.54, 11) * mm});
            skLineSegment(sketch, "E1819", {"start": v(24.54, 11) * mm, "end": v(23.54, 11) * mm});
            skLineSegment(sketch, "E1820", {"start": v(23.54, 11) * mm, "end": v(23.54, 12) * mm});
            skLineSegment(sketch, "E1821", {"start": v(23.54, 10.5) * mm, "end": v(24.54, 10.5) * mm});
            skLineSegment(sketch, "E1822", {"start": v(24.54, 10.5) * mm, "end": v(24.54, 9.5) * mm});
            skLineSegment(sketch, "E1823", {"start": v(24.54, 9.5) * mm, "end": v(23.54, 9.5) * mm});
            skLineSegment(sketch, "E1824", {"start": v(23.54, 9.5) * mm, "end": v(23.54, 10.5) * mm});
            skLineSegment(sketch, "E1825", {"start": v(24.74, 10.95) * mm, "end": v(24.74, 12.25) * mm});
            skLineSegment(sketch, "E1826", {"start": v(24.74, 12.25) * mm, "end": v(23.34, 12.25) * mm});
            skLineSegment(sketch, "E1827", {"start": v(23.34, 12.25) * mm, "end": v(23.34, 10.95) * mm});
            skArc(sketch, "E1828", {"start": v(23.34, 10.95) * mm, "mid": v(23.54, 10.75) * mm, "end": v(23.34, 10.55) * mm});
            skArc(sketch, "E1829", {"start": v(24.14, 10.75) * mm, "mid": v(24.04, 10.85) * mm, "end": v(23.94, 10.75) * mm});
            skArc(sketch, "E1830", {"start": v(23.94, 10.75) * mm, "mid": v(24.04, 10.65) * mm, "end": v(24.14, 10.75) * mm});
            skArc(sketch, "E1831", {"start": v(24.74, 10.95) * mm, "mid": v(24.54, 10.75) * mm, "end": v(24.74, 10.55) * mm});
            skLineSegment(sketch, "E1832", {"start": v(23.34, 10.55) * mm, "end": v(23.34, 9.25) * mm});
            skLineSegment(sketch, "E1833", {"start": v(23.34, 9.25) * mm, "end": v(24.74, 9.25) * mm});
            skLineSegment(sketch, "E1834", {"start": v(24.74, 9.25) * mm, "end": v(24.74, 10.55) * mm});
            skLineSegment(sketch, "E1835", {"start": v(25.29, 12) * mm, "end": v(26.29, 12) * mm});
            skLineSegment(sketch, "E1836", {"start": v(26.29, 12) * mm, "end": v(26.29, 11) * mm});
            skLineSegment(sketch, "E1837", {"start": v(26.29, 11) * mm, "end": v(25.29, 11) * mm});
            skLineSegment(sketch, "E1838", {"start": v(25.29, 11) * mm, "end": v(25.29, 12) * mm});
            skLineSegment(sketch, "E1839", {"start": v(25.29, 10.5) * mm, "end": v(26.29, 10.5) * mm});
            skLineSegment(sketch, "E1840", {"start": v(26.29, 10.5) * mm, "end": v(26.29, 9.5) * mm});
            skLineSegment(sketch, "E1841", {"start": v(26.29, 9.5) * mm, "end": v(25.29, 9.5) * mm});
            skLineSegment(sketch, "E1842", {"start": v(25.29, 9.5) * mm, "end": v(25.29, 10.5) * mm});
            skLineSegment(sketch, "E1843", {"start": v(26.49, 10.95) * mm, "end": v(26.49, 12.25) * mm});
            skLineSegment(sketch, "E1844", {"start": v(26.49, 12.25) * mm, "end": v(25.09, 12.25) * mm});
            skLineSegment(sketch, "E1845", {"start": v(25.09, 12.25) * mm, "end": v(25.09, 10.95) * mm});
            skArc(sketch, "E1846", {"start": v(25.09, 10.95) * mm, "mid": v(25.29, 10.75) * mm, "end": v(25.09, 10.55) * mm});
            skArc(sketch, "E1847", {"start": v(25.89, 10.75) * mm, "mid": v(25.79, 10.85) * mm, "end": v(25.69, 10.75) * mm});
            skArc(sketch, "E1848", {"start": v(25.69, 10.75) * mm, "mid": v(25.79, 10.65) * mm, "end": v(25.89, 10.75) * mm});
            skArc(sketch, "E1849", {"start": v(26.49, 10.95) * mm, "mid": v(26.29, 10.75) * mm, "end": v(26.49, 10.55) * mm});
            skLineSegment(sketch, "E1850", {"start": v(25.09, 10.55) * mm, "end": v(25.09, 9.25) * mm});
            skLineSegment(sketch, "E1851", {"start": v(25.09, 9.25) * mm, "end": v(26.49, 9.25) * mm});
            skLineSegment(sketch, "E1852", {"start": v(26.49, 9.25) * mm, "end": v(26.49, 10.55) * mm});
            skLineSegment(sketch, "E1853", {"start": v(27.04, 12) * mm, "end": v(28.04, 12) * mm});
            skLineSegment(sketch, "E1854", {"start": v(28.04, 12) * mm, "end": v(28.04, 11) * mm});
            skLineSegment(sketch, "E1855", {"start": v(28.04, 11) * mm, "end": v(27.04, 11) * mm});
            skLineSegment(sketch, "E1856", {"start": v(27.04, 11) * mm, "end": v(27.04, 12) * mm});
            skLineSegment(sketch, "E1857", {"start": v(27.04, 10.5) * mm, "end": v(28.04, 10.5) * mm});
            skLineSegment(sketch, "E1858", {"start": v(28.04, 10.5) * mm, "end": v(28.04, 9.5) * mm});
            skLineSegment(sketch, "E1859", {"start": v(28.04, 9.5) * mm, "end": v(27.04, 9.5) * mm});
            skLineSegment(sketch, "E1860", {"start": v(27.04, 9.5) * mm, "end": v(27.04, 10.5) * mm});
            skLineSegment(sketch, "E1861", {"start": v(28.24, 10.95) * mm, "end": v(28.24, 12.25) * mm});
            skLineSegment(sketch, "E1862", {"start": v(28.24, 12.25) * mm, "end": v(26.84, 12.25) * mm});
            skLineSegment(sketch, "E1863", {"start": v(26.84, 12.25) * mm, "end": v(26.84, 10.95) * mm});
            skArc(sketch, "E1864", {"start": v(26.84, 10.95) * mm, "mid": v(27.04, 10.75) * mm, "end": v(26.84, 10.55) * mm});
            skArc(sketch, "E1865", {"start": v(27.64, 10.75) * mm, "mid": v(27.54, 10.85) * mm, "end": v(27.44, 10.75) * mm});
            skArc(sketch, "E1866", {"start": v(27.44, 10.75) * mm, "mid": v(27.54, 10.65) * mm, "end": v(27.64, 10.75) * mm});
            skArc(sketch, "E1867", {"start": v(28.24, 10.95) * mm, "mid": v(28.04, 10.75) * mm, "end": v(28.24, 10.55) * mm});
            skLineSegment(sketch, "E1868", {"start": v(26.84, 10.55) * mm, "end": v(26.84, 9.25) * mm});
            skLineSegment(sketch, "E1869", {"start": v(26.84, 9.25) * mm, "end": v(28.24, 9.25) * mm});
            skLineSegment(sketch, "E1870", {"start": v(28.24, 9.25) * mm, "end": v(28.24, 10.55) * mm});
            skLineSegment(sketch, "E1871", {"start": v(11.29, -1) * mm, "end": v(11.29, -2) * mm});
            skLineSegment(sketch, "E1872", {"start": v(11.29, -2) * mm, "end": v(10.29, -2) * mm});
            skLineSegment(sketch, "E1873", {"start": v(10.29, -2) * mm, "end": v(10.29, -1) * mm});
            skLineSegment(sketch, "E1874", {"start": v(10.29, -1) * mm, "end": v(11.29, -1) * mm});
            skLineSegment(sketch, "E1875", {"start": v(9.79, -1) * mm, "end": v(9.79, -2) * mm});
            skLineSegment(sketch, "E1876", {"start": v(9.79, -2) * mm, "end": v(8.79, -2) * mm});
            skLineSegment(sketch, "E1877", {"start": v(8.79, -2) * mm, "end": v(8.79, -1) * mm});
            skLineSegment(sketch, "E1878", {"start": v(8.79, -1) * mm, "end": v(9.79, -1) * mm});
            skLineSegment(sketch, "E1879", {"start": v(10.24, -2.2) * mm, "end": v(11.54, -2.2) * mm});
            skLineSegment(sketch, "E1880", {"start": v(11.54, -2.2) * mm, "end": v(11.54, -0.8) * mm});
            skLineSegment(sketch, "E1881", {"start": v(11.54, -0.8) * mm, "end": v(10.24, -0.8) * mm});
            skArc(sketch, "E1882", {"start": v(10.24, -0.8) * mm, "mid": v(10.04, -1) * mm, "end": v(9.84, -0.8) * mm});
            skArc(sketch, "E1883", {"start": v(10.14, -1.5) * mm, "mid": v(10.04, -1.4) * mm, "end": v(9.94, -1.5) * mm});
            skArc(sketch, "E1884", {"start": v(9.94, -1.5) * mm, "mid": v(10.04, -1.6) * mm, "end": v(10.14, -1.5) * mm});
            skArc(sketch, "E1885", {"start": v(10.24, -2.2) * mm, "mid": v(10.04, -2) * mm, "end": v(9.84, -2.2) * mm});
            skLineSegment(sketch, "E1886", {"start": v(9.84, -0.8) * mm, "end": v(8.54, -0.8) * mm});
            skLineSegment(sketch, "E1887", {"start": v(8.54, -0.8) * mm, "end": v(8.54, -2.2) * mm});
            skLineSegment(sketch, "E1888", {"start": v(8.54, -2.2) * mm, "end": v(9.84, -2.2) * mm});
            skLineSegment(sketch, "E1889", {"start": v(-1.96, -10.75) * mm, "end": v(-2.96, -10.75) * mm});
            skLineSegment(sketch, "E1890", {"start": v(-2.96, -10.75) * mm, "end": v(-2.96, -9.75) * mm});
            skLineSegment(sketch, "E1891", {"start": v(-2.96, -9.75) * mm, "end": v(-1.96, -9.75) * mm});
            skLineSegment(sketch, "E1892", {"start": v(-1.96, -9.75) * mm, "end": v(-1.96, -10.75) * mm});
            skLineSegment(sketch, "E1893", {"start": v(-1.96, -9.25) * mm, "end": v(-2.96, -9.25) * mm});
            skLineSegment(sketch, "E1894", {"start": v(-2.96, -9.25) * mm, "end": v(-2.96, -8.25) * mm});
            skLineSegment(sketch, "E1895", {"start": v(-2.96, -8.25) * mm, "end": v(-1.96, -8.25) * mm});
            skLineSegment(sketch, "E1896", {"start": v(-1.96, -8.25) * mm, "end": v(-1.96, -9.25) * mm});
            skLineSegment(sketch, "E1897", {"start": v(-3.16, -9.7) * mm, "end": v(-3.16, -11) * mm});
            skLineSegment(sketch, "E1898", {"start": v(-3.16, -11) * mm, "end": v(-1.76, -11) * mm});
            skLineSegment(sketch, "E1899", {"start": v(-1.76, -11) * mm, "end": v(-1.76, -9.7) * mm});
            skArc(sketch, "E1900", {"start": v(-1.76, -9.7) * mm, "mid": v(-1.96, -9.5) * mm, "end": v(-1.76, -9.3) * mm});
            skArc(sketch, "E1901", {"start": v(-2.36, -9.5) * mm, "mid": v(-2.46, -9.4) * mm, "end": v(-2.56, -9.5) * mm});
            skArc(sketch, "E1902", {"start": v(-2.56, -9.5) * mm, "mid": v(-2.46, -9.6) * mm, "end": v(-2.36, -9.5) * mm});
            skArc(sketch, "E1903", {"start": v(-3.16, -9.7) * mm, "mid": v(-2.96, -9.5) * mm, "end": v(-3.16, -9.3) * mm});
            skLineSegment(sketch, "E1904", {"start": v(-1.76, -9.3) * mm, "end": v(-1.76, -8) * mm});
            skLineSegment(sketch, "E1905", {"start": v(-1.76, -8) * mm, "end": v(-3.16, -8) * mm});
            skLineSegment(sketch, "E1906", {"start": v(-3.16, -8) * mm, "end": v(-3.16, -9.3) * mm});
            skLineSegment(sketch, "E1907", {"start": v(-15.71, -10) * mm, "end": v(-15.71, -9) * mm});
            skLineSegment(sketch, "E1908", {"start": v(-15.71, -9) * mm, "end": v(-14.71, -9) * mm});
            skLineSegment(sketch, "E1909", {"start": v(-14.71, -9) * mm, "end": v(-14.71, -10) * mm});
            skLineSegment(sketch, "E1910", {"start": v(-14.71, -10) * mm, "end": v(-15.71, -10) * mm});
            skLineSegment(sketch, "E1911", {"start": v(-14.21, -10) * mm, "end": v(-14.21, -9) * mm});
            skLineSegment(sketch, "E1912", {"start": v(-14.21, -9) * mm, "end": v(-13.21, -9) * mm});
            skLineSegment(sketch, "E1913", {"start": v(-13.21, -9) * mm, "end": v(-13.21, -10) * mm});
            skLineSegment(sketch, "E1914", {"start": v(-13.21, -10) * mm, "end": v(-14.21, -10) * mm});
            skLineSegment(sketch, "E1915", {"start": v(-14.66, -8.8) * mm, "end": v(-15.96, -8.8) * mm});
            skLineSegment(sketch, "E1916", {"start": v(-15.96, -8.8) * mm, "end": v(-15.96, -10.2) * mm});
            skLineSegment(sketch, "E1917", {"start": v(-15.96, -10.2) * mm, "end": v(-14.66, -10.2) * mm});
            skArc(sketch, "E1918", {"start": v(-14.66, -10.2) * mm, "mid": v(-14.46, -10) * mm, "end": v(-14.26, -10.2) * mm});
            skArc(sketch, "E1919", {"start": v(-14.36, -9.5) * mm, "mid": v(-14.46, -9.4) * mm, "end": v(-14.56, -9.5) * mm});
            skArc(sketch, "E1920", {"start": v(-14.56, -9.5) * mm, "mid": v(-14.46, -9.6) * mm, "end": v(-14.36, -9.5) * mm});
            skArc(sketch, "E1921", {"start": v(-14.66, -8.8) * mm, "mid": v(-14.46, -9) * mm, "end": v(-14.26, -8.8) * mm});
            skLineSegment(sketch, "E1922", {"start": v(-14.26, -10.2) * mm, "end": v(-12.96, -10.2) * mm});
            skLineSegment(sketch, "E1923", {"start": v(-12.96, -10.2) * mm, "end": v(-12.96, -8.8) * mm});
            skLineSegment(sketch, "E1924", {"start": v(-12.96, -8.8) * mm, "end": v(-14.26, -8.8) * mm});
            skLineSegment(sketch, "E1925", {"start": v(13.79, -27.5) * mm, "end": v(13.79, -28.5) * mm});
            skLineSegment(sketch, "E1926", {"start": v(13.79, -28.5) * mm, "end": v(12.79, -28.5) * mm});
            skLineSegment(sketch, "E1927", {"start": v(12.79, -28.5) * mm, "end": v(12.79, -27.5) * mm});
            skLineSegment(sketch, "E1928", {"start": v(12.79, -27.5) * mm, "end": v(13.79, -27.5) * mm});
            skLineSegment(sketch, "E1929", {"start": v(12.29, -27.5) * mm, "end": v(12.29, -28.5) * mm});
            skLineSegment(sketch, "E1930", {"start": v(12.29, -28.5) * mm, "end": v(11.29, -28.5) * mm});
            skLineSegment(sketch, "E1931", {"start": v(11.29, -28.5) * mm, "end": v(11.29, -27.5) * mm});
            skLineSegment(sketch, "E1932", {"start": v(11.29, -27.5) * mm, "end": v(12.29, -27.5) * mm});
            skLineSegment(sketch, "E1933", {"start": v(12.74, -28.7) * mm, "end": v(14.04, -28.7) * mm});
            skLineSegment(sketch, "E1934", {"start": v(14.04, -28.7) * mm, "end": v(14.04, -27.3) * mm});
            skLineSegment(sketch, "E1935", {"start": v(14.04, -27.3) * mm, "end": v(12.74, -27.3) * mm});
            skArc(sketch, "E1936", {"start": v(12.74, -27.3) * mm, "mid": v(12.54, -27.5) * mm, "end": v(12.34, -27.3) * mm});
            skArc(sketch, "E1937", {"start": v(12.64, -28) * mm, "mid": v(12.54, -27.9) * mm, "end": v(12.44, -28) * mm});
            skArc(sketch, "E1938", {"start": v(12.44, -28) * mm, "mid": v(12.54, -28.1) * mm, "end": v(12.64, -28) * mm});
            skArc(sketch, "E1939", {"start": v(12.74, -28.7) * mm, "mid": v(12.54, -28.5) * mm, "end": v(12.34, -28.7) * mm});
            skLineSegment(sketch, "E1940", {"start": v(12.34, -27.3) * mm, "end": v(11.04, -27.3) * mm});
            skLineSegment(sketch, "E1941", {"start": v(11.04, -27.3) * mm, "end": v(11.04, -28.7) * mm});
            skLineSegment(sketch, "E1942", {"start": v(11.04, -28.7) * mm, "end": v(12.34, -28.7) * mm});
            skLineSegment(sketch, "E1943", {"start": v(13.79, -26) * mm, "end": v(13.79, -27) * mm});
            skLineSegment(sketch, "E1944", {"start": v(13.79, -27) * mm, "end": v(12.79, -27) * mm});
            skLineSegment(sketch, "E1945", {"start": v(12.79, -27) * mm, "end": v(12.79, -26) * mm});
            skLineSegment(sketch, "E1946", {"start": v(12.79, -26) * mm, "end": v(13.79, -26) * mm});
            skLineSegment(sketch, "E1947", {"start": v(12.29, -26) * mm, "end": v(12.29, -27) * mm});
            skLineSegment(sketch, "E1948", {"start": v(12.29, -27) * mm, "end": v(11.29, -27) * mm});
            skLineSegment(sketch, "E1949", {"start": v(11.29, -27) * mm, "end": v(11.29, -26) * mm});
            skLineSegment(sketch, "E1950", {"start": v(11.29, -26) * mm, "end": v(12.29, -26) * mm});
            skLineSegment(sketch, "E1951", {"start": v(12.74, -27.2) * mm, "end": v(14.04, -27.2) * mm});
            skLineSegment(sketch, "E1952", {"start": v(14.04, -27.2) * mm, "end": v(14.04, -25.8) * mm});
            skLineSegment(sketch, "E1953", {"start": v(14.04, -25.8) * mm, "end": v(12.74, -25.8) * mm});
            skArc(sketch, "E1954", {"start": v(12.74, -25.8) * mm, "mid": v(12.54, -26) * mm, "end": v(12.34, -25.8) * mm});
            skArc(sketch, "E1955", {"start": v(12.64, -26.5) * mm, "mid": v(12.54, -26.4) * mm, "end": v(12.44, -26.5) * mm});
            skArc(sketch, "E1956", {"start": v(12.44, -26.5) * mm, "mid": v(12.54, -26.6) * mm, "end": v(12.64, -26.5) * mm});
            skArc(sketch, "E1957", {"start": v(12.74, -27.2) * mm, "mid": v(12.54, -27) * mm, "end": v(12.34, -27.2) * mm});
            skLineSegment(sketch, "E1958", {"start": v(12.34, -25.8) * mm, "end": v(11.04, -25.8) * mm});
            skLineSegment(sketch, "E1959", {"start": v(11.04, -25.8) * mm, "end": v(11.04, -27.2) * mm});
            skLineSegment(sketch, "E1960", {"start": v(11.04, -27.2) * mm, "end": v(12.34, -27.2) * mm});
            skLineSegment(sketch, "E1961", {"start": v(13.79, -24.5) * mm, "end": v(13.79, -25.5) * mm});
            skLineSegment(sketch, "E1962", {"start": v(13.79, -25.5) * mm, "end": v(12.79, -25.5) * mm});
            skLineSegment(sketch, "E1963", {"start": v(12.79, -25.5) * mm, "end": v(12.79, -24.5) * mm});
            skLineSegment(sketch, "E1964", {"start": v(12.79, -24.5) * mm, "end": v(13.79, -24.5) * mm});
            skLineSegment(sketch, "E1965", {"start": v(12.29, -24.5) * mm, "end": v(12.29, -25.5) * mm});
            skLineSegment(sketch, "E1966", {"start": v(12.29, -25.5) * mm, "end": v(11.29, -25.5) * mm});
            skLineSegment(sketch, "E1967", {"start": v(11.29, -25.5) * mm, "end": v(11.29, -24.5) * mm});
            skLineSegment(sketch, "E1968", {"start": v(11.29, -24.5) * mm, "end": v(12.29, -24.5) * mm});
            skLineSegment(sketch, "E1969", {"start": v(12.74, -25.7) * mm, "end": v(14.04, -25.7) * mm});
            skLineSegment(sketch, "E1970", {"start": v(14.04, -25.7) * mm, "end": v(14.04, -24.3) * mm});
            skLineSegment(sketch, "E1971", {"start": v(14.04, -24.3) * mm, "end": v(12.74, -24.3) * mm});
            skArc(sketch, "E1972", {"start": v(12.74, -24.3) * mm, "mid": v(12.54, -24.5) * mm, "end": v(12.34, -24.3) * mm});
            skArc(sketch, "E1973", {"start": v(12.64, -25) * mm, "mid": v(12.54, -24.9) * mm, "end": v(12.44, -25) * mm});
            skArc(sketch, "E1974", {"start": v(12.44, -25) * mm, "mid": v(12.54, -25.1) * mm, "end": v(12.64, -25) * mm});
            skArc(sketch, "E1975", {"start": v(12.74, -25.7) * mm, "mid": v(12.54, -25.5) * mm, "end": v(12.34, -25.7) * mm});
            skLineSegment(sketch, "E1976", {"start": v(12.34, -24.3) * mm, "end": v(11.04, -24.3) * mm});
            skLineSegment(sketch, "E1977", {"start": v(11.04, -24.3) * mm, "end": v(11.04, -25.7) * mm});
            skLineSegment(sketch, "E1978", {"start": v(11.04, -25.7) * mm, "end": v(12.34, -25.7) * mm});
            skLineSegment(sketch, "E1979", {"start": v(13.79, -23) * mm, "end": v(13.79, -24) * mm});
            skLineSegment(sketch, "E1980", {"start": v(13.79, -24) * mm, "end": v(12.79, -24) * mm});
            skLineSegment(sketch, "E1981", {"start": v(12.79, -24) * mm, "end": v(12.79, -23) * mm});
            skLineSegment(sketch, "E1982", {"start": v(12.79, -23) * mm, "end": v(13.79, -23) * mm});
            skLineSegment(sketch, "E1983", {"start": v(12.29, -23) * mm, "end": v(12.29, -24) * mm});
            skLineSegment(sketch, "E1984", {"start": v(12.29, -24) * mm, "end": v(11.29, -24) * mm});
            skLineSegment(sketch, "E1985", {"start": v(11.29, -24) * mm, "end": v(11.29, -23) * mm});
            skLineSegment(sketch, "E1986", {"start": v(11.29, -23) * mm, "end": v(12.29, -23) * mm});
            skLineSegment(sketch, "E1987", {"start": v(12.74, -24.2) * mm, "end": v(14.04, -24.2) * mm});
            skLineSegment(sketch, "E1988", {"start": v(14.04, -24.2) * mm, "end": v(14.04, -22.8) * mm});
            skLineSegment(sketch, "E1989", {"start": v(14.04, -22.8) * mm, "end": v(12.74, -22.8) * mm});
            skArc(sketch, "E1990", {"start": v(12.74, -22.8) * mm, "mid": v(12.54, -23) * mm, "end": v(12.34, -22.8) * mm});
            skArc(sketch, "E1991", {"start": v(12.64, -23.5) * mm, "mid": v(12.54, -23.4) * mm, "end": v(12.44, -23.5) * mm});
            skArc(sketch, "E1992", {"start": v(12.44, -23.5) * mm, "mid": v(12.54, -23.6) * mm, "end": v(12.64, -23.5) * mm});
            skArc(sketch, "E1993", {"start": v(12.74, -24.2) * mm, "mid": v(12.54, -24) * mm, "end": v(12.34, -24.2) * mm});
            skLineSegment(sketch, "E1994", {"start": v(12.34, -22.8) * mm, "end": v(11.04, -22.8) * mm});
            skLineSegment(sketch, "E1995", {"start": v(11.04, -22.8) * mm, "end": v(11.04, -24.2) * mm});
            skLineSegment(sketch, "E1996", {"start": v(11.04, -24.2) * mm, "end": v(12.34, -24.2) * mm});
            skLineSegment(sketch, "E1997", {"start": v(11.29, 0.75) * mm, "end": v(11.29, -0.25) * mm});
            skLineSegment(sketch, "E1998", {"start": v(11.29, -0.25) * mm, "end": v(10.29, -0.25) * mm});
            skLineSegment(sketch, "E1999", {"start": v(10.29, -0.25) * mm, "end": v(10.29, 0.75) * mm});
            skLineSegment(sketch, "E2000", {"start": v(10.29, 0.75) * mm, "end": v(11.29, 0.75) * mm});
            skLineSegment(sketch, "E2001", {"start": v(9.79, 0.75) * mm, "end": v(9.79, -0.25) * mm});
            skLineSegment(sketch, "E2002", {"start": v(9.79, -0.25) * mm, "end": v(8.79, -0.25) * mm});
            skLineSegment(sketch, "E2003", {"start": v(8.79, -0.25) * mm, "end": v(8.79, 0.75) * mm});
            skLineSegment(sketch, "E2004", {"start": v(8.79, 0.75) * mm, "end": v(9.79, 0.75) * mm});
            skLineSegment(sketch, "E2005", {"start": v(10.24, -0.45) * mm, "end": v(11.54, -0.45) * mm});
            skLineSegment(sketch, "E2006", {"start": v(11.54, -0.45) * mm, "end": v(11.54, 0.95) * mm});
            skLineSegment(sketch, "E2007", {"start": v(11.54, 0.95) * mm, "end": v(10.24, 0.95) * mm});
            skArc(sketch, "E2008", {"start": v(10.24, 0.95) * mm, "mid": v(10.04, 0.75) * mm, "end": v(9.84, 0.95) * mm});
            skArc(sketch, "E2009", {"start": v(10.14, 0.25) * mm, "mid": v(10.04, 0.35) * mm, "end": v(9.94, 0.25) * mm});
            skArc(sketch, "E2010", {"start": v(9.94, 0.25) * mm, "mid": v(10.04, 0.15) * mm, "end": v(10.14, 0.25) * mm});
            skArc(sketch, "E2011", {"start": v(10.24, -0.45) * mm, "mid": v(10.04, -0.25) * mm, "end": v(9.84, -0.45) * mm});
            skLineSegment(sketch, "E2012", {"start": v(9.84, 0.95) * mm, "end": v(8.54, 0.95) * mm});
            skLineSegment(sketch, "E2013", {"start": v(8.54, 0.95) * mm, "end": v(8.54, -0.45) * mm});
            skLineSegment(sketch, "E2014", {"start": v(8.54, -0.45) * mm, "end": v(9.84, -0.45) * mm});
            skLineSegment(sketch, "E2015", {"start": v(49.79, 32.5) * mm, "end": v(49.54, 33.5) * mm});
            skLineSegment(sketch, "E2016", {"start": v(49.54, 33.5) * mm, "end": v(49.29, 32.5) * mm});
            skLineSegment(sketch, "E2017", {"start": v(49.29, 32.5) * mm, "end": v(49.79, 32.5) * mm});
            skLineSegment(sketch, "E2018", {"start": v(49.54, 6.1) * mm, "end": v(49.54, 33.5) * mm});
            skLineSegment(sketch, "E2019", {"start": v(49.29, -29.5) * mm, "end": v(49.54, -30.5) * mm});
            skLineSegment(sketch, "E2020", {"start": v(49.54, -30.5) * mm, "end": v(49.79, -29.5) * mm});
            skLineSegment(sketch, "E2021", {"start": v(49.79, -29.5) * mm, "end": v(49.29, -29.5) * mm});
            skLineSegment(sketch, "E2022", {"start": v(49.54, 0.9) * mm, "end": v(49.54, -30.5) * mm});
            skLineSegment(sketch, "E2023", {"start": v(35.04, -30.5) * mm, "end": v(50.04, -30.5) * mm});
            skLineSegment(sketch, "E2024", {"start": v(35.04, 33.5) * mm, "end": v(50.04, 33.5) * mm});
            skLineSegment(sketch, "E2025", {"start": v(38.29, 2.5) * mm, "end": v(38.04, 3.5) * mm});
            skLineSegment(sketch, "E2026", {"start": v(38.04, 3.5) * mm, "end": v(37.79, 2.5) * mm});
            skLineSegment(sketch, "E2027", {"start": v(37.79, 2.5) * mm, "end": v(38.29, 2.5) * mm});
            skLineSegment(sketch, "E2028", {"start": v(38.04, 3.3) * mm, "end": v(38.04, 3.5) * mm});
            skLineSegment(sketch, "E2029", {"start": v(37.79, 0.5) * mm, "end": v(38.04, -0.5) * mm});
            skLineSegment(sketch, "E2030", {"start": v(38.04, -0.5) * mm, "end": v(38.29, 0.5) * mm});
            skLineSegment(sketch, "E2031", {"start": v(38.29, 0.5) * mm, "end": v(37.79, 0.5) * mm});
            skLineSegment(sketch, "E2032", {"start": v(38.04, -0.3) * mm, "end": v(38.04, -0.5) * mm});
            skLineSegment(sketch, "E2033", {"start": v(7.58, -0.5) * mm, "end": v(38.54, -0.5) * mm});
            skLineSegment(sketch, "E2034", {"start": v(35.04, 3.5) * mm, "end": v(38.54, 3.5) * mm});
            skLineSegment(sketch, "E2035", {"start": v(43.79, 2.5) * mm, "end": v(43.54, 3.5) * mm});
            skLineSegment(sketch, "E2036", {"start": v(43.54, 3.5) * mm, "end": v(43.29, 2.5) * mm});
            skLineSegment(sketch, "E2037", {"start": v(43.29, 2.5) * mm, "end": v(43.79, 2.5) * mm});
            skLineSegment(sketch, "E2038", {"start": v(43.54, -3.9) * mm, "end": v(43.54, 3.5) * mm});
            skLineSegment(sketch, "E2039", {"start": v(43.29, -12.5) * mm, "end": v(43.54, -13.5) * mm});
            skLineSegment(sketch, "E2040", {"start": v(43.54, -13.5) * mm, "end": v(43.79, -12.5) * mm});
            skLineSegment(sketch, "E2041", {"start": v(43.79, -12.5) * mm, "end": v(43.29, -12.5) * mm});
            skLineSegment(sketch, "E2042", {"start": v(43.54, -9.1) * mm, "end": v(43.54, -13.5) * mm});
            skLineSegment(sketch, "E2043", {"start": v(25.6, -13.5) * mm, "end": v(44.04, -13.5) * mm});
            skLineSegment(sketch, "E2044", {"start": v(35.04, 3.5) * mm, "end": v(44.04, 3.5) * mm});
            skLineSegment(sketch, "E2045", {"start": v(43.79, -14.5) * mm, "end": v(43.54, -13.5) * mm});
            skLineSegment(sketch, "E2046", {"start": v(43.54, -13.5) * mm, "end": v(43.29, -14.5) * mm});
            skLineSegment(sketch, "E2047", {"start": v(43.29, -14.5) * mm, "end": v(43.79, -14.5) * mm});
            skLineSegment(sketch, "E2048", {"start": v(43.54, -19.9) * mm, "end": v(43.54, -13.5) * mm});
            skLineSegment(sketch, "E2049", {"start": v(43.29, -29.5) * mm, "end": v(43.54, -30.5) * mm});
            skLineSegment(sketch, "E2050", {"start": v(43.54, -30.5) * mm, "end": v(43.79, -29.5) * mm});
            skLineSegment(sketch, "E2051", {"start": v(43.79, -29.5) * mm, "end": v(43.29, -29.5) * mm});
            skLineSegment(sketch, "E2052", {"start": v(43.54, -25.1) * mm, "end": v(43.54, -30.5) * mm});
            skLineSegment(sketch, "E2053", {"start": v(35.04, -30.5) * mm, "end": v(44.04, -30.5) * mm});
            skLineSegment(sketch, "E2054", {"start": v(35.79, 5) * mm, "end": v(35.54, 6) * mm});
            skLineSegment(sketch, "E2055", {"start": v(35.54, 6) * mm, "end": v(35.29, 5) * mm});
            skLineSegment(sketch, "E2056", {"start": v(35.29, 5) * mm, "end": v(35.79, 5) * mm});
            skLineSegment(sketch, "E2057", {"start": v(35.54, 9.1) * mm, "end": v(35.54, 6) * mm});
            skLineSegment(sketch, "E2058", {"start": v(35.29, 4.5) * mm, "end": v(35.54, 3.5) * mm});
            skLineSegment(sketch, "E2059", {"start": v(35.54, 3.5) * mm, "end": v(35.79, 4.5) * mm});
            skLineSegment(sketch, "E2060", {"start": v(35.79, 4.5) * mm, "end": v(35.29, 4.5) * mm});
            skLineSegment(sketch, "E2061", {"start": v(35.54, 6) * mm, "end": v(35.54, 3.5) * mm});
            skLineSegment(sketch, "E2062", {"start": v(34.04, 3.5) * mm, "end": v(36.04, 3.5) * mm});
            skLineSegment(sketch, "E2063", {"start": v(16.04, 6) * mm, "end": v(36.04, 6) * mm});
            skLineSegment(sketch, "E2064", {"start": v(46.79, 2.5) * mm, "end": v(46.54, 3.5) * mm});
            skLineSegment(sketch, "E2065", {"start": v(46.54, 3.5) * mm, "end": v(46.29, 2.5) * mm});
            skLineSegment(sketch, "E2066", {"start": v(46.29, 2.5) * mm, "end": v(46.79, 2.5) * mm});
            skLineSegment(sketch, "E2067", {"start": v(46.54, -10.9) * mm, "end": v(46.54, 3.5) * mm});
            skLineSegment(sketch, "E2068", {"start": v(46.29, -29.5) * mm, "end": v(46.54, -30.5) * mm});
            skLineSegment(sketch, "E2069", {"start": v(46.54, -30.5) * mm, "end": v(46.79, -29.5) * mm});
            skLineSegment(sketch, "E2070", {"start": v(46.79, -29.5) * mm, "end": v(46.29, -29.5) * mm});
            skLineSegment(sketch, "E2071", {"start": v(46.54, -16.1) * mm, "end": v(46.54, -30.5) * mm});
            skLineSegment(sketch, "E2072", {"start": v(35.04, -30.5) * mm, "end": v(47.04, -30.5) * mm});
            skLineSegment(sketch, "E2073", {"start": v(35.04, 3.5) * mm, "end": v(47.04, 3.5) * mm});
            skLineSegment(sketch, "E2074", {"start": v(33.54, -35.75) * mm, "end": v(34.54, -35.5) * mm});
            skLineSegment(sketch, "E2075", {"start": v(34.54, -35.5) * mm, "end": v(33.54, -35.25) * mm});
            skLineSegment(sketch, "E2076", {"start": v(33.54, -35.25) * mm, "end": v(33.54, -35.75) * mm});
            skLineSegment(sketch, "E2077", {"start": v(7.14, -35.5) * mm, "end": v(34.54, -35.5) * mm});
            skLineSegment(sketch, "E2078", {"start": v(-24.46, -35.25) * mm, "end": v(-25.46, -35.5) * mm});
            skLineSegment(sketch, "E2079", {"start": v(-25.46, -35.5) * mm, "end": v(-24.46, -35.75) * mm});
            skLineSegment(sketch, "E2080", {"start": v(-24.46, -35.75) * mm, "end": v(-24.46, -35.25) * mm});
            skLineSegment(sketch, "E2081", {"start": v(1.94, -35.5) * mm, "end": v(-25.46, -35.5) * mm});
            skLineSegment(sketch, "E2082", {"start": v(34.54, -31) * mm, "end": v(34.54, -36) * mm});
            skLineSegment(sketch, "E2083", {"start": v(-25.46, -31) * mm, "end": v(-25.46, -36) * mm});
            skLineSegment(sketch, "E2084", {"start": v(33.54, -33.75) * mm, "end": v(34.54, -33.5) * mm});
            skLineSegment(sketch, "E2085", {"start": v(34.54, -33.5) * mm, "end": v(33.54, -33.25) * mm});
            skLineSegment(sketch, "E2086", {"start": v(33.54, -33.25) * mm, "end": v(33.54, -33.75) * mm});
            skLineSegment(sketch, "E2087", {"start": v(23.59, -33.5) * mm, "end": v(34.54, -33.5) * mm});
            skLineSegment(sketch, "E2088", {"start": v(5.54, -33.25) * mm, "end": v(4.54, -33.5) * mm});
            skLineSegment(sketch, "E2089", {"start": v(4.54, -33.5) * mm, "end": v(5.54, -33.75) * mm});
            skLineSegment(sketch, "E2090", {"start": v(5.54, -33.75) * mm, "end": v(5.54, -33.25) * mm});
            skLineSegment(sketch, "E2091", {"start": v(18.4, -33.5) * mm, "end": v(4.54, -33.5) * mm});
            skLineSegment(sketch, "E2092", {"start": v(34.54, -31) * mm, "end": v(34.54, -34) * mm});
            skLineSegment(sketch, "E2093", {"start": v(4.54, -1) * mm, "end": v(4.54, -34) * mm});
            skLineSegment(sketch, "E2094", {"start": v(3.54, -33.75) * mm, "end": v(4.54, -33.5) * mm});
            skLineSegment(sketch, "E2095", {"start": v(4.54, -33.5) * mm, "end": v(3.54, -33.25) * mm});
            skLineSegment(sketch, "E2096", {"start": v(3.54, -33.25) * mm, "end": v(3.54, -33.75) * mm});
            skLineSegment(sketch, "E2097", {"start": v(-7.38, -33.5) * mm, "end": v(4.54, -33.5) * mm});
            skLineSegment(sketch, "E2098", {"start": v(-24.46, -33.25) * mm, "end": v(-25.46, -33.5) * mm});
            skLineSegment(sketch, "E2099", {"start": v(-25.46, -33.5) * mm, "end": v(-24.46, -33.75) * mm});
            skLineSegment(sketch, "E2100", {"start": v(-24.46, -33.75) * mm, "end": v(-24.46, -33.25) * mm});
            skLineSegment(sketch, "E2101", {"start": v(-12.57, -33.5) * mm, "end": v(-25.46, -33.5) * mm});
            skLineSegment(sketch, "E2102", {"start": v(-25.46, -31) * mm, "end": v(-25.46, -34) * mm});
            skLineSegment(sketch, "E2103", {"start": v(39.79, -28) * mm, "end": v(39.54, -27) * mm});
            skLineSegment(sketch, "E2104", {"start": v(39.54, -27) * mm, "end": v(39.29, -28) * mm});
            skLineSegment(sketch, "E2105", {"start": v(39.29, -28) * mm, "end": v(39.79, -28) * mm});
            skLineSegment(sketch, "E2106", {"start": v(39.54, -20.9) * mm, "end": v(39.54, -27) * mm});
            skLineSegment(sketch, "E2107", {"start": v(39.29, -29.5) * mm, "end": v(39.54, -30.5) * mm});
            skLineSegment(sketch, "E2108", {"start": v(39.54, -30.5) * mm, "end": v(39.79, -29.5) * mm});
            skLineSegment(sketch, "E2109", {"start": v(39.79, -29.5) * mm, "end": v(39.29, -29.5) * mm});
            skLineSegment(sketch, "E2110", {"start": v(39.54, -27) * mm, "end": v(39.54, -30.5) * mm});
            skLineSegment(sketch, "E2111", {"start": v(-24.96, -30.5) * mm, "end": v(40.04, -30.5) * mm});
            skLineSegment(sketch, "E2112", {"start": v(4.54, -27) * mm, "end": v(40.04, -27) * mm});
            skLineSegment(sketch, "E2113", {"start": v(33.54, 35.25) * mm, "end": v(34.54, 35.5) * mm});
            skLineSegment(sketch, "E2114", {"start": v(34.54, 35.5) * mm, "end": v(33.54, 35.75) * mm});
            skLineSegment(sketch, "E2115", {"start": v(33.54, 35.75) * mm, "end": v(33.54, 35.25) * mm});
            skLineSegment(sketch, "E2116", {"start": v(41.94, 35.5) * mm, "end": v(34.54, 35.5) * mm});
            skLineSegment(sketch, "E2117", {"start": v(-24.46, 35.75) * mm, "end": v(-25.46, 35.5) * mm});
            skLineSegment(sketch, "E2118", {"start": v(-25.46, 35.5) * mm, "end": v(-24.46, 35.25) * mm});
            skLineSegment(sketch, "E2119", {"start": v(-24.46, 35.25) * mm, "end": v(-24.46, 35.75) * mm});
            skLineSegment(sketch, "E2120", {"start": v(34.54, 35.5) * mm, "end": v(-25.46, 35.5) * mm});
            skLineSegment(sketch, "E2121", {"start": v(34.54, 34) * mm, "end": v(34.54, 36) * mm});
            skLineSegment(sketch, "E2122", {"start": v(-25.46, 34) * mm, "end": v(-25.46, 36) * mm});
            skLineSegment(sketch, "E2123", {"start": v(39.29, 7.27) * mm, "end": v(39.04, 8.27) * mm});
            skLineSegment(sketch, "E2124", {"start": v(39.04, 8.27) * mm, "end": v(38.79, 7.27) * mm});
            skLineSegment(sketch, "E2125", {"start": v(38.79, 7.27) * mm, "end": v(39.29, 7.27) * mm});
            skLineSegment(sketch, "E2126", {"start": v(39.04, 8.3) * mm, "end": v(39.04, 8.27) * mm});
            skLineSegment(sketch, "E2127", {"start": v(38.79, 4.5) * mm, "end": v(39.04, 3.5) * mm});
            skLineSegment(sketch, "E2128", {"start": v(39.04, 3.5) * mm, "end": v(39.29, 4.5) * mm});
            skLineSegment(sketch, "E2129", {"start": v(39.29, 4.5) * mm, "end": v(38.79, 4.5) * mm});
            skLineSegment(sketch, "E2130", {"start": v(39.04, 8.27) * mm, "end": v(39.04, 3.5) * mm});
            skLineSegment(sketch, "E2131", {"start": v(35.04, 3.5) * mm, "end": v(39.54, 3.5) * mm});
            skLineSegment(sketch, "E2132", {"start": v(29.58, 8.27) * mm, "end": v(39.54, 8.27) * mm});
            skLineSegment(sketch, "E2133", {"start": v(37.79, 32.5) * mm, "end": v(37.54, 33.5) * mm});
            skLineSegment(sketch, "E2134", {"start": v(37.54, 33.5) * mm, "end": v(37.29, 32.5) * mm});
            skLineSegment(sketch, "E2135", {"start": v(37.29, 32.5) * mm, "end": v(37.79, 32.5) * mm});
            skLineSegment(sketch, "E2136", {"start": v(37.54, 32.7) * mm, "end": v(37.54, 33.5) * mm});
            skLineSegment(sketch, "E2137", {"start": v(37.29, 24) * mm, "end": v(37.54, 23) * mm});
            skLineSegment(sketch, "E2138", {"start": v(37.54, 23) * mm, "end": v(37.79, 24) * mm});
            skLineSegment(sketch, "E2139", {"start": v(37.79, 24) * mm, "end": v(37.29, 24) * mm});
            skLineSegment(sketch, "E2140", {"start": v(37.54, 24.3) * mm, "end": v(37.54, 23) * mm});
            skLineSegment(sketch, "E2141", {"start": v(28.44, 23) * mm, "end": v(38.04, 23) * mm});
            skLineSegment(sketch, "E2142", {"start": v(35.04, 33.5) * mm, "end": v(38.04, 33.5) * mm});
            skLineSegment(sketch, "E2143", {"start": v(40.79, 32.5) * mm, "end": v(40.54, 33.5) * mm});
            skLineSegment(sketch, "E2144", {"start": v(40.54, 33.5) * mm, "end": v(40.29, 32.5) * mm});
            skLineSegment(sketch, "E2145", {"start": v(40.29, 32.5) * mm, "end": v(40.79, 32.5) * mm});
            skLineSegment(sketch, "E2146", {"start": v(40.54, 21.1) * mm, "end": v(40.54, 33.5) * mm});
            skLineSegment(sketch, "E2147", {"start": v(40.29, 4.5) * mm, "end": v(40.54, 3.5) * mm});
            skLineSegment(sketch, "E2148", {"start": v(40.54, 3.5) * mm, "end": v(40.79, 4.5) * mm});
            skLineSegment(sketch, "E2149", {"start": v(40.79, 4.5) * mm, "end": v(40.29, 4.5) * mm});
            skLineSegment(sketch, "E2150", {"start": v(40.54, 15.9) * mm, "end": v(40.54, 3.5) * mm});
            skLineSegment(sketch, "E2151", {"start": v(35.04, 3.5) * mm, "end": v(41.04, 3.5) * mm});
            skLineSegment(sketch, "E2152", {"start": v(35.04, 33.5) * mm, "end": v(41.04, 33.5) * mm});
            skLineSegment(sketch, "E2153", {"start": v(-12.59, -9.75) * mm, "end": v(-12.59, -8.75) * mm});
            skLineSegment(sketch, "E2154", {"start": v(-12.59, -8.75) * mm, "end": v(-12.46, -8.62) * mm});
            skLineSegment(sketch, "E2155", {"start": v(-37.46, 3.5) * mm, "end": v(-25.96, 3.5) * mm});
            skLineSegment(sketch, "E2156", {"start": v(-25.96, 3.5) * mm, "end": v(-30.96, 5.5) * mm});
            skLineSegment(sketch, "E2157", {"start": v(-30.96, 5.5) * mm, "end": v(-30.96, 2) * mm});
            skLineSegment(sketch, "E2158", {"start": v(-30.96, 2) * mm, "end": v(-25.96, 3.5) * mm});
            skLineSegment(sketch, "E2159", {"start": v(-25.46, 3.5) * mm, "end": v(-25.46, 33.5) * mm});
            skLineSegment(sketch, "E2160", {"start": v(-25.46, 33.5) * mm, "end": v(34.54, 33.5) * mm});
            skLineSegment(sketch, "E2161", {"start": v(34.54, 33.5) * mm, "end": v(34.54, 3.5) * mm});
            skLineSegment(sketch, "E2162", {"start": v(34.54, 3.5) * mm, "end": v(-25.46, 3.5) * mm});
            skLineSegment(sketch, "E2163", {"start": v(-25.46, -30.5) * mm, "end": v(34.54, -30.5) * mm});
            skLineSegment(sketch, "E2164", {"start": v(34.54, -30.5) * mm, "end": v(34.54, 3.5) * mm});
            skLineSegment(sketch, "E2165", {"start": v(-25.46, 3.5) * mm, "end": v(-25.46, -30.5) * mm});
            skSolve(sketch);
        }
        {
            var Q0;
            Q0=qCreatedBy(makeId("Top.planeOp"),FACE);
            var sketch = newSketch(context, id + "F1", { "sketchPlane" : qUnion([Q0])});
            skLineSegment(sketch, "E2166.0", {"start": v(36.04, 5) * mm, "end": v(29.04, 5) * mm});
            skLineSegment(sketch, "E2166.1", {"start": v(36.04, -32) * mm, "end": v(36.04, 5) * mm});
            skLineSegment(sketch, "E2166.2", {"start": v(-26.96, -32) * mm, "end": v(-19.96, -32) * mm});
            skLineSegment(sketch, "E2166.3", {"start": v(-26.96, 5) * mm, "end": v(-26.96, -32) * mm});
            skArc(sketch, "E2167", {"start": v(29.04, 8) * mm, "mid": v(26.04, 11) * mm, "end": v(23.04, 8) * mm});
            skCircle(sketch, "E2168", {"center": v(26.04, 8) * mm, "radius": 1.2 * mm});
            skLineSegment(sketch, "E2169", {"start": v(23.04, 8) * mm, "end": v(23.04, 5) * mm});
            skLineSegment(sketch, "E2170", {"start": v(29.04, 8) * mm, "end": v(29.04, 5) * mm});
            skLineSegment(sketch, "E2171.trimOffspring", {"start": v(23.04, 5) * mm, "end": v(-13.96, 5) * mm});
            skArc(sketch, "E2172", {"start": v(-19.96, -35) * mm, "mid": v(-16.96, -38) * mm, "end": v(-13.96, -35) * mm});
            skCircle(sketch, "E2173", {"center": v(-16.96, -35) * mm, "radius": 1.2 * mm});
            skLineSegment(sketch, "E2174", {"start": v(-19.96, -35) * mm, "end": v(-19.96, -32) * mm});
            skLineSegment(sketch, "E2175", {"start": v(-13.96, -35) * mm, "end": v(-13.96, -32) * mm});
            skLineSegment(sketch, "E2176.trimOffspring", {"start": v(-13.96, -32) * mm, "end": v(23.04, -32) * mm});
            skCircle(sketch, "E2177", {"center": v(4.54, -26.5) * mm, "radius": 1.6 * mm});
            skArc(sketch, "E2178", {"start": v(-13.96, 8) * mm, "mid": v(-16.96, 11) * mm, "end": v(-19.96, 8) * mm});
            skCircle(sketch, "E2179", {"center": v(-16.96, 8) * mm, "radius": 1.2 * mm});
            skLineSegment(sketch, "E2180", {"start": v(-19.96, 8) * mm, "end": v(-19.96, 5) * mm});
            skLineSegment(sketch, "E2181", {"start": v(-13.96, 8) * mm, "end": v(-13.96, 5) * mm});
            skArc(sketch, "E2182", {"start": v(23.04, -35) * mm, "mid": v(26.04, -38) * mm, "end": v(29.04, -35) * mm});
            skCircle(sketch, "E2183", {"center": v(26.04, -35) * mm, "radius": 1.2 * mm});
            skLineSegment(sketch, "E2184", {"start": v(23.04, -35) * mm, "end": v(23.04, -32) * mm});
            skLineSegment(sketch, "E2185", {"start": v(29.04, -35) * mm, "end": v(29.04, -32) * mm});
            skLineSegment(sketch, "E2186.trimOffspring", {"start": v(-19.96, 5) * mm, "end": v(-26.96, 5) * mm});
            skLineSegment(sketch, "E2187.trimOffspring", {"start": v(29.04, -32) * mm, "end": v(36.04, -32) * mm});
            skSolve(sketch);
        }
        {
            var Q0;
            Q0 = qSketchRegion(id + "F1", true);
            extrude(context, id + "F2", {"entities" : qUnion([Q0]), "depth" : 1 * mm, "offsetDistance" : 25 * mm});
        }
        {
            var Q0;
            Q0=makeQuery(id+"F2.opExtrude","CAP_FACE",FACE,{"disambiguationData":[OSD([sQuery(id+"F1.wireOp",EDGE,"E2166.0"),sQuery(id+"F1.wireOp",EDGE,"E2166.1"),sQuery(id+"F1.wireOp",EDGE,"E2166.2"),sQuery(id+"F1.wireOp",EDGE,"E2166.3")])],"isStart":false});
            var sketch = newSketch(context, id + "F3", { "sketchPlane" : qUnion([Q0])});
            skLineSegment(sketch, "E2188.0", {"start": v(34.04, 3) * mm, "end": v(-24.96, 3) * mm});
            skLineSegment(sketch, "E2188.1", {"start": v(34.04, -30) * mm, "end": v(34.04, 3) * mm});
            skLineSegment(sketch, "E2188.2", {"start": v(-24.96, -30) * mm, "end": v(34.04, -30) * mm});
            skLineSegment(sketch, "E2188.3", {"start": v(-24.96, 3) * mm, "end": v(-24.96, -30) * mm});
            skLineSegment(sketch, "E2189.0", {"start": v(44.04, 13) * mm, "end": v(-34.96, 13) * mm});
            skLineSegment(sketch, "E2189.1", {"start": v(44.04, -40) * mm, "end": v(44.04, 13) * mm});
            skLineSegment(sketch, "E2189.2", {"start": v(-34.96, -40) * mm, "end": v(44.04, -40) * mm});
            skLineSegment(sketch, "E2189.3", {"start": v(-34.96, 13) * mm, "end": v(-34.96, -40) * mm});
            skSolve(sketch);
        }
        {
            var Q0;
            Q0=makeQuery(id+"F3.imprint","IMPRINT",FACE,{"disambiguationData":[TD([[makeQuery(id+"F3.imprint","IMPRINT",EDGE,{"derivedFrom":sQuery(id+"F3.wireOp",EDGE,"E2188.0")}),-1.0]])]});
            extrude(context, id + "F4", {"entities" : qUnion([Q0]), "operationType" : NewBodyOperationType.ADD, "depth" : 14.5 * mm, "offsetDistance" : 25 * mm});
        }
        {
            var Q0;
            Q0=makeQuery(id+"F4.opExtrude","CAP_FACE",FACE,{"disambiguationData":[OSD([sQuery(id+"F1.wireOp",EDGE,"E2166.0"),sQuery(id+"F1.wireOp",EDGE,"E2166.1"),sQuery(id+"F1.wireOp",EDGE,"E2166.2"),sQuery(id+"F1.wireOp",EDGE,"E2166.3"),sQuery(id+"F3.wireOp",EDGE,"E2188.0"),sQuery(id+"F3.wireOp",EDGE,"E2188.1"),sQuery(id+"F3.wireOp",EDGE,"E2188.2"),sQuery(id+"F3.wireOp",EDGE,"E2188.3")])],"isStart":false});
            var sketch = newSketch(context, id + "F5", { "sketchPlane" : qUnion([Q0])});
            skLineSegment(sketch, "E2190.bottom", {"start": v(36.04, 2.4) * mm, "end": v(34.04, 2.4) * mm});
            skLineSegment(sketch, "E2190.top", {"start": v(36.04, -29.4) * mm, "end": v(34.04, -29.4) * mm});
            skLineSegment(sketch, "E2190.left", {"start": v(36.04, 2.4) * mm, "end": v(36.04, -29.4) * mm});
            skLineSegment(sketch, "E2190.right", {"start": v(34.04, 2.4) * mm, "end": v(34.04, -29.4) * mm});
            skSolve(sketch);
        }
        {
            var Q0;
            Q0=makeQuery(id+"F5.imprint","IMPRINT",FACE,{"disambiguationData":[TD([[makeQuery(id+"F5.imprint","IMPRINT",EDGE,{"derivedFrom":sQuery(id+"F5.wireOp",EDGE,"E2190.bottom")}),1.0]])]});
            extrude(context, id + "F6", {"entities" : qUnion([Q0]), "operationType" : NewBodyOperationType.REMOVE, "oppositeDirection" : true, "depth" : 13 * mm, "offsetDistance" : 25 * mm});
        }
        {
            var Q0;
            Q0=makeQuery(id+"F4.opExtrude","CAP_FACE",FACE,{"disambiguationData":[OSD([sQuery(id+"F1.wireOp",EDGE,"E2166.0"),sQuery(id+"F1.wireOp",EDGE,"E2166.1"),sQuery(id+"F1.wireOp",EDGE,"E2166.2"),sQuery(id+"F1.wireOp",EDGE,"E2166.3"),sQuery(id+"F3.wireOp",EDGE,"E2188.0"),sQuery(id+"F3.wireOp",EDGE,"E2188.1"),sQuery(id+"F3.wireOp",EDGE,"E2188.2"),sQuery(id+"F3.wireOp",EDGE,"E2188.3")])],"isStart":false});
            var sketch = newSketch(context, id + "F7", { "sketchPlane" : qUnion([Q0])});
            skLineSegment(sketch, "E2191.bottom", {"start": v(-24.96, 3) * mm, "end": v(-26.96, 3) * mm});
            skLineSegment(sketch, "E2191.top", {"start": v(-24.96, -30) * mm, "end": v(-26.96, -30) * mm});
            skLineSegment(sketch, "E2191.left", {"start": v(-24.96, 3) * mm, "end": v(-24.96, -30) * mm});
            skLineSegment(sketch, "E2191.right", {"start": v(-26.96, 3) * mm, "end": v(-26.96, -30) * mm});
            skSolve(sketch);
        }
        {
            var Q0;
            Q0=makeQuery(id+"F7.imprint","IMPRINT",FACE,{"disambiguationData":[TD([[makeQuery(id+"F7.imprint","IMPRINT",EDGE,{"derivedFrom":sQuery(id+"F7.wireOp",EDGE,"E2191.bottom")}),1.0]])]});
            extrude(context, id + "F8", {"entities" : qUnion([Q0]), "operationType" : NewBodyOperationType.REMOVE, "oppositeDirection" : true, "depth" : 7.4 * mm, "offsetDistance" : 25 * mm});
        }
        {
            var Q0;
            {var subQ0=sQuery(id+"F1.wireOp",EDGE,"E2166.3");Q0=makeQuery(id+"F4.boolean.opBoolean","MERGE",FACE,{"derivedFrom":[makeQuery(id+"F2.opExtrude","SWEPT_FACE",FACE,{"disambiguationData":[OSD([subQ0])]}),makeQuery(id+"F4.opExtrude","SWEPT_FACE",FACE,{"disambiguationData":[OSD([subQ0])]})]});}
            var sketch = newSketch(context, id + "F9", { "sketchPlane" : qUnion([Q0])});
            skLineSegment(sketch, "E2192.bottom", {"start": v(32, 0) * mm, "end": v(38, 0) * mm});
            skLineSegment(sketch, "E2192.left", {"start": v(32, 0) * mm, "end": v(32, 5) * mm});
            skLineSegment(sketch, "E2192.right", {"start": v(38, 0) * mm, "end": v(38, 9) * mm});
            skLineSegment(sketch, "E2193.bottom", {"start": v(32, 0) * mm, "end": v(26, 0) * mm});
            skLineSegment(sketch, "E2193.right", {"start": v(26, 0) * mm, "end": v(26, 9) * mm});
            skLineSegment(sketch, "E2194", {"start": v(38, 9) * mm, "end": v(32, 5) * mm});
            skLineSegment(sketch, "E2195", {"start": v(26, 9) * mm, "end": v(32, 5) * mm});
            skPoint(sketch, "E2193.top.start.orphan", {"position": v(32, 9) * mm});
            skLineSegment(sketch, "E2196.bottom", {"start": v(-5, 0) * mm, "end": v(-11, 0) * mm});
            skLineSegment(sketch, "E2196.left", {"start": v(-5, 0) * mm, "end": v(-5, 5) * mm});
            skLineSegment(sketch, "E2196.right", {"start": v(-11, 0) * mm, "end": v(-11, 9) * mm});
            skLineSegment(sketch, "E2197", {"start": v(-11, 9) * mm, "end": v(-5, 5) * mm});
            skSolve(sketch);
        }
        {
            var Q0;
            Q0=makeQuery(id+"F9.imprint","IMPRINT",FACE,{"disambiguationData":[TD([[makeQuery(id+"F9.imprint","IMPRINT",EDGE,{"derivedFrom":sQuery(id+"F9.wireOp",EDGE,"E2192.bottom")}),1.0]])]});
            var Q1;
            Q1=makeQuery(id+"F9.imprint","IMPRINT",FACE,{"disambiguationData":[TD([[makeQuery(id+"F9.imprint","IMPRINT",EDGE,{"derivedFrom":sQuery(id+"F9.wireOp",EDGE,"E2193.bottom")}),-1.0]])]});
            var Q2;
            Q2=makeQuery(id+"F9.imprint","IMPRINT",FACE,{"disambiguationData":[TD([[makeQuery(id+"F9.imprint","IMPRINT",EDGE,{"derivedFrom":sQuery(id+"F9.wireOp",EDGE,"E2196.bottom")}),-1.0]])]});
            extrude(context, id + "F10", {"entities" : qUnion([Q0, Q1, Q2]), "operationType" : NewBodyOperationType.REMOVE, "oppositeDirection" : true, "depth" : 80 * mm, "offsetDistance" : 25 * mm});
        }
        {
            var Q0;
            {var subQ0=sQuery(id+"F1.wireOp",EDGE,"E2166.3");var subQ1=sQuery(id+"F1.wireOp",EDGE,"E2166.2");Q0=makeQuery(id+"F4.boolean.opBoolean","MERGE",EDGE,{"derivedFrom":[makeQuery(id+"F2.opExtrude","SWEPT_EDGE",EDGE,{"disambiguationData":[OSD([subQ1,subQ0])]}),makeQuery(id+"F4.opExtrude","SWEPT_EDGE",EDGE,{"disambiguationData":[OSD([subQ1,subQ0])]})]});}
            var Q1;
            {var subQ0=sQuery(id+"F1.wireOp",EDGE,"E2174");var subQ1=sQuery(id+"F1.wireOp",EDGE,"E2166.2");Q1=makeQuery(id+"F4.boolean.opBoolean","MERGE",EDGE,{"derivedFrom":[makeQuery(id+"F2.opExtrude","SWEPT_EDGE",EDGE,{"disambiguationData":[OSD([subQ1,subQ0])]}),makeQuery(id+"F4.opExtrude","SWEPT_EDGE",EDGE,{"disambiguationData":[OSD([subQ1,subQ0])]})]});}
            var Q2;
            {var subQ0=sQuery(id+"F1.wireOp",EDGE,"E2176.trimOffspring");var subQ1=sQuery(id+"F1.wireOp",EDGE,"E2175");Q2=makeQuery(id+"F4.boolean.opBoolean","MERGE",EDGE,{"derivedFrom":[makeQuery(id+"F2.opExtrude","SWEPT_EDGE",EDGE,{"disambiguationData":[OSD([subQ1,subQ0])]}),makeQuery(id+"F4.opExtrude","SWEPT_EDGE",EDGE,{"disambiguationData":[OSD([subQ1,subQ0])]})]});}
            var Q3;
            {var subQ0=sQuery(id+"F1.wireOp",EDGE,"E2172");Q3=makeQuery(id+"F10.boolean.opBoolean","INTERSECT",EDGE,{"derivedFrom":[makeQuery(id+"F4.boolean.opBoolean","MERGE",FACE,{"derivedFrom":[makeQuery(id+"F2.opExtrude","SWEPT_FACE",FACE,{"disambiguationData":[OSD([subQ0])]}),makeQuery(id+"F4.opExtrude","SWEPT_FACE",FACE,{"disambiguationData":[OSD([subQ0])]})]}),makeQuery(id+"F10.opExtrude","SWEPT_FACE",FACE,{"disambiguationData":[OSD([sQuery(id+"F9.wireOp",EDGE,"E2194")])]})]});}
            var Q4;
            {var subQ0=sQuery(id+"F1.wireOp",EDGE,"E2171.trimOffspring");var subQ1=sQuery(id+"F1.wireOp",EDGE,"E2166.3");Q4=makeQuery(id+"F4.boolean.opBoolean","MERGE",EDGE,{"derivedFrom":[makeQuery(id+"F2.opExtrude","SWEPT_EDGE",EDGE,{"disambiguationData":[OSD([subQ1,subQ0])]}),makeQuery(id+"F4.opExtrude","SWEPT_EDGE",EDGE,{"disambiguationData":[OSD([subQ1,subQ0])]})]});}
            var Q5;
            {var subQ0=sQuery(id+"F1.wireOp",EDGE,"E2171.trimOffspring");var subQ1=sQuery(id+"F1.wireOp",EDGE,"E2169");Q5=makeQuery(id+"F4.boolean.opBoolean","MERGE",EDGE,{"derivedFrom":[makeQuery(id+"F2.opExtrude","SWEPT_EDGE",EDGE,{"disambiguationData":[OSD([subQ1,subQ0])]}),makeQuery(id+"F4.opExtrude","SWEPT_EDGE",EDGE,{"disambiguationData":[OSD([subQ1,subQ0])]})]});}
            var Q6;
            {var subQ0=sQuery(id+"F1.wireOp",EDGE,"E2170");var subQ1=sQuery(id+"F1.wireOp",EDGE,"E2166.0");Q6=makeQuery(id+"F4.boolean.opBoolean","MERGE",EDGE,{"derivedFrom":[makeQuery(id+"F2.opExtrude","SWEPT_EDGE",EDGE,{"disambiguationData":[OSD([subQ1,subQ0])]}),makeQuery(id+"F4.opExtrude","SWEPT_EDGE",EDGE,{"disambiguationData":[OSD([subQ1,subQ0])]})]});}
            var Q7;
            {var subQ0=sQuery(id+"F1.wireOp",EDGE,"E2167");Q7=makeQuery(id+"F10.boolean.opBoolean","INTERSECT",EDGE,{"derivedFrom":[makeQuery(id+"F4.boolean.opBoolean","MERGE",FACE,{"derivedFrom":[makeQuery(id+"F2.opExtrude","SWEPT_FACE",FACE,{"disambiguationData":[OSD([subQ0])]}),makeQuery(id+"F4.opExtrude","SWEPT_FACE",FACE,{"disambiguationData":[OSD([subQ0])]})]}),makeQuery(id+"F10.opExtrude","SWEPT_FACE",FACE,{"disambiguationData":[OSD([sQuery(id+"F9.wireOp",EDGE,"E2195")])]})]});}
            var Q8;
            {var subQ0=sQuery(id+"F1.wireOp",EDGE,"E2166.1");var subQ1=sQuery(id+"F1.wireOp",EDGE,"E2166.0");Q8=makeQuery(id+"F4.boolean.opBoolean","MERGE",EDGE,{"derivedFrom":[makeQuery(id+"F2.opExtrude","SWEPT_EDGE",EDGE,{"disambiguationData":[OSD([subQ1,subQ0])]}),makeQuery(id+"F4.opExtrude","SWEPT_EDGE",EDGE,{"disambiguationData":[OSD([subQ1,subQ0])]})]});}
            var Q9;
            {var subQ0=sQuery(id+"F1.wireOp",EDGE,"E2176.trimOffspring");var subQ1=sQuery(id+"F1.wireOp",EDGE,"E2166.1");Q9=makeQuery(id+"F4.boolean.opBoolean","MERGE",EDGE,{"derivedFrom":[makeQuery(id+"F2.opExtrude","SWEPT_EDGE",EDGE,{"disambiguationData":[OSD([subQ1,subQ0])]}),makeQuery(id+"F4.opExtrude","SWEPT_EDGE",EDGE,{"disambiguationData":[OSD([subQ1,subQ0])]})]});}
            var Q10;
            {var subQ0=sQuery(id+"F1.wireOp",EDGE,"E2180");Q10=makeQuery(id+"F10.boolean.opBoolean","INTERSECT",EDGE,{"derivedFrom":[makeQuery(id+"F4.boolean.opBoolean","MERGE",FACE,{"derivedFrom":[makeQuery(id+"F2.opExtrude","SWEPT_FACE",FACE,{"disambiguationData":[OSD([subQ0])]}),makeQuery(id+"F4.opExtrude","SWEPT_FACE",FACE,{"disambiguationData":[OSD([subQ0])]})]}),makeQuery(id+"F10.opExtrude","SWEPT_FACE",FACE,{"disambiguationData":[OSD([sQuery(id+"F9.wireOp",EDGE,"E2197")])]})]});}
            var Q11;
            {var subQ0=sQuery(id+"F1.wireOp",EDGE,"E2182");Q11=makeQuery(id+"F10.boolean.opBoolean","INTERSECT",EDGE,{"derivedFrom":[makeQuery(id+"F4.boolean.opBoolean","MERGE",FACE,{"derivedFrom":[makeQuery(id+"F2.opExtrude","SWEPT_FACE",FACE,{"disambiguationData":[OSD([subQ0])]}),makeQuery(id+"F4.opExtrude","SWEPT_FACE",FACE,{"disambiguationData":[OSD([subQ0])]})]}),makeQuery(id+"F10.opExtrude","SWEPT_FACE",FACE,{"disambiguationData":[OSD([sQuery(id+"F9.wireOp",EDGE,"E2194")])]})]});}
            var Q12;
            Q12=makeQuery(id+"F10.boolean.opBoolean","MERGE",EDGE,{"derivedFrom":[makeQuery(id+"F2.opExtrude","CAP_EDGE",EDGE,{"disambiguationData":[OSD([sQuery(id+"F1.wireOp",EDGE,"E2166.2")])],"isStart":true}),makeQuery(id+"F2.opExtrude","CAP_EDGE",EDGE,{"disambiguationData":[OSD([sQuery(id+"F1.wireOp",EDGE,"E2176.trimOffspring")])],"isStart":true}),makeQuery(id+"F2.opExtrude","CAP_EDGE",EDGE,{"disambiguationData":[OSD([sQuery(id+"F1.wireOp",EDGE,"E2187.trimOffspring")])],"isStart":true}),makeQuery(id+"F10.opExtrude","SWEPT_EDGE",EDGE,{"disambiguationData":[OSD([sQuery(id+"F9.wireOp",EDGE,"E2192.bottom"),sQuery(id+"F9.wireOp",EDGE,"E2193.bottom"),sQuery(id+"F9.wireOp",EDGE,"E2192.left")])]})]});
            var Q13;
            Q13=makeQuery(id+"F2.opExtrude","CAP_EDGE",EDGE,{"disambiguationData":[OSD([sQuery(id+"F1.wireOp",EDGE,"E2166.1")])],"isStart":true});
            var Q14;
            Q14=makeQuery(id+"F10.boolean.opBoolean","MERGE",EDGE,{"derivedFrom":[makeQuery(id+"F2.opExtrude","CAP_EDGE",EDGE,{"disambiguationData":[OSD([sQuery(id+"F1.wireOp",EDGE,"E2166.0")])],"isStart":true}),makeQuery(id+"F2.opExtrude","CAP_EDGE",EDGE,{"disambiguationData":[OSD([sQuery(id+"F1.wireOp",EDGE,"E2171.trimOffspring")])],"isStart":true}),makeQuery(id+"F2.opExtrude","CAP_EDGE",EDGE,{"disambiguationData":[OSD([sQuery(id+"F1.wireOp",EDGE,"E2186.trimOffspring")])],"isStart":true}),makeQuery(id+"F10.opExtrude","SWEPT_EDGE",EDGE,{"disambiguationData":[OSD([sQuery(id+"F1.wireOp",EDGE,"E2166.3"),sQuery(id+"F9.wireOp",EDGE,"E2196.bottom"),sQuery(id+"F9.wireOp",EDGE,"E2196.left")])]})]});
            var Q15;
            Q15=makeQuery(id+"F2.opExtrude","CAP_EDGE",EDGE,{"disambiguationData":[OSD([sQuery(id+"F1.wireOp",EDGE,"E2166.3")])],"isStart":true});
            fillet(context, id + "F11", {"entities" : qUnion([Q0, Q1, Q2, Q3, Q4, Q5, Q6, Q7, Q8, Q9, Q10, Q11, Q12, Q13, Q14, Q15]), "radius" : 1 * mm, "tangentPropagation" : true, "allowEdgeOverflow" : false});
        }
        {
            var Q0;
            Q0=makeQuery(id+"F2.opExtrude","CAP_FACE",FACE,{"disambiguationData":[OSD([sQuery(id+"F1.wireOp",EDGE,"E2166.0"),sQuery(id+"F1.wireOp",EDGE,"E2166.1"),sQuery(id+"F1.wireOp",EDGE,"E2166.2"),sQuery(id+"F1.wireOp",EDGE,"E2166.3"),sQuery(id+"F1.wireOp",EDGE,"E2167"),sQuery(id+"F1.wireOp",EDGE,"E2168"),sQuery(id+"F1.wireOp",EDGE,"E2169"),sQuery(id+"F1.wireOp",EDGE,"E2170"),sQuery(id+"F1.wireOp",EDGE,"E2171.trimOffspring"),sQuery(id+"F1.wireOp",EDGE,"E2172"),sQuery(id+"F1.wireOp",EDGE,"E2173"),sQuery(id+"F1.wireOp",EDGE,"E2174"),sQuery(id+"F1.wireOp",EDGE,"E2175"),sQuery(id+"F1.wireOp",EDGE,"E2176.trimOffspring")])],"isStart":false});
            var sketch = newSketch(context, id + "F12", { "sketchPlane" : qUnion([Q0])});
            skSolve(sketch);
        }
        {
            var Q0;
            {var subQ0=sQuery(id+"F1.wireOp",EDGE,"E2173");var subQ1=sQuery(id+"F1.wireOp",EDGE,"E2172");var subQ2=sQuery(id+"F3.wireOp",EDGE,"E2188.2");var subQ3=sQuery(id+"F3.wireOp",EDGE,"E2188.1");var subQ4=sQuery(id+"F1.wireOp",EDGE,"E2185");var subQ5=sQuery(id+"F1.wireOp",EDGE,"E2184");var subQ6=sQuery(id+"F1.wireOp",EDGE,"E2166.1");var subQ7=sQuery(id+"F1.wireOp",EDGE,"E2175");var subQ8=sQuery(id+"F1.wireOp",EDGE,"E2183");var subQ9=sQuery(id+"F1.wireOp",EDGE,"E2166.3");var subQ10=sQuery(id+"F1.wireOp",EDGE,"E2182");var subQ11=sQuery(id+"F1.wireOp",EDGE,"E2166.2");var subQ12=sQuery(id+"F1.wireOp",EDGE,"E2176.trimOffspring");var subQ13=sQuery(id+"F1.wireOp",EDGE,"E2187.trimOffspring");var subQ14=sQuery(id+"F1.wireOp",EDGE,"E2174");Q0=makeQuery(id+"F8.boolean.opBoolean","SPLIT",FACE,{"disambiguationData":[TD([makeQuery(id+"F2.opExtrude","SWEPT_FACE",FACE,{"disambiguationData":[OSD([subQ11])]})])],"derivedFrom":makeQuery(id+"F4.opExtrude","CAP_FACE",FACE,{"disambiguationData":[OSD([sQuery(id+"F1.wireOp",EDGE,"E2166.0"),subQ6,subQ11,subQ9,sQuery(id+"F1.wireOp",EDGE,"E2167"),sQuery(id+"F1.wireOp",EDGE,"E2168"),sQuery(id+"F1.wireOp",EDGE,"E2169"),sQuery(id+"F1.wireOp",EDGE,"E2170"),sQuery(id+"F1.wireOp",EDGE,"E2171.trimOffspring"),subQ1,subQ0,subQ14,subQ7,subQ12,sQuery(id+"F1.wireOp",EDGE,"E2178"),sQuery(id+"F1.wireOp",EDGE,"E2179"),sQuery(id+"F1.wireOp",EDGE,"E2180"),sQuery(id+"F1.wireOp",EDGE,"E2181"),subQ10,subQ8,subQ5,subQ4,sQuery(id+"F1.wireOp",EDGE,"E2186.trimOffspring"),subQ13,sQuery(id+"F3.wireOp",EDGE,"E2188.0"),subQ3,subQ2,sQuery(id+"F3.wireOp",EDGE,"E2188.3")])],"isStart":false})});}
            var sketch = newSketch(context, id + "F13", { "sketchPlane" : qUnion([Q0])});
            skLineSegment(sketch, "E2198.bottom", {"start": v(-11.61, -30) * mm, "end": v(1.19, -30) * mm});
            skLineSegment(sketch, "E2198.top", {"start": v(-11.61, -32) * mm, "end": v(1.19, -32) * mm});
            skLineSegment(sketch, "E2198.left", {"start": v(-11.61, -30) * mm, "end": v(-11.61, -32) * mm});
            skLineSegment(sketch, "E2198.right", {"start": v(1.19, -30) * mm, "end": v(1.19, -32) * mm});
            skSolve(sketch);
        }
        {
            var Q0;
            Q0 = qSketchRegion(id + "F13", true);
            extrude(context, id + "F14", {"entities" : qUnion([Q0]), "operationType" : NewBodyOperationType.REMOVE, "oppositeDirection" : true, "depth" : 5.5 * mm, "offsetDistance" : 25 * mm});
        }
        {
            var Q0;
            Q0=makeQuery(id+"F12.imprint","IMPRINT",FACE,{"disambiguationData":[TD([[makeQuery(id+"F12.imprint","IMPRINT",EDGE,{"derivedFrom":makeQuery(id+"F2.opExtrude","CAP_EDGE",EDGE,{"disambiguationData":[OSD([sQuery(id+"F1.wireOp",EDGE,"E2177")])],"isStart":false})}),-1.0]])]});
            var sketch = newSketch(context, id + "F15", { "sketchPlane" : qUnion([Q0])});
            skLineSegment(sketch, "E2199.bottom", {"start": v(9.54, -5) * mm, "end": v(-0.46, -5) * mm});
            skLineSegment(sketch, "E2199.top", {"start": v(9.54, 4.3) * mm, "end": v(-0.46, 4.3) * mm});
            skLineSegment(sketch, "E2199.left", {"start": v(9.54, -5) * mm, "end": v(9.54, 4.3) * mm});
            skLineSegment(sketch, "E2199.right", {"start": v(-0.46, -5) * mm, "end": v(-0.46, 4.3) * mm});
            skSolve(sketch);
        }
        {
            var Q0;
            Q0 = qSketchRegion(id + "F15", true);
            extrude(context, id + "F16", {"entities" : qUnion([Q0]), "operationType" : NewBodyOperationType.REMOVE, "endBound" : BoundingType.THROUGH_ALL, "depth" : 25 * mm, "offsetDistance" : 25 * mm, "hasSecondDirection" : true, "secondDirectionBound" : SecondDirectionBoundingType.UP_TO_NEXT, "secondDirectionOppositeDirection" : true, "secondDirectionDepth" : 25 * mm});
        }
    });
